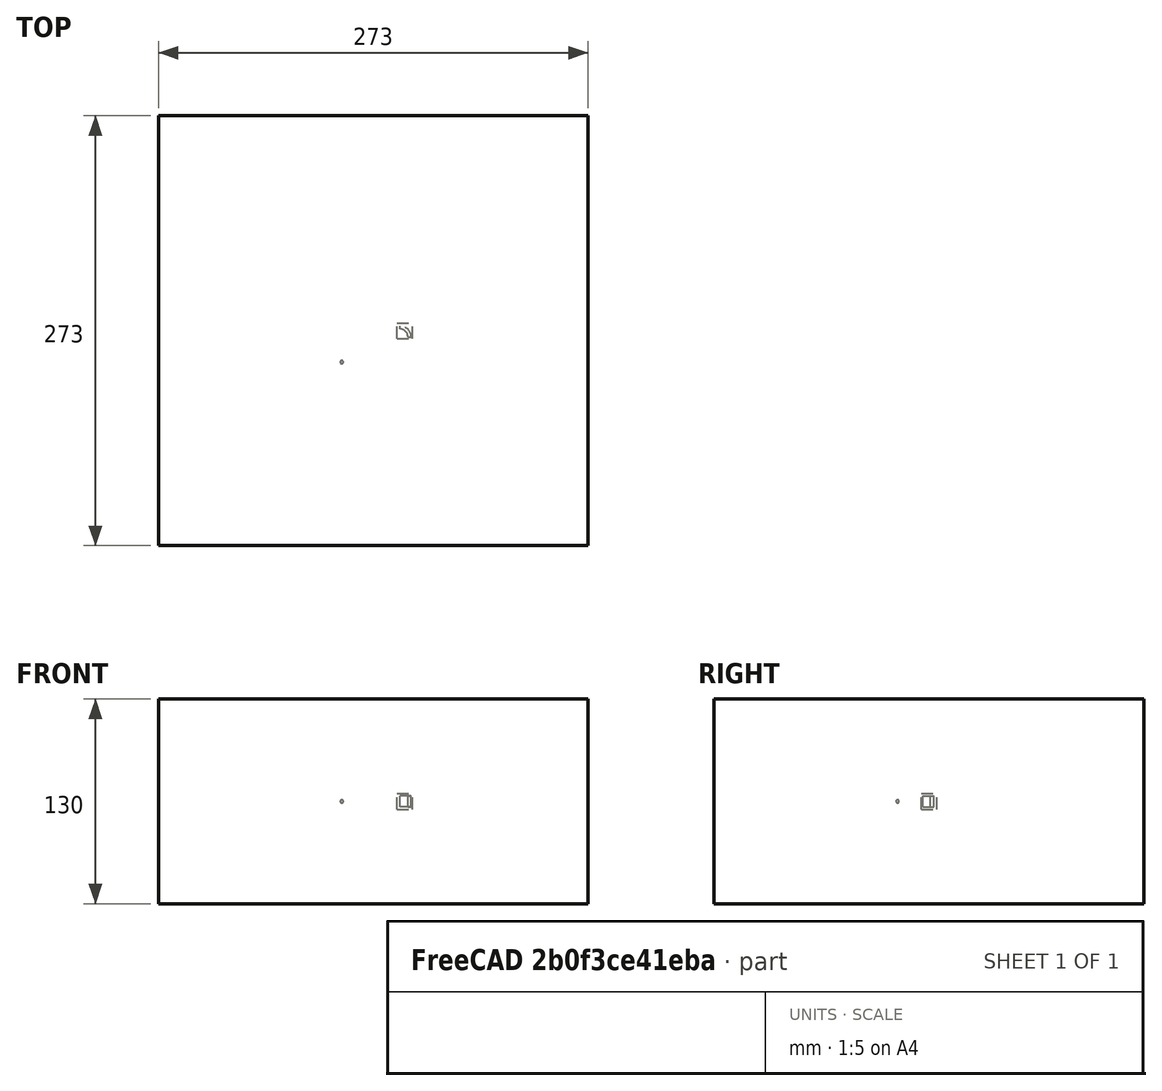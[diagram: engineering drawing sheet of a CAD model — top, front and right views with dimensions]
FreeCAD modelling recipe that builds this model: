
FCSTD DOCUMENT  (FreeCAD 0.21R33694 (Git))
Label: polarArray-of-Part-base-xformed-offcenter
License: All rights reserved
LicenseURL: http://en.wikipedia.org/wiki/All_rights_reserved
objects: App::DocumentObjectGroupPython×1251, App::Part×5, Part::FeaturePython×4, Part::Sphere×1
note: 4 computed .brp shape members not serialized (recipe doc carries the construction recipe); baked Part::Feature solids carry a one-line shape summary decoded from their .brp

FEATURE [App::DocumentObjectGroupPython] HALFPI  # scripted group (container) (typed FeaturePython)
  name = HALFPI
  value = pi/2.
FEATURE [App::DocumentObjectGroupPython] PI  # scripted group (container) (typed FeaturePython)
  name = PI
  value = 1.*pi
FEATURE [App::DocumentObjectGroupPython] TWOPI  # scripted group (container) (typed FeaturePython)
  name = TWOPI
  value = 2.*pi
FEATURE [App::DocumentObjectGroupPython] Constants  # scripted group (container) (typed FeaturePython)
  Group = -> [HALFPI,PI,TWOPI]
FEATURE [App::DocumentObjectGroupPython] Variables  # scripted group (container) (typed FeaturePython)
FEATURE [App::DocumentObjectGroupPython] Quantities  # scripted group (container) (typed FeaturePython)
FEATURE [App::DocumentObjectGroupPython] Isotopes  # scripted group (container) (typed FeaturePython)
FEATURE [App::DocumentObjectGroupPython] Elements  # scripted group (container) (typed FeaturePython)
FEATURE [App::DocumentObjectGroupPython] Matrix  # scripted group (container) (typed FeaturePython)
FEATURE [App::DocumentObjectGroupPython] Surfaces  # scripted group (container) (typed FeaturePython)
FEATURE [App::DocumentObjectGroupPython] Opticals  # scripted group (container) (typed FeaturePython)
  Group = -> [Matrix,Surfaces]
FEATURE [App::DocumentObjectGroupPython] G4Isotopes  # scripted group (container) (typed FeaturePython)
FEATURE [App::DocumentObjectGroupPython] H_element  # scripted group (container) (typed FeaturePython)
  Z = 1
  atom_value = 1.008
  formula = H
  name = H_element
FEATURE [App::DocumentObjectGroupPython] He_element  # scripted group (container) (typed FeaturePython)
  Z = 2
  atom_value = 4.0026
  formula = He
  name = He_element
FEATURE [App::DocumentObjectGroupPython] Li_element  # scripted group (container) (typed FeaturePython)
  Z = 3
  atom_value = 6.94
  formula = Li
  name = Li_element
FEATURE [App::DocumentObjectGroupPython] Be_element  # scripted group (container) (typed FeaturePython)
  Z = 4
  atom_value = 9.01218
  formula = Be
  name = Be_element
FEATURE [App::DocumentObjectGroupPython] B_element  # scripted group (container) (typed FeaturePython)
  Z = 5
  atom_value = 10.81
  formula = B
  name = B_element
FEATURE [App::DocumentObjectGroupPython] C_element  # scripted group (container) (typed FeaturePython)
  Z = 6
  atom_value = 12.011
  formula = C
  name = C_element
FEATURE [App::DocumentObjectGroupPython] N_element  # scripted group (container) (typed FeaturePython)
  Z = 7
  atom_value = 14.007
  formula = N
  name = N_element
FEATURE [App::DocumentObjectGroupPython] O_element  # scripted group (container) (typed FeaturePython)
  Z = 8
  atom_value = 15.999
  formula = O
  name = O_element
FEATURE [App::DocumentObjectGroupPython] F_element  # scripted group (container) (typed FeaturePython)
  Z = 9
  atom_value = 18.9984
  formula = F
  name = F_element
FEATURE [App::DocumentObjectGroupPython] Ne_element  # scripted group (container) (typed FeaturePython)
  Z = 10
  atom_value = 20.1797
  formula = Ne
  name = Ne_element
FEATURE [App::DocumentObjectGroupPython] Na_element  # scripted group (container) (typed FeaturePython)
  Z = 11
  atom_value = 22.9898
  formula = Na
  name = Na_element
FEATURE [App::DocumentObjectGroupPython] Mg_element  # scripted group (container) (typed FeaturePython)
  Z = 12
  atom_value = 24.305
  formula = Mg
  name = Mg_element
FEATURE [App::DocumentObjectGroupPython] Al_element  # scripted group (container) (typed FeaturePython)
  Z = 13
  atom_value = 26.9815
  formula = Al
  name = Al_element
FEATURE [App::DocumentObjectGroupPython] Si_element  # scripted group (container) (typed FeaturePython)
  Z = 14
  atom_value = 28.085
  formula = Si
  name = Si_element
FEATURE [App::DocumentObjectGroupPython] P_element  # scripted group (container) (typed FeaturePython)
  Z = 15
  atom_value = 30.9738
  formula = P
  name = P_element
FEATURE [App::DocumentObjectGroupPython] S_element  # scripted group (container) (typed FeaturePython)
  Z = 16
  atom_value = 32.06
  formula = S
  name = S_element
FEATURE [App::DocumentObjectGroupPython] Cl_element  # scripted group (container) (typed FeaturePython)
  Z = 17
  atom_value = 35.45
  formula = Cl
  name = Cl_element
FEATURE [App::DocumentObjectGroupPython] Ar_element  # scripted group (container) (typed FeaturePython)
  Z = 18
  atom_value = 39.95
  formula = Ar
  name = Ar_element
FEATURE [App::DocumentObjectGroupPython] K_element  # scripted group (container) (typed FeaturePython)
  Z = 19
  atom_value = 39.0983
  formula = K
  name = K_element
FEATURE [App::DocumentObjectGroupPython] Ca_element  # scripted group (container) (typed FeaturePython)
  Z = 20
  atom_value = 40.078
  formula = Ca
  name = Ca_element
FEATURE [App::DocumentObjectGroupPython] Sc_element  # scripted group (container) (typed FeaturePython)
  Z = 21
  atom_value = 44.9559
  formula = Sc
  name = Sc_element
FEATURE [App::DocumentObjectGroupPython] Ti_element  # scripted group (container) (typed FeaturePython)
  Z = 22
  atom_value = 47.867
  formula = Ti
  name = Ti_element
FEATURE [App::DocumentObjectGroupPython] V_element  # scripted group (container) (typed FeaturePython)
  Z = 23
  atom_value = 50.9415
  formula = V
  name = V_element
FEATURE [App::DocumentObjectGroupPython] Cr_element  # scripted group (container) (typed FeaturePython)
  Z = 24
  atom_value = 51.9961
  formula = Cr
  name = Cr_element
FEATURE [App::DocumentObjectGroupPython] Mn_element  # scripted group (container) (typed FeaturePython)
  Z = 25
  atom_value = 54.938
  formula = Mn
  name = Mn_element
FEATURE [App::DocumentObjectGroupPython] Fe_element  # scripted group (container) (typed FeaturePython)
  Z = 26
  atom_value = 55.845
  formula = Fe
  name = Fe_element
FEATURE [App::DocumentObjectGroupPython] Co_element  # scripted group (container) (typed FeaturePython)
  Z = 27
  atom_value = 58.9332
  formula = Co
  name = Co_element
FEATURE [App::DocumentObjectGroupPython] Ni_element  # scripted group (container) (typed FeaturePython)
  Z = 28
  atom_value = 58.6934
  formula = Ni
  name = Ni_element
FEATURE [App::DocumentObjectGroupPython] Cu_element  # scripted group (container) (typed FeaturePython)
  Z = 29
  atom_value = 63.546
  formula = Cu
  name = Cu_element
FEATURE [App::DocumentObjectGroupPython] Zn_element  # scripted group (container) (typed FeaturePython)
  Z = 30
  atom_value = 65.38
  formula = Zn
  name = Zn_element
FEATURE [App::DocumentObjectGroupPython] Ga_element  # scripted group (container) (typed FeaturePython)
  Z = 31
  atom_value = 69.723
  formula = Ga
  name = Ga_element
FEATURE [App::DocumentObjectGroupPython] Ge_element  # scripted group (container) (typed FeaturePython)
  Z = 32
  atom_value = 72.63
  formula = Ge
  name = Ge_element
FEATURE [App::DocumentObjectGroupPython] As_element  # scripted group (container) (typed FeaturePython)
  Z = 33
  atom_value = 74.9216
  formula = As
  name = As_element
FEATURE [App::DocumentObjectGroupPython] Se_element  # scripted group (container) (typed FeaturePython)
  Z = 34
  atom_value = 78.971
  formula = Se
  name = Se_element
FEATURE [App::DocumentObjectGroupPython] Br_element  # scripted group (container) (typed FeaturePython)
  Z = 35
  atom_value = 79.904
  formula = Br
  name = Br_element
FEATURE [App::DocumentObjectGroupPython] Kr_element  # scripted group (container) (typed FeaturePython)
  Z = 36
  atom_value = 83.798
  formula = Kr
  name = Kr_element
FEATURE [App::DocumentObjectGroupPython] Rb_element  # scripted group (container) (typed FeaturePython)
  Z = 37
  atom_value = 85.4678
  formula = Rb
  name = Rb_element
FEATURE [App::DocumentObjectGroupPython] Sr_element  # scripted group (container) (typed FeaturePython)
  Z = 38
  atom_value = 87.62
  formula = Sr
  name = Sr_element
FEATURE [App::DocumentObjectGroupPython] Y_element  # scripted group (container) (typed FeaturePython)
  Z = 39
  atom_value = 88.9058
  formula = Y
  name = Y_element
FEATURE [App::DocumentObjectGroupPython] Zr_element  # scripted group (container) (typed FeaturePython)
  Z = 40
  atom_value = 91.224
  formula = Zr
  name = Zr_element
FEATURE [App::DocumentObjectGroupPython] Nb_element  # scripted group (container) (typed FeaturePython)
  Z = 41
  atom_value = 92.9064
  formula = Nb
  name = Nb_element
FEATURE [App::DocumentObjectGroupPython] Mo_element  # scripted group (container) (typed FeaturePython)
  Z = 42
  atom_value = 95.95
  formula = Mo
  name = Mo_element
FEATURE [App::DocumentObjectGroupPython] Tc_element  # scripted group (container) (typed FeaturePython)
  Z = 43
  atom_value = 97
  formula = Tc
  name = Tc_element
FEATURE [App::DocumentObjectGroupPython] Ru_element  # scripted group (container) (typed FeaturePython)
  Z = 44
  atom_value = 101.07
  formula = Ru
  name = Ru_element
FEATURE [App::DocumentObjectGroupPython] Rh_element  # scripted group (container) (typed FeaturePython)
  Z = 45
  atom_value = 102.905
  formula = Rh
  name = Rh_element
FEATURE [App::DocumentObjectGroupPython] Pd_element  # scripted group (container) (typed FeaturePython)
  Z = 46
  atom_value = 106.42
  formula = Pd
  name = Pd_element
FEATURE [App::DocumentObjectGroupPython] Ag_element  # scripted group (container) (typed FeaturePython)
  Z = 47
  atom_value = 107.868
  formula = Ag
  name = Ag_element
FEATURE [App::DocumentObjectGroupPython] Cd_element  # scripted group (container) (typed FeaturePython)
  Z = 48
  atom_value = 112.414
  formula = Cd
  name = Cd_element
FEATURE [App::DocumentObjectGroupPython] In_element  # scripted group (container) (typed FeaturePython)
  Z = 49
  atom_value = 114.818
  formula = In
  name = In_element
FEATURE [App::DocumentObjectGroupPython] Sn_element  # scripted group (container) (typed FeaturePython)
  Z = 50
  atom_value = 118.71
  formula = Sn
  name = Sn_element
FEATURE [App::DocumentObjectGroupPython] Sb_element  # scripted group (container) (typed FeaturePython)
  Z = 51
  atom_value = 121.76
  formula = Sb
  name = Sb_element
FEATURE [App::DocumentObjectGroupPython] Te_element  # scripted group (container) (typed FeaturePython)
  Z = 52
  atom_value = 127.6
  formula = Te
  name = Te_element
FEATURE [App::DocumentObjectGroupPython] I_element  # scripted group (container) (typed FeaturePython)
  Z = 53
  atom_value = 126.904
  formula = I
  name = I_element
FEATURE [App::DocumentObjectGroupPython] Xe_element  # scripted group (container) (typed FeaturePython)
  Z = 54
  atom_value = 131.293
  formula = Xe
  name = Xe_element
FEATURE [App::DocumentObjectGroupPython] Cs_element  # scripted group (container) (typed FeaturePython)
  Z = 55
  atom_value = 132.905
  formula = Cs
  name = Cs_element
FEATURE [App::DocumentObjectGroupPython] Ba_element  # scripted group (container) (typed FeaturePython)
  Z = 56
  atom_value = 137.327
  formula = Ba
  name = Ba_element
FEATURE [App::DocumentObjectGroupPython] La_element  # scripted group (container) (typed FeaturePython)
  Z = 57
  atom_value = 138.905
  formula = La
  name = La_element
FEATURE [App::DocumentObjectGroupPython] Ce_element  # scripted group (container) (typed FeaturePython)
  Z = 58
  atom_value = 140.116
  formula = Ce
  name = Ce_element
FEATURE [App::DocumentObjectGroupPython] Pr_element  # scripted group (container) (typed FeaturePython)
  Z = 59
  atom_value = 140.908
  formula = Pr
  name = Pr_element
FEATURE [App::DocumentObjectGroupPython] Nd_element  # scripted group (container) (typed FeaturePython)
  Z = 60
  atom_value = 144.242
  formula = Nd
  name = Nd_element
FEATURE [App::DocumentObjectGroupPython] Pm_element  # scripted group (container) (typed FeaturePython)
  Z = 61
  atom_value = 145
  formula = Pm
  name = Pm_element
FEATURE [App::DocumentObjectGroupPython] Sm_element  # scripted group (container) (typed FeaturePython)
  Z = 62
  atom_value = 150.36
  formula = Sm
  name = Sm_element
FEATURE [App::DocumentObjectGroupPython] Eu_element  # scripted group (container) (typed FeaturePython)
  Z = 63
  atom_value = 151.964
  formula = Eu
  name = Eu_element
FEATURE [App::DocumentObjectGroupPython] Gd_element  # scripted group (container) (typed FeaturePython)
  Z = 64
  atom_value = 157.25
  formula = Gd
  name = Gd_element
FEATURE [App::DocumentObjectGroupPython] Tb_element  # scripted group (container) (typed FeaturePython)
  Z = 65
  atom_value = 158.925
  formula = Tb
  name = Tb_element
FEATURE [App::DocumentObjectGroupPython] Dy_element  # scripted group (container) (typed FeaturePython)
  Z = 66
  atom_value = 162.5
  formula = Dy
  name = Dy_element
FEATURE [App::DocumentObjectGroupPython] Ho_element  # scripted group (container) (typed FeaturePython)
  Z = 67
  atom_value = 164.93
  formula = Ho
  name = Ho_element
FEATURE [App::DocumentObjectGroupPython] Er_element  # scripted group (container) (typed FeaturePython)
  Z = 68
  atom_value = 167.259
  formula = Er
  name = Er_element
FEATURE [App::DocumentObjectGroupPython] Tm_element  # scripted group (container) (typed FeaturePython)
  Z = 69
  atom_value = 168.934
  formula = Tm
  name = Tm_element
FEATURE [App::DocumentObjectGroupPython] Yb_element  # scripted group (container) (typed FeaturePython)
  Z = 70
  atom_value = 173.045
  formula = Yb
  name = Yb_element
FEATURE [App::DocumentObjectGroupPython] Lu_element  # scripted group (container) (typed FeaturePython)
  Z = 71
  atom_value = 174.967
  formula = Lu
  name = Lu_element
FEATURE [App::DocumentObjectGroupPython] Hf_element  # scripted group (container) (typed FeaturePython)
  Z = 72
  atom_value = 178.49
  formula = Hf
  name = Hf_element
FEATURE [App::DocumentObjectGroupPython] Ta_element  # scripted group (container) (typed FeaturePython)
  Z = 73
  atom_value = 180.948
  formula = Ta
  name = Ta_element
FEATURE [App::DocumentObjectGroupPython] W_element  # scripted group (container) (typed FeaturePython)
  Z = 74
  atom_value = 183.84
  formula = W
  name = W_element
FEATURE [App::DocumentObjectGroupPython] Re_element  # scripted group (container) (typed FeaturePython)
  Z = 75
  atom_value = 186.207
  formula = Re
  name = Re_element
FEATURE [App::DocumentObjectGroupPython] Os_element  # scripted group (container) (typed FeaturePython)
  Z = 76
  atom_value = 190.23
  formula = Os
  name = Os_element
FEATURE [App::DocumentObjectGroupPython] Ir_element  # scripted group (container) (typed FeaturePython)
  Z = 77
  atom_value = 192.217
  formula = Ir
  name = Ir_element
FEATURE [App::DocumentObjectGroupPython] Pt_element  # scripted group (container) (typed FeaturePython)
  Z = 78
  atom_value = 195.084
  formula = Pt
  name = Pt_element
FEATURE [App::DocumentObjectGroupPython] Au_element  # scripted group (container) (typed FeaturePython)
  Z = 79
  atom_value = 196.967
  formula = Au
  name = Au_element
FEATURE [App::DocumentObjectGroupPython] Hg_element  # scripted group (container) (typed FeaturePython)
  Z = 80
  atom_value = 200.592
  formula = Hg
  name = Hg_element
FEATURE [App::DocumentObjectGroupPython] Tl_element  # scripted group (container) (typed FeaturePython)
  Z = 81
  atom_value = 204.38
  formula = Tl
  name = Tl_element
FEATURE [App::DocumentObjectGroupPython] Pb_element  # scripted group (container) (typed FeaturePython)
  Z = 82
  atom_value = 207.2
  formula = Pb
  name = Pb_element
FEATURE [App::DocumentObjectGroupPython] Bi_element  # scripted group (container) (typed FeaturePython)
  Z = 83
  atom_value = 208.98
  formula = Bi
  name = Bi_element
FEATURE [App::DocumentObjectGroupPython] Po_element  # scripted group (container) (typed FeaturePython)
  Z = 84
  atom_value = 209
  formula = Po
  name = Po_element
FEATURE [App::DocumentObjectGroupPython] At_element  # scripted group (container) (typed FeaturePython)
  Z = 85
  atom_value = 210
  formula = At
  name = At_element
FEATURE [App::DocumentObjectGroupPython] Rn_element  # scripted group (container) (typed FeaturePython)
  Z = 86
  atom_value = 222
  formula = Rn
  name = Rn_element
FEATURE [App::DocumentObjectGroupPython] Fr_element  # scripted group (container) (typed FeaturePython)
  Z = 87
  atom_value = 223
  formula = Fr
  name = Fr_element
FEATURE [App::DocumentObjectGroupPython] Ra_element  # scripted group (container) (typed FeaturePython)
  Z = 88
  atom_value = 226
  formula = Ra
  name = Ra_element
FEATURE [App::DocumentObjectGroupPython] Ac_element  # scripted group (container) (typed FeaturePython)
  Z = 89
  atom_value = 227
  formula = Ac
  name = Ac_element
FEATURE [App::DocumentObjectGroupPython] Th_element  # scripted group (container) (typed FeaturePython)
  Z = 90
  atom_value = 232.038
  formula = Th
  name = Th_element
FEATURE [App::DocumentObjectGroupPython] Pa_element  # scripted group (container) (typed FeaturePython)
  Z = 91
  atom_value = 231.036
  formula = Pa
  name = Pa_element
FEATURE [App::DocumentObjectGroupPython] U_element  # scripted group (container) (typed FeaturePython)
  Z = 92
  atom_value = 238.029
  formula = U
  name = U_element
FEATURE [App::DocumentObjectGroupPython] Np_element  # scripted group (container) (typed FeaturePython)
  Z = 93
  atom_value = 237
  formula = Np
  name = Np_element
FEATURE [App::DocumentObjectGroupPython] Pu_element  # scripted group (container) (typed FeaturePython)
  Z = 94
  atom_value = 244
  formula = Pu
  name = Pu_element
FEATURE [App::DocumentObjectGroupPython] Am_element  # scripted group (container) (typed FeaturePython)
  Z = 95
  atom_value = 243
  formula = Am
  name = Am_element
FEATURE [App::DocumentObjectGroupPython] Cm_element  # scripted group (container) (typed FeaturePython)
  Z = 96
  atom_value = 247
  formula = Cm
  name = Cm_element
FEATURE [App::DocumentObjectGroupPython] Bk_element  # scripted group (container) (typed FeaturePython)
  Z = 97
  atom_value = 247
  formula = Bk
  name = Bk_element
FEATURE [App::DocumentObjectGroupPython] Cf_element  # scripted group (container) (typed FeaturePython)
  Z = 98
  atom_value = 251
  formula = Cf
  name = Cf_element
FEATURE [App::DocumentObjectGroupPython] G4Elements  # scripted group (container) (typed FeaturePython)
  Group = -> [H_element,He_element,Li_element,Be_element,B_element,C_element,N_element,O_element,F_element,Ne_element,Na_element,Mg_element,Al_element,Si_element,P_element,S_element,Cl_element,Ar_element,K_element,Ca_element,Sc_element,Ti_element,V_element,Cr_element,Mn_element,Fe_element,Co_element,Ni_element,Cu_element,Zn_element,Ga_element,Ge_element,As_element,Se_element,Br_element,Kr_element,Rb_element,+61 more]
FEATURE [App::DocumentObjectGroupPython] H_element001  label="H_element : 0.101"  # scripted group (container) (typed FeaturePython)
  n = 0.101327
FEATURE [App::DocumentObjectGroupPython] C_element001  label="C_element : 0.775"  # scripted group (container) (typed FeaturePython)
  n = 0.7755
FEATURE [App::DocumentObjectGroupPython] N_element001  label="N_element : 0.035"  # scripted group (container) (typed FeaturePython)
  n = 0.035057
FEATURE [App::DocumentObjectGroupPython] O_element001  label="O_element : 0.052"  # scripted group (container) (typed FeaturePython)
  n = 0.0523159
FEATURE [App::DocumentObjectGroupPython] F_element001  label="F_element : 0.017"  # scripted group (container) (typed FeaturePython)
  n = 0.017422
FEATURE [App::DocumentObjectGroupPython] Ca_element001  label="Ca_element : 0.018"  # scripted group (container) (typed FeaturePython)
  n = 0.018378
FEATURE [App::DocumentObjectGroupPython] G4_A_150_TISSUE  label="G4_A-150_TISSUE"  # scripted group (container) (typed FeaturePython)
  Dunit = g/cm3
  Dvalue = 1.127
  Group = -> [H_element001,C_element001,N_element001,O_element001,F_element001,Ca_element001]
  conduct = 2
  density = 1
  expand = 3
  formula = G4_A-150_TISSUE
  name = G4_A-150_TISSUE
  specific = 4
FEATURE [App::DocumentObjectGroupPython] C_element002  label="C_element : 3"  # scripted group (container) (typed FeaturePython)
  n = 3
  ref = C_element
FEATURE [App::DocumentObjectGroupPython] H_element002  label="H_element : 6"  # scripted group (container) (typed FeaturePython)
  n = 6
  ref = H_element
FEATURE [App::DocumentObjectGroupPython] O_element002  label="O_element : 1"  # scripted group (container) (typed FeaturePython)
  n = 1
  ref = O_element
FEATURE [App::DocumentObjectGroupPython] G4_ACETONE  # scripted group (container) (typed FeaturePython)
  Dunit = g/cm3
  Dvalue = 0.7899
  Group = -> [C_element002,H_element002,O_element002]
  conduct = 2
  density = 1
  expand = 3
  formula = G4_ACETONE
  name = G4_ACETONE
  specific = 4
FEATURE [App::DocumentObjectGroupPython] C_element003  label="C_element : 2"  # scripted group (container) (typed FeaturePython)
  n = 2
  ref = C_element
FEATURE [App::DocumentObjectGroupPython] H_element003  label="H_element : 2"  # scripted group (container) (typed FeaturePython)
  n = 2
  ref = H_element
FEATURE [App::DocumentObjectGroupPython] G4_ACETYLENE  # scripted group (container) (typed FeaturePython)
  Dunit = g/cm3
  Dvalue = 0.0010967
  Group = -> [C_element003,H_element003]
  conduct = 2
  density = 1
  expand = 3
  formula = G4_ACETYLENE
  name = G4_ACETYLENE
  specific = 4
FEATURE [App::DocumentObjectGroupPython] C_element004  label="C_element : 5"  # scripted group (container) (typed FeaturePython)
  n = 5
  ref = C_element
FEATURE [App::DocumentObjectGroupPython] H_element004  label="H_element : 5"  # scripted group (container) (typed FeaturePython)
  n = 5
  ref = H_element
FEATURE [App::DocumentObjectGroupPython] N_element002  label="N_element : 5"  # scripted group (container) (typed FeaturePython)
  n = 5
  ref = N_element
FEATURE [App::DocumentObjectGroupPython] G4_ADENINE  # scripted group (container) (typed FeaturePython)
  Dunit = g/cm3
  Dvalue = 1.6
  Group = -> [C_element004,H_element004,N_element002]
  conduct = 2
  density = 1
  expand = 3
  formula = G4_ADENINE
  name = G4_ADENINE
  specific = 4
FEATURE [App::DocumentObjectGroupPython] H_element005  label="H_element : 0.114"  # scripted group (container) (typed FeaturePython)
  n = 0.114
FEATURE [App::DocumentObjectGroupPython] C_element005  label="C_element : 0.598"  # scripted group (container) (typed FeaturePython)
  n = 0.598
FEATURE [App::DocumentObjectGroupPython] N_element003  label="N_element : 0.007"  # scripted group (container) (typed FeaturePython)
  n = 0.007
FEATURE [App::DocumentObjectGroupPython] O_element003  label="O_element : 0.278"  # scripted group (container) (typed FeaturePython)
  n = 0.278
FEATURE [App::DocumentObjectGroupPython] Na_element001  label="Na_element : 0.001"  # scripted group (container) (typed FeaturePython)
  n = 0.001
FEATURE [App::DocumentObjectGroupPython] S_element001  label="S_element : 0.001"  # scripted group (container) (typed FeaturePython)
  n = 0.001
FEATURE [App::DocumentObjectGroupPython] Cl_element001  label="Cl_element : 0.001"  # scripted group (container) (typed FeaturePython)
  n = 0.001
FEATURE [App::DocumentObjectGroupPython] G4_ADIPOSE_TISSUE_ICRP  # scripted group (container) (typed FeaturePython)
  Dunit = g/cm3
  Dvalue = 0.95
  Group = -> [H_element005,C_element005,N_element003,O_element003,Na_element001,S_element001,Cl_element001]
  conduct = 2
  density = 1
  expand = 3
  formula = G4_ADIPOSE_TISSUE_ICRP
  name = G4_ADIPOSE_TISSUE_ICRP
  specific = 4
FEATURE [App::DocumentObjectGroupPython] C_element006  label="C_element : 0.000"  # scripted group (container) (typed FeaturePython)
  n = 0.000124
FEATURE [App::DocumentObjectGroupPython] N_element004  label="N_element : 0.755"  # scripted group (container) (typed FeaturePython)
  n = 0.755268
FEATURE [App::DocumentObjectGroupPython] O_element004  label="O_element : 0.232"  # scripted group (container) (typed FeaturePython)
  n = 0.231781
FEATURE [App::DocumentObjectGroupPython] Ar_element001  label="Ar_element : 0.013"  # scripted group (container) (typed FeaturePython)
  n = 0.012827
FEATURE [App::DocumentObjectGroupPython] G4_AIR  # scripted group (container) (typed FeaturePython)
  Dunit = g/cm3
  Dvalue = 0.00120479
  Group = -> [C_element006,N_element004,O_element004,Ar_element001]
  conduct = 2
  density = 1
  expand = 3
  formula = G4_AIR
  name = G4_AIR
  specific = 4
FEATURE [App::DocumentObjectGroupPython] C_element007  label="C_element : 006"  # scripted group (container) (typed FeaturePython)
  n = 3
  ref = C_element
FEATURE [App::DocumentObjectGroupPython] H_element006  label="H_element : 7"  # scripted group (container) (typed FeaturePython)
  n = 7
  ref = H_element
FEATURE [App::DocumentObjectGroupPython] N_element005  label="N_element : 1"  # scripted group (container) (typed FeaturePython)
  n = 1
  ref = N_element
FEATURE [App::DocumentObjectGroupPython] O_element005  label="O_element : 2"  # scripted group (container) (typed FeaturePython)
  n = 2
  ref = O_element
FEATURE [App::DocumentObjectGroupPython] G4_ALANINE  # scripted group (container) (typed FeaturePython)
  Dunit = g/cm3
  Dvalue = 1.42
  Group = -> [C_element007,H_element006,N_element005,O_element005]
  conduct = 2
  density = 1
  expand = 3
  formula = G4_ALANINE
  name = G4_ALANINE
  specific = 4
FEATURE [App::DocumentObjectGroupPython] Al_element001  label="Al_element : 2"  # scripted group (container) (typed FeaturePython)
  n = 2
  ref = Al_element
FEATURE [App::DocumentObjectGroupPython] O_element006  label="O_element : 3"  # scripted group (container) (typed FeaturePython)
  n = 3
  ref = O_element
FEATURE [App::DocumentObjectGroupPython] G4_ALUMINUM_OXIDE  # scripted group (container) (typed FeaturePython)
  Dunit = g/cm3
  Dvalue = 3.97
  Group = -> [Al_element001,O_element006]
  conduct = 2
  density = 1
  expand = 3
  formula = G4_ALUMINUM_OXIDE
  name = G4_ALUMINUM_OXIDE
  specific = 4
FEATURE [App::DocumentObjectGroupPython] H_element007  label="H_element : 0.106"  # scripted group (container) (typed FeaturePython)
  n = 0.10593
FEATURE [App::DocumentObjectGroupPython] C_element008  label="C_element : 0.789"  # scripted group (container) (typed FeaturePython)
  n = 0.788974
FEATURE [App::DocumentObjectGroupPython] O_element007  label="O_element : 0.105"  # scripted group (container) (typed FeaturePython)
  n = 0.105096
FEATURE [App::DocumentObjectGroupPython] G4_AMBER  # scripted group (container) (typed FeaturePython)
  Dunit = g/cm3
  Dvalue = 1.1
  Group = -> [H_element007,C_element008,O_element007]
  conduct = 2
  density = 1
  expand = 3
  formula = G4_AMBER
  name = G4_AMBER
  specific = 4
FEATURE [App::DocumentObjectGroupPython] N_element006  label="N_element : 006"  # scripted group (container) (typed FeaturePython)
  n = 1
  ref = N_element
FEATURE [App::DocumentObjectGroupPython] H_element008  label="H_element : 3"  # scripted group (container) (typed FeaturePython)
  n = 3
  ref = H_element
FEATURE [App::DocumentObjectGroupPython] G4_AMMONIA  # scripted group (container) (typed FeaturePython)
  Dunit = g/cm3
  Dvalue = 0.000826019
  Group = -> [N_element006,H_element008]
  conduct = 2
  density = 1
  expand = 3
  formula = G4_AMMONIA
  name = G4_AMMONIA
  specific = 4
FEATURE [App::DocumentObjectGroupPython] C_element009  label="C_element : 6"  # scripted group (container) (typed FeaturePython)
  n = 6
  ref = C_element
FEATURE [App::DocumentObjectGroupPython] H_element009  label="H_element : 008"  # scripted group (container) (typed FeaturePython)
  n = 7
  ref = H_element
FEATURE [App::DocumentObjectGroupPython] N_element007  label="N_element : 007"  # scripted group (container) (typed FeaturePython)
  n = 1
  ref = N_element
FEATURE [App::DocumentObjectGroupPython] G4_ANILINE  # scripted group (container) (typed FeaturePython)
  Dunit = g/cm3
  Dvalue = 1.0235
  Group = -> [C_element009,H_element009,N_element007]
  conduct = 2
  density = 1
  expand = 3
  formula = G4_ANILINE
  name = G4_ANILINE
  specific = 4
FEATURE [App::DocumentObjectGroupPython] C_element010  label="C_element : 14"  # scripted group (container) (typed FeaturePython)
  n = 14
  ref = C_element
FEATURE [App::DocumentObjectGroupPython] H_element010  label="H_element : 10"  # scripted group (container) (typed FeaturePython)
  n = 10
  ref = H_element
FEATURE [App::DocumentObjectGroupPython] G4_ANTHRACENE  # scripted group (container) (typed FeaturePython)
  Dunit = g/cm3
  Dvalue = 1.283
  Group = -> [C_element010,H_element010]
  conduct = 2
  density = 1
  expand = 3
  formula = G4_ANTHRACENE
  name = G4_ANTHRACENE
  specific = 4
FEATURE [App::DocumentObjectGroupPython] H_element011  label="H_element : 0.065"  # scripted group (container) (typed FeaturePython)
  n = 0.0654709
FEATURE [App::DocumentObjectGroupPython] C_element011  label="C_element : 0.537"  # scripted group (container) (typed FeaturePython)
  n = 0.536944
FEATURE [App::DocumentObjectGroupPython] N_element008  label="N_element : 0.021"  # scripted group (container) (typed FeaturePython)
  n = 0.0215
FEATURE [App::DocumentObjectGroupPython] O_element008  label="O_element : 0.032"  # scripted group (container) (typed FeaturePython)
  n = 0.032085
FEATURE [App::DocumentObjectGroupPython] F_element002  label="F_element : 0.167"  # scripted group (container) (typed FeaturePython)
  n = 0.167411
FEATURE [App::DocumentObjectGroupPython] Ca_element002  label="Ca_element : 0.177"  # scripted group (container) (typed FeaturePython)
  n = 0.176589
FEATURE [App::DocumentObjectGroupPython] G4_B_100_BONE  label="G4_B-100_BONE"  # scripted group (container) (typed FeaturePython)
  Dunit = g/cm3
  Dvalue = 1.45
  Group = -> [H_element011,C_element011,N_element008,O_element008,F_element002,Ca_element002]
  conduct = 2
  density = 1
  expand = 3
  formula = G4_B-100_BONE
  name = G4_B-100_BONE
  specific = 4
FEATURE [App::DocumentObjectGroupPython] H_element012  label="H_element : 0.057"  # scripted group (container) (typed FeaturePython)
  n = 0.057441
FEATURE [App::DocumentObjectGroupPython] C_element012  label="C_element : 0.790"  # scripted group (container) (typed FeaturePython)
  n = 0.774591
FEATURE [App::DocumentObjectGroupPython] O_element009  label="O_element : 0.168"  # scripted group (container) (typed FeaturePython)
  n = 0.167968
FEATURE [App::DocumentObjectGroupPython] G4_BAKELITE  # scripted group (container) (typed FeaturePython)
  Dunit = g/cm3
  Dvalue = 1.25
  Group = -> [H_element012,C_element012,O_element009]
  conduct = 2
  density = 1
  expand = 3
  formula = G4_BAKELITE
  name = G4_BAKELITE
  specific = 4
FEATURE [App::DocumentObjectGroupPython] Ba_element001  label="Ba_element : 1"  # scripted group (container) (typed FeaturePython)
  n = 1
  ref = Ba_element
FEATURE [App::DocumentObjectGroupPython] F_element003  label="F_element : 2"  # scripted group (container) (typed FeaturePython)
  n = 2
  ref = F_element
FEATURE [App::DocumentObjectGroupPython] G4_BARIUM_FLUORIDE  # scripted group (container) (typed FeaturePython)
  Dunit = g/cm3
  Dvalue = 4.89
  Group = -> [Ba_element001,F_element003]
  conduct = 2
  density = 1
  expand = 3
  formula = G4_BARIUM_FLUORIDE
  name = G4_BARIUM_FLUORIDE
  specific = 4
FEATURE [App::DocumentObjectGroupPython] Ba_element002  label="Ba_element : 002"  # scripted group (container) (typed FeaturePython)
  n = 1
  ref = Ba_element
FEATURE [App::DocumentObjectGroupPython] S_element002  label="S_element : 1"  # scripted group (container) (typed FeaturePython)
  n = 1
  ref = S_element
FEATURE [App::DocumentObjectGroupPython] O_element010  label="O_element : 4"  # scripted group (container) (typed FeaturePython)
  n = 4
  ref = O_element
FEATURE [App::DocumentObjectGroupPython] G4_BARIUM_SULFATE  # scripted group (container) (typed FeaturePython)
  Dunit = g/cm3
  Dvalue = 4.5
  Group = -> [Ba_element002,S_element002,O_element010]
  conduct = 2
  density = 1
  expand = 3
  formula = G4_BARIUM_SULFATE
  name = G4_BARIUM_SULFATE
  specific = 4
FEATURE [App::DocumentObjectGroupPython] C_element013  label="C_element : 007"  # scripted group (container) (typed FeaturePython)
  n = 6
  ref = C_element
FEATURE [App::DocumentObjectGroupPython] H_element013  label="H_element : 009"  # scripted group (container) (typed FeaturePython)
  n = 6
  ref = H_element
FEATURE [App::DocumentObjectGroupPython] G4_BENZENE  # scripted group (container) (typed FeaturePython)
  Dunit = g/cm3
  Dvalue = 0.87865
  Group = -> [C_element013,H_element013]
  conduct = 2
  density = 1
  expand = 3
  formula = G4_BENZENE
  name = G4_BENZENE
  specific = 4
FEATURE [App::DocumentObjectGroupPython] Be_element001  label="Be_element : 1"  # scripted group (container) (typed FeaturePython)
  n = 1
  ref = Be_element
FEATURE [App::DocumentObjectGroupPython] O_element011  label="O_element : 005"  # scripted group (container) (typed FeaturePython)
  n = 1
  ref = O_element
FEATURE [App::DocumentObjectGroupPython] G4_BERYLLIUM_OXIDE  # scripted group (container) (typed FeaturePython)
  Dunit = g/cm3
  Dvalue = 3.01
  Group = -> [Be_element001,O_element011]
  conduct = 2
  density = 1
  expand = 3
  formula = G4_BERYLLIUM_OXIDE
  name = G4_BERYLLIUM_OXIDE
  specific = 4
FEATURE [App::DocumentObjectGroupPython] Bi_element001  label="Bi_element : 4"  # scripted group (container) (typed FeaturePython)
  n = 4
  ref = Bi_element
FEATURE [App::DocumentObjectGroupPython] Ge_element001  label="Ge_element : 3"  # scripted group (container) (typed FeaturePython)
  n = 3
  ref = Ge_element
FEATURE [App::DocumentObjectGroupPython] O_element012  label="O_element : 12"  # scripted group (container) (typed FeaturePython)
  n = 12
  ref = O_element
FEATURE [App::DocumentObjectGroupPython] G4_BGO  # scripted group (container) (typed FeaturePython)
  Dunit = g/cm3
  Dvalue = 7.13
  Group = -> [Bi_element001,Ge_element001,O_element012]
  conduct = 2
  density = 1
  expand = 3
  formula = G4_BGO
  name = G4_BGO
  specific = 4
FEATURE [App::DocumentObjectGroupPython] H_element014  label="H_element : 0.102"  # scripted group (container) (typed FeaturePython)
  n = 0.102
FEATURE [App::DocumentObjectGroupPython] C_element014  label="C_element : 0.110"  # scripted group (container) (typed FeaturePython)
  n = 0.11
FEATURE [App::DocumentObjectGroupPython] N_element009  label="N_element : 0.033"  # scripted group (container) (typed FeaturePython)
  n = 0.033
FEATURE [App::DocumentObjectGroupPython] O_element013  label="O_element : 0.745"  # scripted group (container) (typed FeaturePython)
  n = 0.745
FEATURE [App::DocumentObjectGroupPython] Na_element002  label="Na_element : 0.002"  # scripted group (container) (typed FeaturePython)
  n = 0.001
FEATURE [App::DocumentObjectGroupPython] P_element001  label="P_element : 0.001"  # scripted group (container) (typed FeaturePython)
  n = 0.001
FEATURE [App::DocumentObjectGroupPython] S_element003  label="S_element : 0.002"  # scripted group (container) (typed FeaturePython)
  n = 0.002
FEATURE [App::DocumentObjectGroupPython] Cl_element002  label="Cl_element : 0.003"  # scripted group (container) (typed FeaturePython)
  n = 0.003
FEATURE [App::DocumentObjectGroupPython] K_element001  label="K_element : 0.002"  # scripted group (container) (typed FeaturePython)
  n = 0.002
FEATURE [App::DocumentObjectGroupPython] Fe_element001  label="Fe_element : 0.001"  # scripted group (container) (typed FeaturePython)
  n = 0.001
FEATURE [App::DocumentObjectGroupPython] G4_BLOOD_ICRP  # scripted group (container) (typed FeaturePython)
  Dunit = g/cm3
  Dvalue = 1.06
  Group = -> [H_element014,C_element014,N_element009,O_element013,Na_element002,P_element001,S_element003,Cl_element002,K_element001,Fe_element001]
  conduct = 2
  density = 1
  expand = 3
  formula = G4_BLOOD_ICRP
  name = G4_BLOOD_ICRP
  specific = 4
FEATURE [App::DocumentObjectGroupPython] H_element015  label="H_element : 0.064"  # scripted group (container) (typed FeaturePython)
  n = 0.064
FEATURE [App::DocumentObjectGroupPython] C_element015  label="C_element : 0.278"  # scripted group (container) (typed FeaturePython)
  n = 0.278
FEATURE [App::DocumentObjectGroupPython] N_element010  label="N_element : 0.027"  # scripted group (container) (typed FeaturePython)
  n = 0.027
FEATURE [App::DocumentObjectGroupPython] O_element014  label="O_element : 0.410"  # scripted group (container) (typed FeaturePython)
  n = 0.41
FEATURE [App::DocumentObjectGroupPython] Mg_element001  label="Mg_element : 0.002"  # scripted group (container) (typed FeaturePython)
  n = 0.002
FEATURE [App::DocumentObjectGroupPython] P_element002  label="P_element : 0.070"  # scripted group (container) (typed FeaturePython)
  n = 0.07
FEATURE [App::DocumentObjectGroupPython] S_element004  label="S_element : 0.003"  # scripted group (container) (typed FeaturePython)
  n = 0.002
FEATURE [App::DocumentObjectGroupPython] Ca_element003  label="Ca_element : 0.147"  # scripted group (container) (typed FeaturePython)
  n = 0.147
FEATURE [App::DocumentObjectGroupPython] G4_BONE_COMPACT_ICRU  # scripted group (container) (typed FeaturePython)
  Dunit = g/cm3
  Dvalue = 1.85
  Group = -> [H_element015,C_element015,N_element010,O_element014,Mg_element001,P_element002,S_element004,Ca_element003]
  conduct = 2
  density = 1
  expand = 3
  formula = G4_BONE_COMPACT_ICRU
  name = G4_BONE_COMPACT_ICRU
  specific = 4
FEATURE [App::DocumentObjectGroupPython] H_element016  label="H_element : 0.034"  # scripted group (container) (typed FeaturePython)
  n = 0.034
FEATURE [App::DocumentObjectGroupPython] C_element016  label="C_element : 0.155"  # scripted group (container) (typed FeaturePython)
  n = 0.155
FEATURE [App::DocumentObjectGroupPython] N_element011  label="N_element : 0.042"  # scripted group (container) (typed FeaturePython)
  n = 0.042
FEATURE [App::DocumentObjectGroupPython] O_element015  label="O_element : 0.435"  # scripted group (container) (typed FeaturePython)
  n = 0.435
FEATURE [App::DocumentObjectGroupPython] Na_element003  label="Na_element : 0.003"  # scripted group (container) (typed FeaturePython)
  n = 0.001
FEATURE [App::DocumentObjectGroupPython] Mg_element002  label="Mg_element : 0.003"  # scripted group (container) (typed FeaturePython)
  n = 0.002
FEATURE [App::DocumentObjectGroupPython] P_element003  label="P_element : 0.103"  # scripted group (container) (typed FeaturePython)
  n = 0.103
FEATURE [App::DocumentObjectGroupPython] S_element005  label="S_element : 0.004"  # scripted group (container) (typed FeaturePython)
  n = 0.003
FEATURE [App::DocumentObjectGroupPython] Ca_element004  label="Ca_element : 0.225"  # scripted group (container) (typed FeaturePython)
  n = 0.225
FEATURE [App::DocumentObjectGroupPython] G4_BONE_CORTICAL_ICRP  # scripted group (container) (typed FeaturePython)
  Dunit = g/cm3
  Dvalue = 1.92
  Group = -> [H_element016,C_element016,N_element011,O_element015,Na_element003,Mg_element002,P_element003,S_element005,Ca_element004]
  conduct = 2
  density = 1
  expand = 3
  formula = G4_BONE_CORTICAL_ICRP
  name = G4_BONE_CORTICAL_ICRP
  specific = 4
FEATURE [App::DocumentObjectGroupPython] B_element001  label="B_element : 4"  # scripted group (container) (typed FeaturePython)
  n = 4
  ref = B_element
FEATURE [App::DocumentObjectGroupPython] C_element017  label="C_element : 1"  # scripted group (container) (typed FeaturePython)
  n = 1
  ref = C_element
FEATURE [App::DocumentObjectGroupPython] G4_BORON_CARBIDE  # scripted group (container) (typed FeaturePython)
  Dunit = g/cm3
  Dvalue = 2.52
  Group = -> [B_element001,C_element017]
  conduct = 2
  density = 1
  expand = 3
  formula = G4_BORON_CARBIDE
  name = G4_BORON_CARBIDE
  specific = 4
FEATURE [App::DocumentObjectGroupPython] B_element002  label="B_element : 2"  # scripted group (container) (typed FeaturePython)
  n = 2
  ref = B_element
FEATURE [App::DocumentObjectGroupPython] O_element016  label="O_element : 006"  # scripted group (container) (typed FeaturePython)
  n = 3
  ref = O_element
FEATURE [App::DocumentObjectGroupPython] G4_BORON_OXIDE  # scripted group (container) (typed FeaturePython)
  Dunit = g/cm3
  Dvalue = 1.812
  Group = -> [B_element002,O_element016]
  conduct = 2
  density = 1
  expand = 3
  formula = G4_BORON_OXIDE
  name = G4_BORON_OXIDE
  specific = 4
FEATURE [App::DocumentObjectGroupPython] H_element017  label="H_element : 0.107"  # scripted group (container) (typed FeaturePython)
  n = 0.107
FEATURE [App::DocumentObjectGroupPython] C_element018  label="C_element : 0.145"  # scripted group (container) (typed FeaturePython)
  n = 0.145
FEATURE [App::DocumentObjectGroupPython] N_element012  label="N_element : 0.022"  # scripted group (container) (typed FeaturePython)
  n = 0.022
FEATURE [App::DocumentObjectGroupPython] O_element017  label="O_element : 0.712"  # scripted group (container) (typed FeaturePython)
  n = 0.712
FEATURE [App::DocumentObjectGroupPython] Na_element004  label="Na_element : 0.004"  # scripted group (container) (typed FeaturePython)
  n = 0.002
FEATURE [App::DocumentObjectGroupPython] P_element004  label="P_element : 0.004"  # scripted group (container) (typed FeaturePython)
  n = 0.004
FEATURE [App::DocumentObjectGroupPython] S_element006  label="S_element : 0.005"  # scripted group (container) (typed FeaturePython)
  n = 0.002
FEATURE [App::DocumentObjectGroupPython] Cl_element003  label="Cl_element : 0.004"  # scripted group (container) (typed FeaturePython)
  n = 0.003
FEATURE [App::DocumentObjectGroupPython] K_element002  label="K_element : 0.003"  # scripted group (container) (typed FeaturePython)
  n = 0.003
FEATURE [App::DocumentObjectGroupPython] G4_BRAIN_ICRP  # scripted group (container) (typed FeaturePython)
  Dunit = g/cm3
  Dvalue = 1.04
  Group = -> [H_element017,C_element018,N_element012,O_element017,Na_element004,P_element004,S_element006,Cl_element003,K_element002]
  conduct = 2
  density = 1
  expand = 3
  formula = G4_BRAIN_ICRP
  name = G4_BRAIN_ICRP
  specific = 4
FEATURE [App::DocumentObjectGroupPython] C_element019  label="C_element : 4"  # scripted group (container) (typed FeaturePython)
  n = 4
  ref = C_element
FEATURE [App::DocumentObjectGroupPython] H_element018  label="H_element : 010"  # scripted group (container) (typed FeaturePython)
  n = 10
  ref = H_element
FEATURE [App::DocumentObjectGroupPython] G4_BUTANE  # scripted group (container) (typed FeaturePython)
  Dunit = g/cm3
  Dvalue = 0.00249343
  Group = -> [C_element019,H_element018]
  conduct = 2
  density = 1
  expand = 3
  formula = G4_BUTANE
  name = G4_BUTANE
  specific = 4
FEATURE [App::DocumentObjectGroupPython] C_element020  label="C_element : 008"  # scripted group (container) (typed FeaturePython)
  n = 4
  ref = C_element
FEATURE [App::DocumentObjectGroupPython] H_element019  label="H_element : 011"  # scripted group (container) (typed FeaturePython)
  n = 10
  ref = H_element
FEATURE [App::DocumentObjectGroupPython] O_element018  label="O_element : 007"  # scripted group (container) (typed FeaturePython)
  n = 1
  ref = O_element
FEATURE [App::DocumentObjectGroupPython] G4_N_BUTYL_ALCOHOL  label="G4_N-BUTYL_ALCOHOL"  # scripted group (container) (typed FeaturePython)
  Dunit = g/cm3
  Dvalue = 0.8098
  Group = -> [C_element020,H_element019,O_element018]
  conduct = 2
  density = 1
  expand = 3
  formula = G4_N-BUTYL_ALCOHOL
  name = G4_N-BUTYL_ALCOHOL
  specific = 4
FEATURE [App::DocumentObjectGroupPython] H_element020  label="H_element : 0.025"  # scripted group (container) (typed FeaturePython)
  n = 0.02468
FEATURE [App::DocumentObjectGroupPython] C_element021  label="C_element : 0.502"  # scripted group (container) (typed FeaturePython)
  n = 0.501611
FEATURE [App::DocumentObjectGroupPython] O_element019  label="O_element : 0.005"  # scripted group (container) (typed FeaturePython)
  n = 0.004527
FEATURE [App::DocumentObjectGroupPython] F_element004  label="F_element : 0.465"  # scripted group (container) (typed FeaturePython)
  n = 0.465209
FEATURE [App::DocumentObjectGroupPython] Si_element001  label="Si_element : 0.004"  # scripted group (container) (typed FeaturePython)
  n = 0.003973
FEATURE [App::DocumentObjectGroupPython] G4_C_552  label="G4_C-552"  # scripted group (container) (typed FeaturePython)
  Dunit = g/cm3
  Dvalue = 1.76
  Group = -> [H_element020,C_element021,O_element019,F_element004,Si_element001]
  conduct = 2
  density = 1
  expand = 3
  formula = G4_C-552
  name = G4_C-552
  specific = 4
FEATURE [App::DocumentObjectGroupPython] Cd_element001  label="Cd_element : 1"  # scripted group (container) (typed FeaturePython)
  n = 1
  ref = Cd_element
FEATURE [App::DocumentObjectGroupPython] Te_element001  label="Te_element : 1"  # scripted group (container) (typed FeaturePython)
  n = 1
  ref = Te_element
FEATURE [App::DocumentObjectGroupPython] G4_CADMIUM_TELLURIDE  # scripted group (container) (typed FeaturePython)
  Dunit = g/cm3
  Dvalue = 6.2
  Group = -> [Cd_element001,Te_element001]
  conduct = 2
  density = 1
  expand = 3
  formula = G4_CADMIUM_TELLURIDE
  name = G4_CADMIUM_TELLURIDE
  specific = 4
FEATURE [App::DocumentObjectGroupPython] Cd_element002  label="Cd_element : 002"  # scripted group (container) (typed FeaturePython)
  n = 1
  ref = Cd_element
FEATURE [App::DocumentObjectGroupPython] W_element001  label="W_element : 1"  # scripted group (container) (typed FeaturePython)
  n = 1
  ref = W_element
FEATURE [App::DocumentObjectGroupPython] O_element020  label="O_element : 008"  # scripted group (container) (typed FeaturePython)
  n = 4
  ref = O_element
FEATURE [App::DocumentObjectGroupPython] G4_CADMIUM_TUNGSTATE  # scripted group (container) (typed FeaturePython)
  Dunit = g/cm3
  Dvalue = 7.9
  Group = -> [Cd_element002,W_element001,O_element020]
  conduct = 2
  density = 1
  expand = 3
  formula = G4_CADMIUM_TUNGSTATE
  name = G4_CADMIUM_TUNGSTATE
  specific = 4
FEATURE [App::DocumentObjectGroupPython] Ca_element005  label="Ca_element : 1"  # scripted group (container) (typed FeaturePython)
  n = 1
  ref = Ca_element
FEATURE [App::DocumentObjectGroupPython] C_element022  label="C_element : 009"  # scripted group (container) (typed FeaturePython)
  n = 1
  ref = C_element
FEATURE [App::DocumentObjectGroupPython] O_element021  label="O_element : 009"  # scripted group (container) (typed FeaturePython)
  n = 3
  ref = O_element
FEATURE [App::DocumentObjectGroupPython] G4_CALCIUM_CARBONATE  # scripted group (container) (typed FeaturePython)
  Dunit = g/cm3
  Dvalue = 2.8
  Group = -> [Ca_element005,C_element022,O_element021]
  conduct = 2
  density = 1
  expand = 3
  formula = G4_CALCIUM_CARBONATE
  name = G4_CALCIUM_CARBONATE
  specific = 4
FEATURE [App::DocumentObjectGroupPython] Ca_element006  label="Ca_element : 002"  # scripted group (container) (typed FeaturePython)
  n = 1
  ref = Ca_element
FEATURE [App::DocumentObjectGroupPython] F_element005  label="F_element : 003"  # scripted group (container) (typed FeaturePython)
  n = 2
  ref = F_element
FEATURE [App::DocumentObjectGroupPython] G4_CALCIUM_FLUORIDE  # scripted group (container) (typed FeaturePython)
  Dunit = g/cm3
  Dvalue = 3.18
  Group = -> [Ca_element006,F_element005]
  conduct = 2
  density = 1
  expand = 3
  formula = G4_CALCIUM_FLUORIDE
  name = G4_CALCIUM_FLUORIDE
  specific = 4
FEATURE [App::DocumentObjectGroupPython] Ca_element007  label="Ca_element : 003"  # scripted group (container) (typed FeaturePython)
  n = 1
  ref = Ca_element
FEATURE [App::DocumentObjectGroupPython] O_element022  label="O_element : 010"  # scripted group (container) (typed FeaturePython)
  n = 1
  ref = O_element
FEATURE [App::DocumentObjectGroupPython] G4_CALCIUM_OXIDE  # scripted group (container) (typed FeaturePython)
  Dunit = g/cm3
  Dvalue = 3.3
  Group = -> [Ca_element007,O_element022]
  conduct = 2
  density = 1
  expand = 3
  formula = G4_CALCIUM_OXIDE
  name = G4_CALCIUM_OXIDE
  specific = 4
FEATURE [App::DocumentObjectGroupPython] Ca_element008  label="Ca_element : 004"  # scripted group (container) (typed FeaturePython)
  n = 1
  ref = Ca_element
FEATURE [App::DocumentObjectGroupPython] S_element007  label="S_element : 002"  # scripted group (container) (typed FeaturePython)
  n = 1
  ref = S_element
FEATURE [App::DocumentObjectGroupPython] O_element023  label="O_element : 011"  # scripted group (container) (typed FeaturePython)
  n = 4
  ref = O_element
FEATURE [App::DocumentObjectGroupPython] G4_CALCIUM_SULFATE  # scripted group (container) (typed FeaturePython)
  Dunit = g/cm3
  Dvalue = 2.96
  Group = -> [Ca_element008,S_element007,O_element023]
  conduct = 2
  density = 1
  expand = 3
  formula = G4_CALCIUM_SULFATE
  name = G4_CALCIUM_SULFATE
  specific = 4
FEATURE [App::DocumentObjectGroupPython] Ca_element009  label="Ca_element : 005"  # scripted group (container) (typed FeaturePython)
  n = 1
  ref = Ca_element
FEATURE [App::DocumentObjectGroupPython] W_element002  label="W_element : 002"  # scripted group (container) (typed FeaturePython)
  n = 1
  ref = W_element
FEATURE [App::DocumentObjectGroupPython] O_element024  label="O_element : 012"  # scripted group (container) (typed FeaturePython)
  n = 4
  ref = O_element
FEATURE [App::DocumentObjectGroupPython] G4_CALCIUM_TUNGSTATE  # scripted group (container) (typed FeaturePython)
  Dunit = g/cm3
  Dvalue = 6.062
  Group = -> [Ca_element009,W_element002,O_element024]
  conduct = 2
  density = 1
  expand = 3
  formula = G4_CALCIUM_TUNGSTATE
  name = G4_CALCIUM_TUNGSTATE
  specific = 4
FEATURE [App::DocumentObjectGroupPython] C_element023  label="C_element : 010"  # scripted group (container) (typed FeaturePython)
  n = 1
  ref = C_element
FEATURE [App::DocumentObjectGroupPython] O_element025  label="O_element : 013"  # scripted group (container) (typed FeaturePython)
  n = 2
  ref = O_element
FEATURE [App::DocumentObjectGroupPython] G4_CARBON_DIOXIDE  # scripted group (container) (typed FeaturePython)
  Dunit = g/cm3
  Dvalue = 0.00184212
  Group = -> [C_element023,O_element025]
  conduct = 2
  density = 1
  expand = 3
  formula = G4_CARBON_DIOXIDE
  name = G4_CARBON_DIOXIDE
  specific = 4
FEATURE [App::DocumentObjectGroupPython] C_element024  label="C_element : 011"  # scripted group (container) (typed FeaturePython)
  n = 1
  ref = C_element
FEATURE [App::DocumentObjectGroupPython] Cl_element004  label="Cl_element : 4"  # scripted group (container) (typed FeaturePython)
  n = 4
  ref = Cl_element
FEATURE [App::DocumentObjectGroupPython] G4_CARBON_TETRACHLORIDE  # scripted group (container) (typed FeaturePython)
  Dunit = g/cm3
  Dvalue = 1.594
  Group = -> [C_element024,Cl_element004]
  conduct = 2
  density = 1
  expand = 3
  formula = G4_CARBON_TETRACHLORIDE
  name = G4_CARBON_TETRACHLORIDE
  specific = 4
FEATURE [App::DocumentObjectGroupPython] C_element025  label="C_element : 012"  # scripted group (container) (typed FeaturePython)
  n = 6
  ref = C_element
FEATURE [App::DocumentObjectGroupPython] H_element021  label="H_element : 012"  # scripted group (container) (typed FeaturePython)
  n = 10
  ref = H_element
FEATURE [App::DocumentObjectGroupPython] O_element026  label="O_element : 5"  # scripted group (container) (typed FeaturePython)
  n = 5
  ref = O_element
FEATURE [App::DocumentObjectGroupPython] G4_CELLULOSE_CELLOPHANE  # scripted group (container) (typed FeaturePython)
  Dunit = g/cm3
  Dvalue = 1.42
  Group = -> [C_element025,H_element021,O_element026]
  conduct = 2
  density = 1
  expand = 3
  formula = G4_CELLULOSE_CELLOPHANE
  name = G4_CELLULOSE_CELLOPHANE
  specific = 4
FEATURE [App::DocumentObjectGroupPython] H_element022  label="H_element : 0.067"  # scripted group (container) (typed FeaturePython)
  n = 0.067125
FEATURE [App::DocumentObjectGroupPython] C_element026  label="C_element : 0.545"  # scripted group (container) (typed FeaturePython)
  n = 0.545403
FEATURE [App::DocumentObjectGroupPython] O_element027  label="O_element : 0.387"  # scripted group (container) (typed FeaturePython)
  n = 0.387472
FEATURE [App::DocumentObjectGroupPython] G4_CELLULOSE_BUTYRATE  # scripted group (container) (typed FeaturePython)
  Dunit = g/cm3
  Dvalue = 1.2
  Group = -> [H_element022,C_element026,O_element027]
  conduct = 2
  density = 1
  expand = 3
  formula = G4_CELLULOSE_BUTYRATE
  name = G4_CELLULOSE_BUTYRATE
  specific = 4
FEATURE [App::DocumentObjectGroupPython] H_element023  label="H_element : 0.029"  # scripted group (container) (typed FeaturePython)
  n = 0.029216
FEATURE [App::DocumentObjectGroupPython] C_element027  label="C_element : 0.271"  # scripted group (container) (typed FeaturePython)
  n = 0.271296
FEATURE [App::DocumentObjectGroupPython] N_element013  label="N_element : 0.121"  # scripted group (container) (typed FeaturePython)
  n = 0.121276
FEATURE [App::DocumentObjectGroupPython] O_element028  label="O_element : 0.578"  # scripted group (container) (typed FeaturePython)
  n = 0.578212
FEATURE [App::DocumentObjectGroupPython] G4_CELLULOSE_NITRATE  # scripted group (container) (typed FeaturePython)
  Dunit = g/cm3
  Dvalue = 1.49
  Group = -> [H_element023,C_element027,N_element013,O_element028]
  conduct = 2
  density = 1
  expand = 3
  formula = G4_CELLULOSE_NITRATE
  name = G4_CELLULOSE_NITRATE
  specific = 4
FEATURE [App::DocumentObjectGroupPython] H_element024  label="H_element : 0.108"  # scripted group (container) (typed FeaturePython)
  n = 0.107596
FEATURE [App::DocumentObjectGroupPython] N_element014  label="N_element : 0.001"  # scripted group (container) (typed FeaturePython)
  n = 0.0008
FEATURE [App::DocumentObjectGroupPython] O_element029  label="O_element : 0.875"  # scripted group (container) (typed FeaturePython)
  n = 0.874976
FEATURE [App::DocumentObjectGroupPython] S_element008  label="S_element : 0.015"  # scripted group (container) (typed FeaturePython)
  n = 0.014627
FEATURE [App::DocumentObjectGroupPython] Ce_element001  label="Ce_element : 0.002"  # scripted group (container) (typed FeaturePython)
  n = 0.002001
FEATURE [App::DocumentObjectGroupPython] G4_CERIC_SULFATE  # scripted group (container) (typed FeaturePython)
  Dunit = g/cm3
  Dvalue = 1.03
  Group = -> [H_element024,N_element014,O_element029,S_element008,Ce_element001]
  conduct = 2
  density = 1
  expand = 3
  formula = G4_CERIC_SULFATE
  name = G4_CERIC_SULFATE
  specific = 4
FEATURE [App::DocumentObjectGroupPython] Cs_element001  label="Cs_element : 1"  # scripted group (container) (typed FeaturePython)
  n = 1
  ref = Cs_element
FEATURE [App::DocumentObjectGroupPython] F_element006  label="F_element : 1"  # scripted group (container) (typed FeaturePython)
  n = 1
  ref = F_element
FEATURE [App::DocumentObjectGroupPython] G4_CESIUM_FLUORIDE  # scripted group (container) (typed FeaturePython)
  Dunit = g/cm3
  Dvalue = 4.115
  Group = -> [Cs_element001,F_element006]
  conduct = 2
  density = 1
  expand = 3
  formula = G4_CESIUM_FLUORIDE
  name = G4_CESIUM_FLUORIDE
  specific = 4
FEATURE [App::DocumentObjectGroupPython] Cs_element002  label="Cs_element : 002"  # scripted group (container) (typed FeaturePython)
  n = 1
  ref = Cs_element
FEATURE [App::DocumentObjectGroupPython] I_element001  label="I_element : 1"  # scripted group (container) (typed FeaturePython)
  n = 1
  ref = I_element
FEATURE [App::DocumentObjectGroupPython] G4_CESIUM_IODIDE  # scripted group (container) (typed FeaturePython)
  Dunit = g/cm3
  Dvalue = 4.51
  Group = -> [Cs_element002,I_element001]
  conduct = 2
  density = 1
  expand = 3
  formula = G4_CESIUM_IODIDE
  name = G4_CESIUM_IODIDE
  specific = 4
FEATURE [App::DocumentObjectGroupPython] C_element028  label="C_element : 013"  # scripted group (container) (typed FeaturePython)
  n = 6
  ref = C_element
FEATURE [App::DocumentObjectGroupPython] H_element025  label="H_element : 013"  # scripted group (container) (typed FeaturePython)
  n = 5
  ref = H_element
FEATURE [App::DocumentObjectGroupPython] Cl_element005  label="Cl_element : 1"  # scripted group (container) (typed FeaturePython)
  n = 1
  ref = Cl_element
FEATURE [App::DocumentObjectGroupPython] G4_CHLOROBENZENE  # scripted group (container) (typed FeaturePython)
  Dunit = g/cm3
  Dvalue = 1.1058
  Group = -> [C_element028,H_element025,Cl_element005]
  conduct = 2
  density = 1
  expand = 3
  formula = G4_CHLOROBENZENE
  name = G4_CHLOROBENZENE
  specific = 4
FEATURE [App::DocumentObjectGroupPython] C_element029  label="C_element : 014"  # scripted group (container) (typed FeaturePython)
  n = 1
  ref = C_element
FEATURE [App::DocumentObjectGroupPython] H_element026  label="H_element : 1"  # scripted group (container) (typed FeaturePython)
  n = 1
  ref = H_element
FEATURE [App::DocumentObjectGroupPython] Cl_element006  label="Cl_element : 3"  # scripted group (container) (typed FeaturePython)
  n = 3
  ref = Cl_element
FEATURE [App::DocumentObjectGroupPython] G4_CHLOROFORM  # scripted group (container) (typed FeaturePython)
  Dunit = g/cm3
  Dvalue = 1.4832
  Group = -> [C_element029,H_element026,Cl_element006]
  conduct = 2
  density = 1
  expand = 3
  formula = G4_CHLOROFORM
  name = G4_CHLOROFORM
  specific = 4
FEATURE [App::DocumentObjectGroupPython] H_element027  label="H_element : 0.010"  # scripted group (container) (typed FeaturePython)
  n = 0.01
FEATURE [App::DocumentObjectGroupPython] C_element030  label="C_element : 0.001"  # scripted group (container) (typed FeaturePython)
  n = 0.001
FEATURE [App::DocumentObjectGroupPython] O_element030  label="O_element : 0.529"  # scripted group (container) (typed FeaturePython)
  n = 0.529107
FEATURE [App::DocumentObjectGroupPython] Na_element005  label="Na_element : 0.016"  # scripted group (container) (typed FeaturePython)
  n = 0.016
FEATURE [App::DocumentObjectGroupPython] Mg_element003  label="Mg_element : 0.004"  # scripted group (container) (typed FeaturePython)
  n = 0.002
FEATURE [App::DocumentObjectGroupPython] Al_element002  label="Al_element : 0.034"  # scripted group (container) (typed FeaturePython)
  n = 0.033872
FEATURE [App::DocumentObjectGroupPython] Si_element002  label="Si_element : 0.337"  # scripted group (container) (typed FeaturePython)
  n = 0.337021
FEATURE [App::DocumentObjectGroupPython] K_element003  label="K_element : 0.013"  # scripted group (container) (typed FeaturePython)
  n = 0.013
FEATURE [App::DocumentObjectGroupPython] Ca_element010  label="Ca_element : 0.044"  # scripted group (container) (typed FeaturePython)
  n = 0.044
FEATURE [App::DocumentObjectGroupPython] Fe_element002  label="Fe_element : 0.014"  # scripted group (container) (typed FeaturePython)
  n = 0.014
FEATURE [App::DocumentObjectGroupPython] G4_CONCRETE  # scripted group (container) (typed FeaturePython)
  Dunit = g/cm3
  Dvalue = 2.3
  Group = -> [H_element027,C_element030,O_element030,Na_element005,Mg_element003,Al_element002,Si_element002,K_element003,Ca_element010,Fe_element002]
  conduct = 2
  density = 1
  expand = 3
  formula = G4_CONCRETE
  name = G4_CONCRETE
  specific = 4
FEATURE [App::DocumentObjectGroupPython] C_element031  label="C_element : 015"  # scripted group (container) (typed FeaturePython)
  n = 6
  ref = C_element
FEATURE [App::DocumentObjectGroupPython] H_element028  label="H_element : 12"  # scripted group (container) (typed FeaturePython)
  n = 12
  ref = H_element
FEATURE [App::DocumentObjectGroupPython] G4_CYCLOHEXANE  # scripted group (container) (typed FeaturePython)
  Dunit = g/cm3
  Dvalue = 0.779
  Group = -> [C_element031,H_element028]
  conduct = 2
  density = 1
  expand = 3
  formula = G4_CYCLOHEXANE
  name = G4_CYCLOHEXANE
  specific = 4
FEATURE [App::DocumentObjectGroupPython] C_element032  label="C_element : 016"  # scripted group (container) (typed FeaturePython)
  n = 6
  ref = C_element
FEATURE [App::DocumentObjectGroupPython] H_element029  label="H_element : 4"  # scripted group (container) (typed FeaturePython)
  n = 4
  ref = H_element
FEATURE [App::DocumentObjectGroupPython] Cl_element007  label="Cl_element : 2"  # scripted group (container) (typed FeaturePython)
  n = 2
  ref = Cl_element
FEATURE [App::DocumentObjectGroupPython] G4_1_2_DICHLOROBENZENE  label="G4_1.2-DICHLOROBENZENE"  # scripted group (container) (typed FeaturePython)
  Dunit = g/cm3
  Dvalue = 1.3048
  Group = -> [C_element032,H_element029,Cl_element007]
  conduct = 2
  density = 1
  expand = 3
  formula = G4_1.2-DICHLOROBENZENE
  name = G4_1.2-DICHLOROBENZENE
  specific = 4
FEATURE [App::DocumentObjectGroupPython] C_element033  label="C_element : 017"  # scripted group (container) (typed FeaturePython)
  n = 4
  ref = C_element
FEATURE [App::DocumentObjectGroupPython] H_element030  label="H_element : 8"  # scripted group (container) (typed FeaturePython)
  n = 8
  ref = H_element
FEATURE [App::DocumentObjectGroupPython] O_element031  label="O_element : 014"  # scripted group (container) (typed FeaturePython)
  n = 1
  ref = O_element
FEATURE [App::DocumentObjectGroupPython] Cl_element008  label="Cl_element : 005"  # scripted group (container) (typed FeaturePython)
  n = 2
  ref = Cl_element
FEATURE [App::DocumentObjectGroupPython] G4_DICHLORODIETHYL_ETHER  # scripted group (container) (typed FeaturePython)
  Dunit = g/cm3
  Dvalue = 1.2199
  Group = -> [C_element033,H_element030,O_element031,Cl_element008]
  conduct = 2
  density = 1
  expand = 3
  formula = G4_DICHLORODIETHYL_ETHER
  name = G4_DICHLORODIETHYL_ETHER
  specific = 4
FEATURE [App::DocumentObjectGroupPython] C_element034  label="C_element : 018"  # scripted group (container) (typed FeaturePython)
  n = 2
  ref = C_element
FEATURE [App::DocumentObjectGroupPython] H_element031  label="H_element : 014"  # scripted group (container) (typed FeaturePython)
  n = 4
  ref = H_element
FEATURE [App::DocumentObjectGroupPython] Cl_element009  label="Cl_element : 006"  # scripted group (container) (typed FeaturePython)
  n = 2
  ref = Cl_element
FEATURE [App::DocumentObjectGroupPython] G4_1_2_DICHLOROETHANE  label="G4_1.2-DICHLOROETHANE"  # scripted group (container) (typed FeaturePython)
  Dunit = g/cm3
  Dvalue = 1.2351
  Group = -> [C_element034,H_element031,Cl_element009]
  conduct = 2
  density = 1
  expand = 3
  formula = G4_1.2-DICHLOROETHANE
  name = G4_1.2-DICHLOROETHANE
  specific = 4
FEATURE [App::DocumentObjectGroupPython] C_element035  label="C_element : 019"  # scripted group (container) (typed FeaturePython)
  n = 4
  ref = C_element
FEATURE [App::DocumentObjectGroupPython] H_element032  label="H_element : 015"  # scripted group (container) (typed FeaturePython)
  n = 10
  ref = H_element
FEATURE [App::DocumentObjectGroupPython] O_element032  label="O_element : 015"  # scripted group (container) (typed FeaturePython)
  n = 1
  ref = O_element
FEATURE [App::DocumentObjectGroupPython] G4_DIETHYL_ETHER  # scripted group (container) (typed FeaturePython)
  Dunit = g/cm3
  Dvalue = 0.71378
  Group = -> [C_element035,H_element032,O_element032]
  conduct = 2
  density = 1
  expand = 3
  formula = G4_DIETHYL_ETHER
  name = G4_DIETHYL_ETHER
  specific = 4
FEATURE [App::DocumentObjectGroupPython] C_element036  label="C_element : 020"  # scripted group (container) (typed FeaturePython)
  n = 3
  ref = C_element
FEATURE [App::DocumentObjectGroupPython] H_element033  label="H_element : 016"  # scripted group (container) (typed FeaturePython)
  n = 7
  ref = H_element
FEATURE [App::DocumentObjectGroupPython] N_element015  label="N_element : 008"  # scripted group (container) (typed FeaturePython)
  n = 1
  ref = N_element
FEATURE [App::DocumentObjectGroupPython] O_element033  label="O_element : 016"  # scripted group (container) (typed FeaturePython)
  n = 1
  ref = O_element
FEATURE [App::DocumentObjectGroupPython] G4_N_N_DIMETHYL_FORMAMIDE  label="G4_N.N-DIMETHYL_FORMAMIDE"  # scripted group (container) (typed FeaturePython)
  Dunit = g/cm3
  Dvalue = 0.9487
  Group = -> [C_element036,H_element033,N_element015,O_element033]
  conduct = 2
  density = 1
  expand = 3
  formula = G4_N.N-DIMETHYL_FORMAMIDE
  name = G4_N.N-DIMETHYL_FORMAMIDE
  specific = 4
FEATURE [App::DocumentObjectGroupPython] C_element037  label="C_element : 021"  # scripted group (container) (typed FeaturePython)
  n = 2
  ref = C_element
FEATURE [App::DocumentObjectGroupPython] H_element034  label="H_element : 017"  # scripted group (container) (typed FeaturePython)
  n = 6
  ref = H_element
FEATURE [App::DocumentObjectGroupPython] O_element034  label="O_element : 017"  # scripted group (container) (typed FeaturePython)
  n = 1
  ref = O_element
FEATURE [App::DocumentObjectGroupPython] S_element009  label="S_element : 003"  # scripted group (container) (typed FeaturePython)
  n = 1
  ref = S_element
FEATURE [App::DocumentObjectGroupPython] G4_DIMETHYL_SULFOXIDE  # scripted group (container) (typed FeaturePython)
  Dunit = g/cm3
  Dvalue = 1.1014
  Group = -> [C_element037,H_element034,O_element034,S_element009]
  conduct = 2
  density = 1
  expand = 3
  formula = G4_DIMETHYL_SULFOXIDE
  name = G4_DIMETHYL_SULFOXIDE
  specific = 4
FEATURE [App::DocumentObjectGroupPython] C_element038  label="C_element : 022"  # scripted group (container) (typed FeaturePython)
  n = 2
  ref = C_element
FEATURE [App::DocumentObjectGroupPython] H_element035  label="H_element : 018"  # scripted group (container) (typed FeaturePython)
  n = 6
  ref = H_element
FEATURE [App::DocumentObjectGroupPython] G4_ETHANE  # scripted group (container) (typed FeaturePython)
  Dunit = g/cm3
  Dvalue = 0.00125324
  Group = -> [C_element038,H_element035]
  conduct = 2
  density = 1
  expand = 3
  formula = G4_ETHANE
  name = G4_ETHANE
  specific = 4
FEATURE [App::DocumentObjectGroupPython] C_element039  label="C_element : 023"  # scripted group (container) (typed FeaturePython)
  n = 2
  ref = C_element
FEATURE [App::DocumentObjectGroupPython] H_element036  label="H_element : 019"  # scripted group (container) (typed FeaturePython)
  n = 6
  ref = H_element
FEATURE [App::DocumentObjectGroupPython] O_element035  label="O_element : 018"  # scripted group (container) (typed FeaturePython)
  n = 1
  ref = O_element
FEATURE [App::DocumentObjectGroupPython] G4_ETHYL_ALCOHOL  # scripted group (container) (typed FeaturePython)
  Dunit = g/cm3
  Dvalue = 0.7893
  Group = -> [C_element039,H_element036,O_element035]
  conduct = 2
  density = 1
  expand = 3
  formula = G4_ETHYL_ALCOHOL
  name = G4_ETHYL_ALCOHOL
  specific = 4
FEATURE [App::DocumentObjectGroupPython] H_element037  label="H_element : 0.090"  # scripted group (container) (typed FeaturePython)
  n = 0.090027
FEATURE [App::DocumentObjectGroupPython] C_element040  label="C_element : 0.585"  # scripted group (container) (typed FeaturePython)
  n = 0.585182
FEATURE [App::DocumentObjectGroupPython] O_element036  label="O_element : 0.325"  # scripted group (container) (typed FeaturePython)
  n = 0.324791
FEATURE [App::DocumentObjectGroupPython] G4_ETHYL_CELLULOSE  # scripted group (container) (typed FeaturePython)
  Dunit = g/cm3
  Dvalue = 1.13
  Group = -> [H_element037,C_element040,O_element036]
  conduct = 2
  density = 1
  expand = 3
  formula = G4_ETHYL_CELLULOSE
  name = G4_ETHYL_CELLULOSE
  specific = 4
FEATURE [App::DocumentObjectGroupPython] C_element041  label="C_element : 024"  # scripted group (container) (typed FeaturePython)
  n = 2
  ref = C_element
FEATURE [App::DocumentObjectGroupPython] H_element038  label="H_element : 020"  # scripted group (container) (typed FeaturePython)
  n = 4
  ref = H_element
FEATURE [App::DocumentObjectGroupPython] G4_ETHYLENE  # scripted group (container) (typed FeaturePython)
  Dunit = g/cm3
  Dvalue = 0.00117497
  Group = -> [C_element041,H_element038]
  conduct = 2
  density = 1
  expand = 3
  formula = G4_ETHYLENE
  name = G4_ETHYLENE
  specific = 4
FEATURE [App::DocumentObjectGroupPython] H_element039  label="H_element : 0.096"  # scripted group (container) (typed FeaturePython)
  n = 0.096
FEATURE [App::DocumentObjectGroupPython] C_element042  label="C_element : 0.195"  # scripted group (container) (typed FeaturePython)
  n = 0.195
FEATURE [App::DocumentObjectGroupPython] N_element016  label="N_element : 0.057"  # scripted group (container) (typed FeaturePython)
  n = 0.057
FEATURE [App::DocumentObjectGroupPython] O_element037  label="O_element : 0.646"  # scripted group (container) (typed FeaturePython)
  n = 0.646
FEATURE [App::DocumentObjectGroupPython] Na_element006  label="Na_element : 0.017"  # scripted group (container) (typed FeaturePython)
  n = 0.001
FEATURE [App::DocumentObjectGroupPython] P_element005  label="P_element : 0.104"  # scripted group (container) (typed FeaturePython)
  n = 0.001
FEATURE [App::DocumentObjectGroupPython] S_element010  label="S_element : 0.016"  # scripted group (container) (typed FeaturePython)
  n = 0.003
FEATURE [App::DocumentObjectGroupPython] Cl_element010  label="Cl_element : 0.005"  # scripted group (container) (typed FeaturePython)
  n = 0.001
FEATURE [App::DocumentObjectGroupPython] G4_EYE_LENS_ICRP  # scripted group (container) (typed FeaturePython)
  Dunit = g/cm3
  Dvalue = 1.07
  Group = -> [H_element039,C_element042,N_element016,O_element037,Na_element006,P_element005,S_element010,Cl_element010]
  conduct = 2
  density = 1
  expand = 3
  formula = G4_EYE_LENS_ICRP
  name = G4_EYE_LENS_ICRP
  specific = 4
FEATURE [App::DocumentObjectGroupPython] Fe_element003  label="Fe_element : 2"  # scripted group (container) (typed FeaturePython)
  n = 2
  ref = Fe_element
FEATURE [App::DocumentObjectGroupPython] O_element038  label="O_element : 019"  # scripted group (container) (typed FeaturePython)
  n = 3
  ref = O_element
FEATURE [App::DocumentObjectGroupPython] G4_FERRIC_OXIDE  # scripted group (container) (typed FeaturePython)
  Dunit = g/cm3
  Dvalue = 5.2
  Group = -> [Fe_element003,O_element038]
  conduct = 2
  density = 1
  expand = 3
  formula = G4_FERRIC_OXIDE
  name = G4_FERRIC_OXIDE
  specific = 4
FEATURE [App::DocumentObjectGroupPython] Fe_element004  label="Fe_element : 1"  # scripted group (container) (typed FeaturePython)
  n = 1
  ref = Fe_element
FEATURE [App::DocumentObjectGroupPython] B_element003  label="B_element : 1"  # scripted group (container) (typed FeaturePython)
  n = 1
  ref = B_element
FEATURE [App::DocumentObjectGroupPython] G4_FERROBORIDE  # scripted group (container) (typed FeaturePython)
  Dunit = g/cm3
  Dvalue = 7.15
  Group = -> [Fe_element004,B_element003]
  conduct = 2
  density = 1
  expand = 3
  formula = G4_FERROBORIDE
  name = G4_FERROBORIDE
  specific = 4
FEATURE [App::DocumentObjectGroupPython] Fe_element005  label="Fe_element : 003"  # scripted group (container) (typed FeaturePython)
  n = 1
  ref = Fe_element
FEATURE [App::DocumentObjectGroupPython] O_element039  label="O_element : 020"  # scripted group (container) (typed FeaturePython)
  n = 1
  ref = O_element
FEATURE [App::DocumentObjectGroupPython] G4_FERROUS_OXIDE  # scripted group (container) (typed FeaturePython)
  Dunit = g/cm3
  Dvalue = 5.7
  Group = -> [Fe_element005,O_element039]
  conduct = 2
  density = 1
  expand = 3
  formula = G4_FERROUS_OXIDE
  name = G4_FERROUS_OXIDE
  specific = 4
FEATURE [App::DocumentObjectGroupPython] H_element040  label="H_element : 0.115"  # scripted group (container) (typed FeaturePython)
  n = 0.108259
FEATURE [App::DocumentObjectGroupPython] N_element017  label="N_element : 0.000"  # scripted group (container) (typed FeaturePython)
  n = 2.7e-05
FEATURE [App::DocumentObjectGroupPython] O_element040  label="O_element : 0.879"  # scripted group (container) (typed FeaturePython)
  n = 0.878636
FEATURE [App::DocumentObjectGroupPython] Na_element007  label="Na_element : 0.000"  # scripted group (container) (typed FeaturePython)
  n = 2.2e-05
FEATURE [App::DocumentObjectGroupPython] S_element011  label="S_element : 0.013"  # scripted group (container) (typed FeaturePython)
  n = 0.012968
FEATURE [App::DocumentObjectGroupPython] Cl_element011  label="Cl_element : 0.000"  # scripted group (container) (typed FeaturePython)
  n = 3.4e-05
FEATURE [App::DocumentObjectGroupPython] Fe_element006  label="Fe_element : 0.000"  # scripted group (container) (typed FeaturePython)
  n = 5.4e-05
FEATURE [App::DocumentObjectGroupPython] G4_FERROUS_SULFATE  # scripted group (container) (typed FeaturePython)
  Dunit = g/cm3
  Dvalue = 1.024
  Group = -> [H_element040,N_element017,O_element040,Na_element007,S_element011,Cl_element011,Fe_element006]
  conduct = 2
  density = 1
  expand = 3
  formula = G4_FERROUS_SULFATE
  name = G4_FERROUS_SULFATE
  specific = 4
FEATURE [App::DocumentObjectGroupPython] C_element043  label="C_element : 0.099"  # scripted group (container) (typed FeaturePython)
  n = 0.099335
FEATURE [App::DocumentObjectGroupPython] F_element007  label="F_element : 0.314"  # scripted group (container) (typed FeaturePython)
  n = 0.314247
FEATURE [App::DocumentObjectGroupPython] Cl_element012  label="Cl_element : 0.586"  # scripted group (container) (typed FeaturePython)
  n = 0.586418
FEATURE [App::DocumentObjectGroupPython] G4_FREON_12  label="G4_FREON-12"  # scripted group (container) (typed FeaturePython)
  Dunit = g/cm3
  Dvalue = 1.12
  Group = -> [C_element043,F_element007,Cl_element012]
  conduct = 2
  density = 1
  expand = 3
  formula = G4_FREON-12
  name = G4_FREON-12
  specific = 4
FEATURE [App::DocumentObjectGroupPython] C_element044  label="C_element : 0.057"  # scripted group (container) (typed FeaturePython)
  n = 0.057245
FEATURE [App::DocumentObjectGroupPython] F_element008  label="F_element : 0.181"  # scripted group (container) (typed FeaturePython)
  n = 0.181096
FEATURE [App::DocumentObjectGroupPython] Br_element001  label="Br_element : 0.762"  # scripted group (container) (typed FeaturePython)
  n = 0.761659
FEATURE [App::DocumentObjectGroupPython] G4_FREON_12B2  label="G4_FREON-12B2"  # scripted group (container) (typed FeaturePython)
  Dunit = g/cm3
  Dvalue = 1.8
  Group = -> [C_element044,F_element008,Br_element001]
  conduct = 2
  density = 1
  expand = 3
  formula = G4_FREON-12B2
  name = G4_FREON-12B2
  specific = 4
FEATURE [App::DocumentObjectGroupPython] C_element045  label="C_element : 0.115"  # scripted group (container) (typed FeaturePython)
  n = 0.114983
FEATURE [App::DocumentObjectGroupPython] F_element009  label="F_element : 0.546"  # scripted group (container) (typed FeaturePython)
  n = 0.545621
FEATURE [App::DocumentObjectGroupPython] Cl_element013  label="Cl_element : 0.339"  # scripted group (container) (typed FeaturePython)
  n = 0.339396
FEATURE [App::DocumentObjectGroupPython] G4_FREON_13  label="G4_FREON-13"  # scripted group (container) (typed FeaturePython)
  Dunit = g/cm3
  Dvalue = 0.95
  Group = -> [C_element045,F_element009,Cl_element013]
  conduct = 2
  density = 1
  expand = 3
  formula = G4_FREON-13
  name = G4_FREON-13
  specific = 4
FEATURE [App::DocumentObjectGroupPython] C_element046  label="C_element : 025"  # scripted group (container) (typed FeaturePython)
  n = 1
  ref = C_element
FEATURE [App::DocumentObjectGroupPython] F_element010  label="F_element : 3"  # scripted group (container) (typed FeaturePython)
  n = 3
  ref = F_element
FEATURE [App::DocumentObjectGroupPython] Br_element002  label="Br_element : 1"  # scripted group (container) (typed FeaturePython)
  n = 1
  ref = Br_element
FEATURE [App::DocumentObjectGroupPython] G4_FREON_13B1  label="G4_FREON-13B1"  # scripted group (container) (typed FeaturePython)
  Dunit = g/cm3
  Dvalue = 1.5
  Group = -> [C_element046,F_element010,Br_element002]
  conduct = 2
  density = 1
  expand = 3
  formula = G4_FREON-13B1
  name = G4_FREON-13B1
  specific = 4
FEATURE [App::DocumentObjectGroupPython] C_element047  label="C_element : 0.061"  # scripted group (container) (typed FeaturePython)
  n = 0.061309
FEATURE [App::DocumentObjectGroupPython] F_element011  label="F_element : 0.291"  # scripted group (container) (typed FeaturePython)
  n = 0.290924
FEATURE [App::DocumentObjectGroupPython] I_element002  label="I_element : 0.648"  # scripted group (container) (typed FeaturePython)
  n = 0.647767
FEATURE [App::DocumentObjectGroupPython] G4_FREON_13I1  label="G4_FREON-13I1"  # scripted group (container) (typed FeaturePython)
  Dunit = g/cm3
  Dvalue = 1.8
  Group = -> [C_element047,F_element011,I_element002]
  conduct = 2
  density = 1
  expand = 3
  formula = G4_FREON-13I1
  name = G4_FREON-13I1
  specific = 4
FEATURE [App::DocumentObjectGroupPython] Gd_element001  label="Gd_element : 2"  # scripted group (container) (typed FeaturePython)
  n = 2
  ref = Gd_element
FEATURE [App::DocumentObjectGroupPython] O_element041  label="O_element : 021"  # scripted group (container) (typed FeaturePython)
  n = 2
  ref = O_element
FEATURE [App::DocumentObjectGroupPython] S_element012  label="S_element : 004"  # scripted group (container) (typed FeaturePython)
  n = 1
  ref = S_element
FEATURE [App::DocumentObjectGroupPython] G4_GADOLINIUM_OXYSULFIDE  # scripted group (container) (typed FeaturePython)
  Dunit = g/cm3
  Dvalue = 7.44
  Group = -> [Gd_element001,O_element041,S_element012]
  conduct = 2
  density = 1
  expand = 3
  formula = G4_GADOLINIUM_OXYSULFIDE
  name = G4_GADOLINIUM_OXYSULFIDE
  specific = 4
FEATURE [App::DocumentObjectGroupPython] Ga_element001  label="Ga_element : 1"  # scripted group (container) (typed FeaturePython)
  n = 1
  ref = Ga_element
FEATURE [App::DocumentObjectGroupPython] As_element001  label="As_element : 1"  # scripted group (container) (typed FeaturePython)
  n = 1
  ref = As_element
FEATURE [App::DocumentObjectGroupPython] G4_GALLIUM_ARSENIDE  # scripted group (container) (typed FeaturePython)
  Dunit = g/cm3
  Dvalue = 5.31
  Group = -> [Ga_element001,As_element001]
  conduct = 2
  density = 1
  expand = 3
  formula = G4_GALLIUM_ARSENIDE
  name = G4_GALLIUM_ARSENIDE
  specific = 4
FEATURE [App::DocumentObjectGroupPython] H_element041  label="H_element : 0.081"  # scripted group (container) (typed FeaturePython)
  n = 0.08118
FEATURE [App::DocumentObjectGroupPython] C_element048  label="C_element : 0.416"  # scripted group (container) (typed FeaturePython)
  n = 0.41606
FEATURE [App::DocumentObjectGroupPython] N_element018  label="N_element : 0.111"  # scripted group (container) (typed FeaturePython)
  n = 0.11124
FEATURE [App::DocumentObjectGroupPython] O_element042  label="O_element : 0.381"  # scripted group (container) (typed FeaturePython)
  n = 0.38064
FEATURE [App::DocumentObjectGroupPython] S_element013  label="S_element : 0.011"  # scripted group (container) (typed FeaturePython)
  n = 0.01088
FEATURE [App::DocumentObjectGroupPython] G4_GEL_PHOTO_EMULSION  # scripted group (container) (typed FeaturePython)
  Dunit = g/cm3
  Dvalue = 1.2914
  Group = -> [H_element041,C_element048,N_element018,O_element042,S_element013]
  conduct = 2
  density = 1
  expand = 3
  formula = G4_GEL_PHOTO_EMULSION
  name = G4_GEL_PHOTO_EMULSION
  specific = 4
FEATURE [App::DocumentObjectGroupPython] B_element004  label="B_element : 0.040"  # scripted group (container) (typed FeaturePython)
  n = 0.0400639
FEATURE [App::DocumentObjectGroupPython] O_element043  label="O_element : 0.540"  # scripted group (container) (typed FeaturePython)
  n = 0.539561
FEATURE [App::DocumentObjectGroupPython] Na_element008  label="Na_element : 0.028"  # scripted group (container) (typed FeaturePython)
  n = 0.0281909
FEATURE [App::DocumentObjectGroupPython] Al_element003  label="Al_element : 0.012"  # scripted group (container) (typed FeaturePython)
  n = 0.011644
FEATURE [App::DocumentObjectGroupPython] Si_element003  label="Si_element : 0.377"  # scripted group (container) (typed FeaturePython)
  n = 0.377219
FEATURE [App::DocumentObjectGroupPython] K_element004  label="K_element : 0.014"  # scripted group (container) (typed FeaturePython)
  n = 0.00332099
FEATURE [App::DocumentObjectGroupPython] G4_Pyrex_Glass  # scripted group (container) (typed FeaturePython)
  Dunit = g/cm3
  Dvalue = 2.23
  Group = -> [B_element004,O_element043,Na_element008,Al_element003,Si_element003,K_element004]
  conduct = 2
  density = 1
  expand = 3
  formula = G4_Pyrex_Glass
  name = G4_Pyrex_Glass
  specific = 4
FEATURE [App::DocumentObjectGroupPython] O_element044  label="O_element : 0.156"  # scripted group (container) (typed FeaturePython)
  n = 0.156453
FEATURE [App::DocumentObjectGroupPython] Si_element004  label="Si_element : 0.081"  # scripted group (container) (typed FeaturePython)
  n = 0.080866
FEATURE [App::DocumentObjectGroupPython] Ti_element001  label="Ti_element : 0.008"  # scripted group (container) (typed FeaturePython)
  n = 0.008092
FEATURE [App::DocumentObjectGroupPython] As_element002  label="As_element : 0.003"  # scripted group (container) (typed FeaturePython)
  n = 0.002651
FEATURE [App::DocumentObjectGroupPython] Pb_element001  label="Pb_element : 0.752"  # scripted group (container) (typed FeaturePython)
  n = 0.751938
FEATURE [App::DocumentObjectGroupPython] G4_GLASS_LEAD  # scripted group (container) (typed FeaturePython)
  Dunit = g/cm3
  Dvalue = 6.22
  Group = -> [O_element044,Si_element004,Ti_element001,As_element002,Pb_element001]
  conduct = 2
  density = 1
  expand = 3
  formula = G4_GLASS_LEAD
  name = G4_GLASS_LEAD
  specific = 4
FEATURE [App::DocumentObjectGroupPython] O_element045  label="O_element : 0.460"  # scripted group (container) (typed FeaturePython)
  n = 0.4598
FEATURE [App::DocumentObjectGroupPython] Na_element009  label="Na_element : 0.096"  # scripted group (container) (typed FeaturePython)
  n = 0.0964411
FEATURE [App::DocumentObjectGroupPython] Si_element005  label="Si_element : 0.378"  # scripted group (container) (typed FeaturePython)
  n = 0.336553
FEATURE [App::DocumentObjectGroupPython] Ca_element011  label="Ca_element : 0.107"  # scripted group (container) (typed FeaturePython)
  n = 0.107205
FEATURE [App::DocumentObjectGroupPython] G4_GLASS_PLATE  # scripted group (container) (typed FeaturePython)
  Dunit = g/cm3
  Dvalue = 2.4
  Group = -> [O_element045,Na_element009,Si_element005,Ca_element011]
  conduct = 2
  density = 1
  expand = 3
  formula = G4_GLASS_PLATE
  name = G4_GLASS_PLATE
  specific = 4
FEATURE [App::DocumentObjectGroupPython] C_element049  label="C_element : 026"  # scripted group (container) (typed FeaturePython)
  n = 5
  ref = C_element
FEATURE [App::DocumentObjectGroupPython] H_element042  label="H_element : 021"  # scripted group (container) (typed FeaturePython)
  n = 10
  ref = H_element
FEATURE [App::DocumentObjectGroupPython] N_element019  label="N_element : 2"  # scripted group (container) (typed FeaturePython)
  n = 2
  ref = N_element
FEATURE [App::DocumentObjectGroupPython] O_element046  label="O_element : 022"  # scripted group (container) (typed FeaturePython)
  n = 3
  ref = O_element
FEATURE [App::DocumentObjectGroupPython] G4_GLUTAMINE  # scripted group (container) (typed FeaturePython)
  Dunit = g/cm3
  Dvalue = 1.46
  Group = -> [C_element049,H_element042,N_element019,O_element046]
  conduct = 2
  density = 1
  expand = 3
  formula = G4_GLUTAMINE
  name = G4_GLUTAMINE
  specific = 4
FEATURE [App::DocumentObjectGroupPython] C_element050  label="C_element : 027"  # scripted group (container) (typed FeaturePython)
  n = 3
  ref = C_element
FEATURE [App::DocumentObjectGroupPython] H_element043  label="H_element : 022"  # scripted group (container) (typed FeaturePython)
  n = 8
  ref = H_element
FEATURE [App::DocumentObjectGroupPython] O_element047  label="O_element : 023"  # scripted group (container) (typed FeaturePython)
  n = 3
  ref = O_element
FEATURE [App::DocumentObjectGroupPython] G4_GLYCEROL  # scripted group (container) (typed FeaturePython)
  Dunit = g/cm3
  Dvalue = 1.2613
  Group = -> [C_element050,H_element043,O_element047]
  conduct = 2
  density = 1
  expand = 3
  formula = G4_GLYCEROL
  name = G4_GLYCEROL
  specific = 4
FEATURE [App::DocumentObjectGroupPython] C_element051  label="C_element : 028"  # scripted group (container) (typed FeaturePython)
  n = 5
  ref = C_element
FEATURE [App::DocumentObjectGroupPython] H_element044  label="H_element : 023"  # scripted group (container) (typed FeaturePython)
  n = 5
  ref = H_element
FEATURE [App::DocumentObjectGroupPython] N_element020  label="N_element : 009"  # scripted group (container) (typed FeaturePython)
  n = 5
  ref = N_element
FEATURE [App::DocumentObjectGroupPython] O_element048  label="O_element : 024"  # scripted group (container) (typed FeaturePython)
  n = 1
  ref = O_element
FEATURE [App::DocumentObjectGroupPython] G4_GUANINE  # scripted group (container) (typed FeaturePython)
  Dunit = g/cm3
  Dvalue = 2.2
  Group = -> [C_element051,H_element044,N_element020,O_element048]
  conduct = 2
  density = 1
  expand = 3
  formula = G4_GUANINE
  name = G4_GUANINE
  specific = 4
FEATURE [App::DocumentObjectGroupPython] Ca_element012  label="Ca_element : 006"  # scripted group (container) (typed FeaturePython)
  n = 1
  ref = Ca_element
FEATURE [App::DocumentObjectGroupPython] S_element014  label="S_element : 005"  # scripted group (container) (typed FeaturePython)
  n = 1
  ref = S_element
FEATURE [App::DocumentObjectGroupPython] O_element049  label="O_element : 6"  # scripted group (container) (typed FeaturePython)
  n = 6
  ref = O_element
FEATURE [App::DocumentObjectGroupPython] H_element045  label="H_element : 024"  # scripted group (container) (typed FeaturePython)
  n = 4
  ref = H_element
FEATURE [App::DocumentObjectGroupPython] G4_GYPSUM  # scripted group (container) (typed FeaturePython)
  Dunit = g/cm3
  Dvalue = 2.32
  Group = -> [Ca_element012,S_element014,O_element049,H_element045]
  conduct = 2
  density = 1
  expand = 3
  formula = G4_GYPSUM
  name = G4_GYPSUM
  specific = 4
FEATURE [App::DocumentObjectGroupPython] C_element052  label="C_element : 7"  # scripted group (container) (typed FeaturePython)
  n = 7
  ref = C_element
FEATURE [App::DocumentObjectGroupPython] H_element046  label="H_element : 16"  # scripted group (container) (typed FeaturePython)
  n = 16
  ref = H_element
FEATURE [App::DocumentObjectGroupPython] G4_N_HEPTANE  label="G4_N-HEPTANE"  # scripted group (container) (typed FeaturePython)
  Dunit = g/cm3
  Dvalue = 0.68376
  Group = -> [C_element052,H_element046]
  conduct = 2
  density = 1
  expand = 3
  formula = G4_N-HEPTANE
  name = G4_N-HEPTANE
  specific = 4
FEATURE [App::DocumentObjectGroupPython] C_element053  label="C_element : 029"  # scripted group (container) (typed FeaturePython)
  n = 6
  ref = C_element
FEATURE [App::DocumentObjectGroupPython] H_element047  label="H_element : 14"  # scripted group (container) (typed FeaturePython)
  n = 14
  ref = H_element
FEATURE [App::DocumentObjectGroupPython] G4_N_HEXANE  label="G4_N-HEXANE"  # scripted group (container) (typed FeaturePython)
  Dunit = g/cm3
  Dvalue = 0.6603
  Group = -> [C_element053,H_element047]
  conduct = 2
  density = 1
  expand = 3
  formula = G4_N-HEXANE
  name = G4_N-HEXANE
  specific = 4
FEATURE [App::DocumentObjectGroupPython] C_element054  label="C_element : 22"  # scripted group (container) (typed FeaturePython)
  n = 22
  ref = C_element
FEATURE [App::DocumentObjectGroupPython] H_element048  label="H_element : 025"  # scripted group (container) (typed FeaturePython)
  n = 10
  ref = H_element
FEATURE [App::DocumentObjectGroupPython] N_element021  label="N_element : 010"  # scripted group (container) (typed FeaturePython)
  n = 2
  ref = N_element
FEATURE [App::DocumentObjectGroupPython] O_element050  label="O_element : 025"  # scripted group (container) (typed FeaturePython)
  n = 5
  ref = O_element
FEATURE [App::DocumentObjectGroupPython] G4_KAPTON  # scripted group (container) (typed FeaturePython)
  Dunit = g/cm3
  Dvalue = 1.42
  Group = -> [C_element054,H_element048,N_element021,O_element050]
  conduct = 2
  density = 1
  expand = 3
  formula = G4_KAPTON
  name = G4_KAPTON
  specific = 4
FEATURE [App::DocumentObjectGroupPython] La_element001  label="La_element : 1"  # scripted group (container) (typed FeaturePython)
  n = 1
  ref = La_element
FEATURE [App::DocumentObjectGroupPython] Br_element003  label="Br_element : 002"  # scripted group (container) (typed FeaturePython)
  n = 1
  ref = Br_element
FEATURE [App::DocumentObjectGroupPython] O_element051  label="O_element : 026"  # scripted group (container) (typed FeaturePython)
  n = 1
  ref = O_element
FEATURE [App::DocumentObjectGroupPython] G4_LANTHANUM_OXYBROMIDE  # scripted group (container) (typed FeaturePython)
  Dunit = g/cm3
  Dvalue = 6.28
  Group = -> [La_element001,Br_element003,O_element051]
  conduct = 2
  density = 1
  expand = 3
  formula = G4_LANTHANUM_OXYBROMIDE
  name = G4_LANTHANUM_OXYBROMIDE
  specific = 4
FEATURE [App::DocumentObjectGroupPython] La_element002  label="La_element : 2"  # scripted group (container) (typed FeaturePython)
  n = 2
  ref = La_element
FEATURE [App::DocumentObjectGroupPython] O_element052  label="O_element : 027"  # scripted group (container) (typed FeaturePython)
  n = 2
  ref = O_element
FEATURE [App::DocumentObjectGroupPython] S_element015  label="S_element : 006"  # scripted group (container) (typed FeaturePython)
  n = 1
  ref = S_element
FEATURE [App::DocumentObjectGroupPython] G4_LANTHANUM_OXYSULFIDE  # scripted group (container) (typed FeaturePython)
  Dunit = g/cm3
  Dvalue = 5.86
  Group = -> [La_element002,O_element052,S_element015]
  conduct = 2
  density = 1
  expand = 3
  formula = G4_LANTHANUM_OXYSULFIDE
  name = G4_LANTHANUM_OXYSULFIDE
  specific = 4
FEATURE [App::DocumentObjectGroupPython] O_element053  label="O_element : 0.072"  # scripted group (container) (typed FeaturePython)
  n = 0.071682
FEATURE [App::DocumentObjectGroupPython] Pb_element002  label="Pb_element : 0.928"  # scripted group (container) (typed FeaturePython)
  n = 0.928318
FEATURE [App::DocumentObjectGroupPython] G4_LEAD_OXIDE  # scripted group (container) (typed FeaturePython)
  Dunit = g/cm3
  Dvalue = 9.53
  Group = -> [O_element053,Pb_element002]
  conduct = 2
  density = 1
  expand = 3
  formula = G4_LEAD_OXIDE
  name = G4_LEAD_OXIDE
  specific = 4
FEATURE [App::DocumentObjectGroupPython] Li_element001  label="Li_element : 1"  # scripted group (container) (typed FeaturePython)
  n = 1
  ref = Li_element
FEATURE [App::DocumentObjectGroupPython] N_element022  label="N_element : 011"  # scripted group (container) (typed FeaturePython)
  n = 1
  ref = N_element
FEATURE [App::DocumentObjectGroupPython] H_element049  label="H_element : 026"  # scripted group (container) (typed FeaturePython)
  n = 2
  ref = H_element
FEATURE [App::DocumentObjectGroupPython] G4_LITHIUM_AMIDE  # scripted group (container) (typed FeaturePython)
  Dunit = g/cm3
  Dvalue = 1.178
  Group = -> [Li_element001,N_element022,H_element049]
  conduct = 2
  density = 1
  expand = 3
  formula = G4_LITHIUM_AMIDE
  name = G4_LITHIUM_AMIDE
  specific = 4
FEATURE [App::DocumentObjectGroupPython] Li_element002  label="Li_element : 2"  # scripted group (container) (typed FeaturePython)
  n = 2
  ref = Li_element
FEATURE [App::DocumentObjectGroupPython] C_element055  label="C_element : 030"  # scripted group (container) (typed FeaturePython)
  n = 1
  ref = C_element
FEATURE [App::DocumentObjectGroupPython] O_element054  label="O_element : 028"  # scripted group (container) (typed FeaturePython)
  n = 3
  ref = O_element
FEATURE [App::DocumentObjectGroupPython] G4_LITHIUM_CARBONATE  # scripted group (container) (typed FeaturePython)
  Dunit = g/cm3
  Dvalue = 2.11
  Group = -> [Li_element002,C_element055,O_element054]
  conduct = 2
  density = 1
  expand = 3
  formula = G4_LITHIUM_CARBONATE
  name = G4_LITHIUM_CARBONATE
  specific = 4
FEATURE [App::DocumentObjectGroupPython] Li_element003  label="Li_element : 003"  # scripted group (container) (typed FeaturePython)
  n = 1
  ref = Li_element
FEATURE [App::DocumentObjectGroupPython] F_element012  label="F_element : 004"  # scripted group (container) (typed FeaturePython)
  n = 1
  ref = F_element
FEATURE [App::DocumentObjectGroupPython] G4_LITHIUM_FLUORIDE  # scripted group (container) (typed FeaturePython)
  Dunit = g/cm3
  Dvalue = 2.635
  Group = -> [Li_element003,F_element012]
  conduct = 2
  density = 1
  expand = 3
  formula = G4_LITHIUM_FLUORIDE
  name = G4_LITHIUM_FLUORIDE
  specific = 4
FEATURE [App::DocumentObjectGroupPython] Li_element004  label="Li_element : 004"  # scripted group (container) (typed FeaturePython)
  n = 1
  ref = Li_element
FEATURE [App::DocumentObjectGroupPython] H_element050  label="H_element : 027"  # scripted group (container) (typed FeaturePython)
  n = 1
  ref = H_element
FEATURE [App::DocumentObjectGroupPython] G4_LITHIUM_HYDRIDE  # scripted group (container) (typed FeaturePython)
  Dunit = g/cm3
  Dvalue = 0.82
  Group = -> [Li_element004,H_element050]
  conduct = 2
  density = 1
  expand = 3
  formula = G4_LITHIUM_HYDRIDE
  name = G4_LITHIUM_HYDRIDE
  specific = 4
FEATURE [App::DocumentObjectGroupPython] Li_element005  label="Li_element : 005"  # scripted group (container) (typed FeaturePython)
  n = 1
  ref = Li_element
FEATURE [App::DocumentObjectGroupPython] I_element003  label="I_element : 002"  # scripted group (container) (typed FeaturePython)
  n = 1
  ref = I_element
FEATURE [App::DocumentObjectGroupPython] G4_LITHIUM_IODIDE  # scripted group (container) (typed FeaturePython)
  Dunit = g/cm3
  Dvalue = 3.494
  Group = -> [Li_element005,I_element003]
  conduct = 2
  density = 1
  expand = 3
  formula = G4_LITHIUM_IODIDE
  name = G4_LITHIUM_IODIDE
  specific = 4
FEATURE [App::DocumentObjectGroupPython] Li_element006  label="Li_element : 006"  # scripted group (container) (typed FeaturePython)
  n = 2
  ref = Li_element
FEATURE [App::DocumentObjectGroupPython] O_element055  label="O_element : 029"  # scripted group (container) (typed FeaturePython)
  n = 1
  ref = O_element
FEATURE [App::DocumentObjectGroupPython] G4_LITHIUM_OXIDE  # scripted group (container) (typed FeaturePython)
  Dunit = g/cm3
  Dvalue = 2.013
  Group = -> [Li_element006,O_element055]
  conduct = 2
  density = 1
  expand = 3
  formula = G4_LITHIUM_OXIDE
  name = G4_LITHIUM_OXIDE
  specific = 4
FEATURE [App::DocumentObjectGroupPython] Li_element007  label="Li_element : 007"  # scripted group (container) (typed FeaturePython)
  n = 2
  ref = Li_element
FEATURE [App::DocumentObjectGroupPython] B_element005  label="B_element : 005"  # scripted group (container) (typed FeaturePython)
  n = 4
  ref = B_element
FEATURE [App::DocumentObjectGroupPython] O_element056  label="O_element : 7"  # scripted group (container) (typed FeaturePython)
  n = 7
  ref = O_element
FEATURE [App::DocumentObjectGroupPython] G4_LITHIUM_TETRABORATE  # scripted group (container) (typed FeaturePython)
  Dunit = g/cm3
  Dvalue = 2.44
  Group = -> [Li_element007,B_element005,O_element056]
  conduct = 2
  density = 1
  expand = 3
  formula = G4_LITHIUM_TETRABORATE
  name = G4_LITHIUM_TETRABORATE
  specific = 4
FEATURE [App::DocumentObjectGroupPython] H_element051  label="H_element : 0.105"  # scripted group (container) (typed FeaturePython)
  n = 0.105
FEATURE [App::DocumentObjectGroupPython] C_element056  label="C_element : 0.083"  # scripted group (container) (typed FeaturePython)
  n = 0.083
FEATURE [App::DocumentObjectGroupPython] N_element023  label="N_element : 0.023"  # scripted group (container) (typed FeaturePython)
  n = 0.023
FEATURE [App::DocumentObjectGroupPython] O_element057  label="O_element : 0.779"  # scripted group (container) (typed FeaturePython)
  n = 0.779
FEATURE [App::DocumentObjectGroupPython] Na_element010  label="Na_element : 0.097"  # scripted group (container) (typed FeaturePython)
  n = 0.002
FEATURE [App::DocumentObjectGroupPython] P_element006  label="P_element : 0.105"  # scripted group (container) (typed FeaturePython)
  n = 0.001
FEATURE [App::DocumentObjectGroupPython] S_element016  label="S_element : 0.017"  # scripted group (container) (typed FeaturePython)
  n = 0.002
FEATURE [App::DocumentObjectGroupPython] Cl_element014  label="Cl_element : 0.587"  # scripted group (container) (typed FeaturePython)
  n = 0.003
FEATURE [App::DocumentObjectGroupPython] K_element005  label="K_element : 0.015"  # scripted group (container) (typed FeaturePython)
  n = 0.002
FEATURE [App::DocumentObjectGroupPython] G4_LUNG_ICRP  # scripted group (container) (typed FeaturePython)
  Dunit = g/cm3
  Dvalue = 1.04
  Group = -> [H_element051,C_element056,N_element023,O_element057,Na_element010,P_element006,S_element016,Cl_element014,K_element005]
  conduct = 2
  density = 1
  expand = 3
  formula = G4_LUNG_ICRP
  name = G4_LUNG_ICRP
  specific = 4
FEATURE [App::DocumentObjectGroupPython] H_element052  label="H_element : 0.116"  # scripted group (container) (typed FeaturePython)
  n = 0.114318
FEATURE [App::DocumentObjectGroupPython] C_element057  label="C_element : 0.656"  # scripted group (container) (typed FeaturePython)
  n = 0.655824
FEATURE [App::DocumentObjectGroupPython] O_element058  label="O_element : 0.092"  # scripted group (container) (typed FeaturePython)
  n = 0.0921831
FEATURE [App::DocumentObjectGroupPython] Mg_element004  label="Mg_element : 0.135"  # scripted group (container) (typed FeaturePython)
  n = 0.134792
FEATURE [App::DocumentObjectGroupPython] Ca_element013  label="Ca_element : 0.003"  # scripted group (container) (typed FeaturePython)
  n = 0.002883
FEATURE [App::DocumentObjectGroupPython] G4_M3_WAX  # scripted group (container) (typed FeaturePython)
  Dunit = g/cm3
  Dvalue = 1.05
  Group = -> [H_element052,C_element057,O_element058,Mg_element004,Ca_element013]
  conduct = 2
  density = 1
  expand = 3
  formula = G4_M3_WAX
  name = G4_M3_WAX
  specific = 4
FEATURE [App::DocumentObjectGroupPython] Mg_element005  label="Mg_element : 1"  # scripted group (container) (typed FeaturePython)
  n = 1
  ref = Mg_element
FEATURE [App::DocumentObjectGroupPython] C_element058  label="C_element : 031"  # scripted group (container) (typed FeaturePython)
  n = 1
  ref = C_element
FEATURE [App::DocumentObjectGroupPython] O_element059  label="O_element : 030"  # scripted group (container) (typed FeaturePython)
  n = 3
  ref = O_element
FEATURE [App::DocumentObjectGroupPython] G4_MAGNESIUM_CARBONATE  # scripted group (container) (typed FeaturePython)
  Dunit = g/cm3
  Dvalue = 2.958
  Group = -> [Mg_element005,C_element058,O_element059]
  conduct = 2
  density = 1
  expand = 3
  formula = G4_MAGNESIUM_CARBONATE
  name = G4_MAGNESIUM_CARBONATE
  specific = 4
FEATURE [App::DocumentObjectGroupPython] Mg_element006  label="Mg_element : 002"  # scripted group (container) (typed FeaturePython)
  n = 1
  ref = Mg_element
FEATURE [App::DocumentObjectGroupPython] F_element013  label="F_element : 005"  # scripted group (container) (typed FeaturePython)
  n = 2
  ref = F_element
FEATURE [App::DocumentObjectGroupPython] G4_MAGNESIUM_FLUORIDE  # scripted group (container) (typed FeaturePython)
  Dunit = g/cm3
  Dvalue = 3
  Group = -> [Mg_element006,F_element013]
  conduct = 2
  density = 1
  expand = 3
  formula = G4_MAGNESIUM_FLUORIDE
  name = G4_MAGNESIUM_FLUORIDE
  specific = 4
FEATURE [App::DocumentObjectGroupPython] Mg_element007  label="Mg_element : 003"  # scripted group (container) (typed FeaturePython)
  n = 1
  ref = Mg_element
FEATURE [App::DocumentObjectGroupPython] O_element060  label="O_element : 031"  # scripted group (container) (typed FeaturePython)
  n = 1
  ref = O_element
FEATURE [App::DocumentObjectGroupPython] G4_MAGNESIUM_OXIDE  # scripted group (container) (typed FeaturePython)
  Dunit = g/cm3
  Dvalue = 3.58
  Group = -> [Mg_element007,O_element060]
  conduct = 2
  density = 1
  expand = 3
  formula = G4_MAGNESIUM_OXIDE
  name = G4_MAGNESIUM_OXIDE
  specific = 4
FEATURE [App::DocumentObjectGroupPython] Mg_element008  label="Mg_element : 004"  # scripted group (container) (typed FeaturePython)
  n = 1
  ref = Mg_element
FEATURE [App::DocumentObjectGroupPython] B_element006  label="B_element : 006"  # scripted group (container) (typed FeaturePython)
  n = 4
  ref = B_element
FEATURE [App::DocumentObjectGroupPython] O_element061  label="O_element : 032"  # scripted group (container) (typed FeaturePython)
  n = 7
  ref = O_element
FEATURE [App::DocumentObjectGroupPython] G4_MAGNESIUM_TETRABORATE  # scripted group (container) (typed FeaturePython)
  Dunit = g/cm3
  Dvalue = 2.53
  Group = -> [Mg_element008,B_element006,O_element061]
  conduct = 2
  density = 1
  expand = 3
  formula = G4_MAGNESIUM_TETRABORATE
  name = G4_MAGNESIUM_TETRABORATE
  specific = 4
FEATURE [App::DocumentObjectGroupPython] Hg_element001  label="Hg_element : 1"  # scripted group (container) (typed FeaturePython)
  n = 1
  ref = Hg_element
FEATURE [App::DocumentObjectGroupPython] I_element004  label="I_element : 2"  # scripted group (container) (typed FeaturePython)
  n = 2
  ref = I_element
FEATURE [App::DocumentObjectGroupPython] G4_MERCURIC_IODIDE  # scripted group (container) (typed FeaturePython)
  Dunit = g/cm3
  Dvalue = 6.36
  Group = -> [Hg_element001,I_element004]
  conduct = 2
  density = 1
  expand = 3
  formula = G4_MERCURIC_IODIDE
  name = G4_MERCURIC_IODIDE
  specific = 4
FEATURE [App::DocumentObjectGroupPython] C_element059  label="C_element : 032"  # scripted group (container) (typed FeaturePython)
  n = 1
  ref = C_element
FEATURE [App::DocumentObjectGroupPython] H_element053  label="H_element : 028"  # scripted group (container) (typed FeaturePython)
  n = 4
  ref = H_element
FEATURE [App::DocumentObjectGroupPython] G4_METHANE  # scripted group (container) (typed FeaturePython)
  Dunit = g/cm3
  Dvalue = 0.000667151
  Group = -> [C_element059,H_element053]
  conduct = 2
  density = 1
  expand = 3
  formula = G4_METHANE
  name = G4_METHANE
  specific = 4
FEATURE [App::DocumentObjectGroupPython] C_element060  label="C_element : 033"  # scripted group (container) (typed FeaturePython)
  n = 1
  ref = C_element
FEATURE [App::DocumentObjectGroupPython] H_element054  label="H_element : 029"  # scripted group (container) (typed FeaturePython)
  n = 4
  ref = H_element
FEATURE [App::DocumentObjectGroupPython] O_element062  label="O_element : 033"  # scripted group (container) (typed FeaturePython)
  n = 1
  ref = O_element
FEATURE [App::DocumentObjectGroupPython] G4_METHANOL  # scripted group (container) (typed FeaturePython)
  Dunit = g/cm3
  Dvalue = 0.7914
  Group = -> [C_element060,H_element054,O_element062]
  conduct = 2
  density = 1
  expand = 3
  formula = G4_METHANOL
  name = G4_METHANOL
  specific = 4
FEATURE [App::DocumentObjectGroupPython] H_element055  label="H_element : 0.134"  # scripted group (container) (typed FeaturePython)
  n = 0.13404
FEATURE [App::DocumentObjectGroupPython] C_element061  label="C_element : 0.778"  # scripted group (container) (typed FeaturePython)
  n = 0.77796
FEATURE [App::DocumentObjectGroupPython] O_element063  label="O_element : 0.035"  # scripted group (container) (typed FeaturePython)
  n = 0.03502
FEATURE [App::DocumentObjectGroupPython] Mg_element009  label="Mg_element : 0.039"  # scripted group (container) (typed FeaturePython)
  n = 0.038594
FEATURE [App::DocumentObjectGroupPython] Ti_element002  label="Ti_element : 0.014"  # scripted group (container) (typed FeaturePython)
  n = 0.014386
FEATURE [App::DocumentObjectGroupPython] G4_MIX_D_WAX  # scripted group (container) (typed FeaturePython)
  Dunit = g/cm3
  Dvalue = 0.99
  Group = -> [H_element055,C_element061,O_element063,Mg_element009,Ti_element002]
  conduct = 2
  density = 1
  expand = 3
  formula = G4_MIX_D_WAX
  name = G4_MIX_D_WAX
  specific = 4
FEATURE [App::DocumentObjectGroupPython] H_element056  label="H_element : 0.135"  # scripted group (container) (typed FeaturePython)
  n = 0.081192
FEATURE [App::DocumentObjectGroupPython] C_element062  label="C_element : 0.583"  # scripted group (container) (typed FeaturePython)
  n = 0.583442
FEATURE [App::DocumentObjectGroupPython] N_element024  label="N_element : 0.018"  # scripted group (container) (typed FeaturePython)
  n = 0.017798
FEATURE [App::DocumentObjectGroupPython] O_element064  label="O_element : 0.186"  # scripted group (container) (typed FeaturePython)
  n = 0.186381
FEATURE [App::DocumentObjectGroupPython] Mg_element010  label="Mg_element : 0.130"  # scripted group (container) (typed FeaturePython)
  n = 0.130287
FEATURE [App::DocumentObjectGroupPython] Cl_element015  label="Cl_element : 0.588"  # scripted group (container) (typed FeaturePython)
  n = 0.0009
FEATURE [App::DocumentObjectGroupPython] G4_MS20_TISSUE  # scripted group (container) (typed FeaturePython)
  Dunit = g/cm3
  Dvalue = 1
  Group = -> [H_element056,C_element062,N_element024,O_element064,Mg_element010,Cl_element015]
  conduct = 2
  density = 1
  expand = 3
  formula = G4_MS20_TISSUE
  name = G4_MS20_TISSUE
  specific = 4
FEATURE [App::DocumentObjectGroupPython] H_element057  label="H_element : 0.136"  # scripted group (container) (typed FeaturePython)
  n = 0.102
FEATURE [App::DocumentObjectGroupPython] C_element063  label="C_element : 0.143"  # scripted group (container) (typed FeaturePython)
  n = 0.143
FEATURE [App::DocumentObjectGroupPython] N_element025  label="N_element : 0.034"  # scripted group (container) (typed FeaturePython)
  n = 0.034
FEATURE [App::DocumentObjectGroupPython] O_element065  label="O_element : 0.710"  # scripted group (container) (typed FeaturePython)
  n = 0.71
FEATURE [App::DocumentObjectGroupPython] Na_element011  label="Na_element : 0.098"  # scripted group (container) (typed FeaturePython)
  n = 0.001
FEATURE [App::DocumentObjectGroupPython] P_element007  label="P_element : 0.002"  # scripted group (container) (typed FeaturePython)
  n = 0.002
FEATURE [App::DocumentObjectGroupPython] S_element017  label="S_element : 0.018"  # scripted group (container) (typed FeaturePython)
  n = 0.003
FEATURE [App::DocumentObjectGroupPython] Cl_element016  label="Cl_element : 0.589"  # scripted group (container) (typed FeaturePython)
  n = 0.001
FEATURE [App::DocumentObjectGroupPython] K_element006  label="K_element : 0.004"  # scripted group (container) (typed FeaturePython)
  n = 0.004
FEATURE [App::DocumentObjectGroupPython] G4_MUSCLE_SKELETAL_ICRP  # scripted group (container) (typed FeaturePython)
  Dunit = g/cm3
  Dvalue = 1.05
  Group = -> [H_element057,C_element063,N_element025,O_element065,Na_element011,P_element007,S_element017,Cl_element016,K_element006]
  conduct = 2
  density = 1
  expand = 3
  formula = G4_MUSCLE_SKELETAL_ICRP
  name = G4_MUSCLE_SKELETAL_ICRP
  specific = 4
FEATURE [App::DocumentObjectGroupPython] H_element058  label="H_element : 0.137"  # scripted group (container) (typed FeaturePython)
  n = 0.102102
FEATURE [App::DocumentObjectGroupPython] C_element064  label="C_element : 0.123"  # scripted group (container) (typed FeaturePython)
  n = 0.123123
FEATURE [App::DocumentObjectGroupPython] N_element026  label="N_element : 0.756"  # scripted group (container) (typed FeaturePython)
  n = 0.035035
FEATURE [App::DocumentObjectGroupPython] O_element066  label="O_element : 0.730"  # scripted group (container) (typed FeaturePython)
  n = 0.72973
FEATURE [App::DocumentObjectGroupPython] Na_element012  label="Na_element : 0.099"  # scripted group (container) (typed FeaturePython)
  n = 0.001001
FEATURE [App::DocumentObjectGroupPython] P_element008  label="P_element : 0.106"  # scripted group (container) (typed FeaturePython)
  n = 0.002002
FEATURE [App::DocumentObjectGroupPython] S_element018  label="S_element : 0.019"  # scripted group (container) (typed FeaturePython)
  n = 0.004004
FEATURE [App::DocumentObjectGroupPython] K_element007  label="K_element : 0.016"  # scripted group (container) (typed FeaturePython)
  n = 0.003003
FEATURE [App::DocumentObjectGroupPython] G4_MUSCLE_STRIATED_ICRU  # scripted group (container) (typed FeaturePython)
  Dunit = g/cm3
  Dvalue = 1.04
  Group = -> [H_element058,C_element064,N_element026,O_element066,Na_element012,P_element008,S_element018,K_element007]
  conduct = 2
  density = 1
  expand = 3
  formula = G4_MUSCLE_STRIATED_ICRU
  name = G4_MUSCLE_STRIATED_ICRU
  specific = 4
FEATURE [App::DocumentObjectGroupPython] H_element059  label="H_element : 0.098"  # scripted group (container) (typed FeaturePython)
  n = 0.0982341
FEATURE [App::DocumentObjectGroupPython] C_element065  label="C_element : 0.156"  # scripted group (container) (typed FeaturePython)
  n = 0.156214
FEATURE [App::DocumentObjectGroupPython] N_element027  label="N_element : 0.757"  # scripted group (container) (typed FeaturePython)
  n = 0.035451
FEATURE [App::DocumentObjectGroupPython] O_element067  label="O_element : 0.880"  # scripted group (container) (typed FeaturePython)
  n = 0.710101
FEATURE [App::DocumentObjectGroupPython] G4_MUSCLE_WITH_SUCROSE  # scripted group (container) (typed FeaturePython)
  Dunit = g/cm3
  Dvalue = 1.11
  Group = -> [H_element059,C_element065,N_element027,O_element067]
  conduct = 2
  density = 1
  expand = 3
  formula = G4_MUSCLE_WITH_SUCROSE
  name = G4_MUSCLE_WITH_SUCROSE
  specific = 4
FEATURE [App::DocumentObjectGroupPython] H_element060  label="H_element : 0.138"  # scripted group (container) (typed FeaturePython)
  n = 0.101969
FEATURE [App::DocumentObjectGroupPython] C_element066  label="C_element : 0.120"  # scripted group (container) (typed FeaturePython)
  n = 0.120058
FEATURE [App::DocumentObjectGroupPython] N_element028  label="N_element : 0.758"  # scripted group (container) (typed FeaturePython)
  n = 0.035451
FEATURE [App::DocumentObjectGroupPython] O_element068  label="O_element : 0.743"  # scripted group (container) (typed FeaturePython)
  n = 0.742522
FEATURE [App::DocumentObjectGroupPython] G4_MUSCLE_WITHOUT_SUCROSE  # scripted group (container) (typed FeaturePython)
  Dunit = g/cm3
  Dvalue = 1.07
  Group = -> [H_element060,C_element066,N_element028,O_element068]
  conduct = 2
  density = 1
  expand = 3
  formula = G4_MUSCLE_WITHOUT_SUCROSE
  name = G4_MUSCLE_WITHOUT_SUCROSE
  specific = 4
FEATURE [App::DocumentObjectGroupPython] C_element067  label="C_element : 10"  # scripted group (container) (typed FeaturePython)
  n = 10
  ref = C_element
FEATURE [App::DocumentObjectGroupPython] H_element061  label="H_element : 030"  # scripted group (container) (typed FeaturePython)
  n = 8
  ref = H_element
FEATURE [App::DocumentObjectGroupPython] G4_NAPHTHALENE  # scripted group (container) (typed FeaturePython)
  Dunit = g/cm3
  Dvalue = 1.145
  Group = -> [C_element067,H_element061]
  conduct = 2
  density = 1
  expand = 3
  formula = G4_NAPHTHALENE
  name = G4_NAPHTHALENE
  specific = 4
FEATURE [App::DocumentObjectGroupPython] C_element068  label="C_element : 034"  # scripted group (container) (typed FeaturePython)
  n = 6
  ref = C_element
FEATURE [App::DocumentObjectGroupPython] H_element062  label="H_element : 031"  # scripted group (container) (typed FeaturePython)
  n = 5
  ref = H_element
FEATURE [App::DocumentObjectGroupPython] N_element029  label="N_element : 012"  # scripted group (container) (typed FeaturePython)
  n = 1
  ref = N_element
FEATURE [App::DocumentObjectGroupPython] O_element069  label="O_element : 034"  # scripted group (container) (typed FeaturePython)
  n = 2
  ref = O_element
FEATURE [App::DocumentObjectGroupPython] G4_NITROBENZENE  # scripted group (container) (typed FeaturePython)
  Dunit = g/cm3
  Dvalue = 1.19867
  Group = -> [C_element068,H_element062,N_element029,O_element069]
  conduct = 2
  density = 1
  expand = 3
  formula = G4_NITROBENZENE
  name = G4_NITROBENZENE
  specific = 4
FEATURE [App::DocumentObjectGroupPython] N_element030  label="N_element : 013"  # scripted group (container) (typed FeaturePython)
  n = 2
  ref = N_element
FEATURE [App::DocumentObjectGroupPython] O_element070  label="O_element : 035"  # scripted group (container) (typed FeaturePython)
  n = 1
  ref = O_element
FEATURE [App::DocumentObjectGroupPython] G4_NITROUS_OXIDE  # scripted group (container) (typed FeaturePython)
  Dunit = g/cm3
  Dvalue = 0.00183094
  Group = -> [N_element030,O_element070]
  conduct = 2
  density = 1
  expand = 3
  formula = G4_NITROUS_OXIDE
  name = G4_NITROUS_OXIDE
  specific = 4
FEATURE [App::DocumentObjectGroupPython] H_element063  label="H_element : 0.104"  # scripted group (container) (typed FeaturePython)
  n = 0.103509
FEATURE [App::DocumentObjectGroupPython] C_element069  label="C_element : 0.648"  # scripted group (container) (typed FeaturePython)
  n = 0.648416
FEATURE [App::DocumentObjectGroupPython] N_element031  label="N_element : 0.100"  # scripted group (container) (typed FeaturePython)
  n = 0.0995361
FEATURE [App::DocumentObjectGroupPython] O_element071  label="O_element : 0.149"  # scripted group (container) (typed FeaturePython)
  n = 0.148539
FEATURE [App::DocumentObjectGroupPython] G4_NYLON_8062  label="G4_NYLON-8062"  # scripted group (container) (typed FeaturePython)
  Dunit = g/cm3
  Dvalue = 1.08
  Group = -> [H_element063,C_element069,N_element031,O_element071]
  conduct = 2
  density = 1
  expand = 3
  formula = G4_NYLON-8062
  name = G4_NYLON-8062
  specific = 4
FEATURE [App::DocumentObjectGroupPython] C_element070  label="C_element : 035"  # scripted group (container) (typed FeaturePython)
  n = 6
  ref = C_element
FEATURE [App::DocumentObjectGroupPython] H_element064  label="H_element : 11"  # scripted group (container) (typed FeaturePython)
  n = 11
  ref = H_element
FEATURE [App::DocumentObjectGroupPython] N_element032  label="N_element : 014"  # scripted group (container) (typed FeaturePython)
  n = 1
  ref = N_element
FEATURE [App::DocumentObjectGroupPython] O_element072  label="O_element : 036"  # scripted group (container) (typed FeaturePython)
  n = 1
  ref = O_element
FEATURE [App::DocumentObjectGroupPython] G4_NYLON_6_6  label="G4_NYLON-6-6"  # scripted group (container) (typed FeaturePython)
  Dunit = g/cm3
  Dvalue = 1.14
  Group = -> [C_element070,H_element064,N_element032,O_element072]
  conduct = 2
  density = 1
  expand = 3
  formula = G4_NYLON-6-6
  name = G4_NYLON-6-6
  specific = 4
FEATURE [App::DocumentObjectGroupPython] H_element065  label="H_element : 0.139"  # scripted group (container) (typed FeaturePython)
  n = 0.107062
FEATURE [App::DocumentObjectGroupPython] C_element071  label="C_element : 0.680"  # scripted group (container) (typed FeaturePython)
  n = 0.680449
FEATURE [App::DocumentObjectGroupPython] N_element033  label="N_element : 0.099"  # scripted group (container) (typed FeaturePython)
  n = 0.099189
FEATURE [App::DocumentObjectGroupPython] O_element073  label="O_element : 0.113"  # scripted group (container) (typed FeaturePython)
  n = 0.1133
FEATURE [App::DocumentObjectGroupPython] G4_NYLON_6_10  label="G4_NYLON-6-10"  # scripted group (container) (typed FeaturePython)
  Dunit = g/cm3
  Dvalue = 1.14
  Group = -> [H_element065,C_element071,N_element033,O_element073]
  conduct = 2
  density = 1
  expand = 3
  formula = G4_NYLON-6-10
  name = G4_NYLON-6-10
  specific = 4
FEATURE [App::DocumentObjectGroupPython] H_element066  label="H_element : 0.140"  # scripted group (container) (typed FeaturePython)
  n = 0.115476
FEATURE [App::DocumentObjectGroupPython] C_element072  label="C_element : 0.721"  # scripted group (container) (typed FeaturePython)
  n = 0.720818
FEATURE [App::DocumentObjectGroupPython] N_element034  label="N_element : 0.076"  # scripted group (container) (typed FeaturePython)
  n = 0.0764169
FEATURE [App::DocumentObjectGroupPython] O_element074  label="O_element : 0.087"  # scripted group (container) (typed FeaturePython)
  n = 0.0872889
FEATURE [App::DocumentObjectGroupPython] G4_NYLON_11_RILSAN  label="G4_NYLON-11_RILSAN"  # scripted group (container) (typed FeaturePython)
  Dunit = g/cm3
  Dvalue = 1.425
  Group = -> [H_element066,C_element072,N_element034,O_element074]
  conduct = 2
  density = 1
  expand = 3
  formula = G4_NYLON-11_RILSAN
  name = G4_NYLON-11_RILSAN
  specific = 4
FEATURE [App::DocumentObjectGroupPython] C_element073  label="C_element : 8"  # scripted group (container) (typed FeaturePython)
  n = 8
  ref = C_element
FEATURE [App::DocumentObjectGroupPython] H_element067  label="H_element : 18"  # scripted group (container) (typed FeaturePython)
  n = 18
  ref = H_element
FEATURE [App::DocumentObjectGroupPython] G4_OCTANE  # scripted group (container) (typed FeaturePython)
  Dunit = g/cm3
  Dvalue = 0.7026
  Group = -> [C_element073,H_element067]
  conduct = 2
  density = 1
  expand = 3
  formula = G4_OCTANE
  name = G4_OCTANE
  specific = 4
FEATURE [App::DocumentObjectGroupPython] C_element074  label="C_element : 25"  # scripted group (container) (typed FeaturePython)
  n = 25
  ref = C_element
FEATURE [App::DocumentObjectGroupPython] H_element068  label="H_element : 52"  # scripted group (container) (typed FeaturePython)
  n = 52
  ref = H_element
FEATURE [App::DocumentObjectGroupPython] G4_PARAFFIN  # scripted group (container) (typed FeaturePython)
  Dunit = g/cm3
  Dvalue = 0.93
  Group = -> [C_element074,H_element068]
  conduct = 2
  density = 1
  expand = 3
  formula = G4_PARAFFIN
  name = G4_PARAFFIN
  specific = 4
FEATURE [App::DocumentObjectGroupPython] C_element075  label="C_element : 036"  # scripted group (container) (typed FeaturePython)
  n = 5
  ref = C_element
FEATURE [App::DocumentObjectGroupPython] H_element069  label="H_element : 032"  # scripted group (container) (typed FeaturePython)
  n = 12
  ref = H_element
FEATURE [App::DocumentObjectGroupPython] G4_N_PENTANE  label="G4_N-PENTANE"  # scripted group (container) (typed FeaturePython)
  Dunit = g/cm3
  Dvalue = 0.6262
  Group = -> [C_element075,H_element069]
  conduct = 2
  density = 1
  expand = 3
  formula = G4_N-PENTANE
  name = G4_N-PENTANE
  specific = 4
FEATURE [App::DocumentObjectGroupPython] H_element070  label="H_element : 0.014"  # scripted group (container) (typed FeaturePython)
  n = 0.0141
FEATURE [App::DocumentObjectGroupPython] C_element076  label="C_element : 0.072"  # scripted group (container) (typed FeaturePython)
  n = 0.072261
FEATURE [App::DocumentObjectGroupPython] N_element035  label="N_element : 0.019"  # scripted group (container) (typed FeaturePython)
  n = 0.01932
FEATURE [App::DocumentObjectGroupPython] O_element075  label="O_element : 0.066"  # scripted group (container) (typed FeaturePython)
  n = 0.066101
FEATURE [App::DocumentObjectGroupPython] S_element019  label="S_element : 0.020"  # scripted group (container) (typed FeaturePython)
  n = 0.00189
FEATURE [App::DocumentObjectGroupPython] Br_element004  label="Br_element : 0.349"  # scripted group (container) (typed FeaturePython)
  n = 0.349103
FEATURE [App::DocumentObjectGroupPython] Ag_element001  label="Ag_element : 0.474"  # scripted group (container) (typed FeaturePython)
  n = 0.474105
FEATURE [App::DocumentObjectGroupPython] I_element005  label="I_element : 0.003"  # scripted group (container) (typed FeaturePython)
  n = 0.00312
FEATURE [App::DocumentObjectGroupPython] G4_PHOTO_EMULSION  # scripted group (container) (typed FeaturePython)
  Dunit = g/cm3
  Dvalue = 3.815
  Group = -> [H_element070,C_element076,N_element035,O_element075,S_element019,Br_element004,Ag_element001,I_element005]
  conduct = 2
  density = 1
  expand = 3
  formula = G4_PHOTO_EMULSION
  name = G4_PHOTO_EMULSION
  specific = 4
FEATURE [App::DocumentObjectGroupPython] C_element077  label="C_element : 9"  # scripted group (container) (typed FeaturePython)
  n = 9
  ref = C_element
FEATURE [App::DocumentObjectGroupPython] H_element071  label="H_element : 033"  # scripted group (container) (typed FeaturePython)
  n = 10
  ref = H_element
FEATURE [App::DocumentObjectGroupPython] G4_PLASTIC_SC_VINYLTOLUENE  # scripted group (container) (typed FeaturePython)
  Dunit = g/cm3
  Dvalue = 1.032
  Group = -> [C_element077,H_element071]
  conduct = 2
  density = 1
  expand = 3
  formula = G4_PLASTIC_SC_VINYLTOLUENE
  name = G4_PLASTIC_SC_VINYLTOLUENE
  specific = 4
FEATURE [App::DocumentObjectGroupPython] Pu_element001  label="Pu_element : 1"  # scripted group (container) (typed FeaturePython)
  n = 1
  ref = Pu_element
FEATURE [App::DocumentObjectGroupPython] O_element076  label="O_element : 037"  # scripted group (container) (typed FeaturePython)
  n = 2
  ref = O_element
FEATURE [App::DocumentObjectGroupPython] G4_PLUTONIUM_DIOXIDE  # scripted group (container) (typed FeaturePython)
  Dunit = g/cm3
  Dvalue = 11.46
  Group = -> [Pu_element001,O_element076]
  conduct = 2
  density = 1
  expand = 3
  formula = G4_PLUTONIUM_DIOXIDE
  name = G4_PLUTONIUM_DIOXIDE
  specific = 4
FEATURE [App::DocumentObjectGroupPython] C_element078  label="C_element : 037"  # scripted group (container) (typed FeaturePython)
  n = 3
  ref = C_element
FEATURE [App::DocumentObjectGroupPython] H_element072  label="H_element : 034"  # scripted group (container) (typed FeaturePython)
  n = 3
  ref = H_element
FEATURE [App::DocumentObjectGroupPython] N_element036  label="N_element : 015"  # scripted group (container) (typed FeaturePython)
  n = 1
  ref = N_element
FEATURE [App::DocumentObjectGroupPython] G4_POLYACRYLONITRILE  # scripted group (container) (typed FeaturePython)
  Dunit = g/cm3
  Dvalue = 1.17
  Group = -> [C_element078,H_element072,N_element036]
  conduct = 2
  density = 1
  expand = 3
  formula = G4_POLYACRYLONITRILE
  name = G4_POLYACRYLONITRILE
  specific = 4
FEATURE [App::DocumentObjectGroupPython] C_element079  label="C_element : 16"  # scripted group (container) (typed FeaturePython)
  n = 16
  ref = C_element
FEATURE [App::DocumentObjectGroupPython] H_element073  label="H_element : 035"  # scripted group (container) (typed FeaturePython)
  n = 14
  ref = H_element
FEATURE [App::DocumentObjectGroupPython] O_element077  label="O_element : 038"  # scripted group (container) (typed FeaturePython)
  n = 3
  ref = O_element
FEATURE [App::DocumentObjectGroupPython] G4_POLYCARBONATE  # scripted group (container) (typed FeaturePython)
  Dunit = g/cm3
  Dvalue = 1.2
  Group = -> [C_element079,H_element073,O_element077]
  conduct = 2
  density = 1
  expand = 3
  formula = G4_POLYCARBONATE
  name = G4_POLYCARBONATE
  specific = 4
FEATURE [App::DocumentObjectGroupPython] C_element080  label="C_element : 038"  # scripted group (container) (typed FeaturePython)
  n = 8
  ref = C_element
FEATURE [App::DocumentObjectGroupPython] H_element074  label="H_element : 036"  # scripted group (container) (typed FeaturePython)
  n = 7
  ref = H_element
FEATURE [App::DocumentObjectGroupPython] Cl_element017  label="Cl_element : 007"  # scripted group (container) (typed FeaturePython)
  n = 1
  ref = Cl_element
FEATURE [App::DocumentObjectGroupPython] G4_POLYCHLOROSTYRENE  # scripted group (container) (typed FeaturePython)
  Dunit = g/cm3
  Dvalue = 1.3
  Group = -> [C_element080,H_element074,Cl_element017]
  conduct = 2
  density = 1
  expand = 3
  formula = G4_POLYCHLOROSTYRENE
  name = G4_POLYCHLOROSTYRENE
  specific = 4
FEATURE [App::DocumentObjectGroupPython] C_element081  label="C_element : 039"  # scripted group (container) (typed FeaturePython)
  n = 1
  ref = C_element
FEATURE [App::DocumentObjectGroupPython] H_element075  label="H_element : 037"  # scripted group (container) (typed FeaturePython)
  n = 2
  ref = H_element
FEATURE [App::DocumentObjectGroupPython] G4_POLYETHYLENE  # scripted group (container) (typed FeaturePython)
  Dunit = g/cm3
  Dvalue = 0.94
  Group = -> [C_element081,H_element075]
  conduct = 2
  density = 1
  expand = 3
  formula = G4_POLYETHYLENE
  name = G4_POLYETHYLENE
  specific = 4
FEATURE [App::DocumentObjectGroupPython] C_element082  label="C_element : 040"  # scripted group (container) (typed FeaturePython)
  n = 10
  ref = C_element
FEATURE [App::DocumentObjectGroupPython] H_element076  label="H_element : 038"  # scripted group (container) (typed FeaturePython)
  n = 8
  ref = H_element
FEATURE [App::DocumentObjectGroupPython] O_element078  label="O_element : 039"  # scripted group (container) (typed FeaturePython)
  n = 4
  ref = O_element
FEATURE [App::DocumentObjectGroupPython] G4_MYLAR  # scripted group (container) (typed FeaturePython)
  Dunit = g/cm3
  Dvalue = 1.4
  Group = -> [C_element082,H_element076,O_element078]
  conduct = 2
  density = 1
  expand = 3
  formula = G4_MYLAR
  name = G4_MYLAR
  specific = 4
FEATURE [App::DocumentObjectGroupPython] C_element083  label="C_element : 041"  # scripted group (container) (typed FeaturePython)
  n = 5
  ref = C_element
FEATURE [App::DocumentObjectGroupPython] H_element077  label="H_element : 039"  # scripted group (container) (typed FeaturePython)
  n = 8
  ref = H_element
FEATURE [App::DocumentObjectGroupPython] O_element079  label="O_element : 040"  # scripted group (container) (typed FeaturePython)
  n = 2
  ref = O_element
FEATURE [App::DocumentObjectGroupPython] G4_PLEXIGLASS  # scripted group (container) (typed FeaturePython)
  Dunit = g/cm3
  Dvalue = 1.19
  Group = -> [C_element083,H_element077,O_element079]
  conduct = 2
  density = 1
  expand = 3
  formula = G4_PLEXIGLASS
  name = G4_PLEXIGLASS
  specific = 4
FEATURE [App::DocumentObjectGroupPython] C_element084  label="C_element : 042"  # scripted group (container) (typed FeaturePython)
  n = 1
  ref = C_element
FEATURE [App::DocumentObjectGroupPython] H_element078  label="H_element : 040"  # scripted group (container) (typed FeaturePython)
  n = 2
  ref = H_element
FEATURE [App::DocumentObjectGroupPython] O_element080  label="O_element : 041"  # scripted group (container) (typed FeaturePython)
  n = 1
  ref = O_element
FEATURE [App::DocumentObjectGroupPython] G4_POLYOXYMETHYLENE  # scripted group (container) (typed FeaturePython)
  Dunit = g/cm3
  Dvalue = 1.425
  Group = -> [C_element084,H_element078,O_element080]
  conduct = 2
  density = 1
  expand = 3
  formula = G4_POLYOXYMETHYLENE
  name = G4_POLYOXYMETHYLENE
  specific = 4
FEATURE [App::DocumentObjectGroupPython] C_element085  label="C_element : 043"  # scripted group (container) (typed FeaturePython)
  n = 2
  ref = C_element
FEATURE [App::DocumentObjectGroupPython] H_element079  label="H_element : 041"  # scripted group (container) (typed FeaturePython)
  n = 4
  ref = H_element
FEATURE [App::DocumentObjectGroupPython] G4_POLYPROPYLENE  # scripted group (container) (typed FeaturePython)
  Dunit = g/cm3
  Dvalue = 0.9
  Group = -> [C_element085,H_element079]
  conduct = 2
  density = 1
  expand = 3
  formula = G4_POLYPROPYLENE
  name = G4_POLYPROPYLENE
  specific = 4
FEATURE [App::DocumentObjectGroupPython] C_element086  label="C_element : 044"  # scripted group (container) (typed FeaturePython)
  n = 8
  ref = C_element
FEATURE [App::DocumentObjectGroupPython] H_element080  label="H_element : 042"  # scripted group (container) (typed FeaturePython)
  n = 8
  ref = H_element
FEATURE [App::DocumentObjectGroupPython] G4_POLYSTYRENE  # scripted group (container) (typed FeaturePython)
  Dunit = g/cm3
  Dvalue = 1.06
  Group = -> [C_element086,H_element080]
  conduct = 2
  density = 1
  expand = 3
  formula = G4_POLYSTYRENE
  name = G4_POLYSTYRENE
  specific = 4
FEATURE [App::DocumentObjectGroupPython] C_element087  label="C_element : 045"  # scripted group (container) (typed FeaturePython)
  n = 2
  ref = C_element
FEATURE [App::DocumentObjectGroupPython] F_element014  label="F_element : 4"  # scripted group (container) (typed FeaturePython)
  n = 4
  ref = F_element
FEATURE [App::DocumentObjectGroupPython] G4_TEFLON  # scripted group (container) (typed FeaturePython)
  Dunit = g/cm3
  Dvalue = 2.2
  Group = -> [C_element087,F_element014]
  conduct = 2
  density = 1
  expand = 3
  formula = G4_TEFLON
  name = G4_TEFLON
  specific = 4
FEATURE [App::DocumentObjectGroupPython] C_element088  label="C_element : 046"  # scripted group (container) (typed FeaturePython)
  n = 2
  ref = C_element
FEATURE [App::DocumentObjectGroupPython] F_element015  label="F_element : 006"  # scripted group (container) (typed FeaturePython)
  n = 3
  ref = F_element
FEATURE [App::DocumentObjectGroupPython] Cl_element018  label="Cl_element : 008"  # scripted group (container) (typed FeaturePython)
  n = 1
  ref = Cl_element
FEATURE [App::DocumentObjectGroupPython] G4_POLYTRIFLUOROCHLOROETHYLENE  # scripted group (container) (typed FeaturePython)
  Dunit = g/cm3
  Dvalue = 2.1
  Group = -> [C_element088,F_element015,Cl_element018]
  conduct = 2
  density = 1
  expand = 3
  formula = G4_POLYTRIFLUOROCHLOROETHYLENE
  name = G4_POLYTRIFLUOROCHLOROETHYLENE
  specific = 4
FEATURE [App::DocumentObjectGroupPython] C_element089  label="C_element : 047"  # scripted group (container) (typed FeaturePython)
  n = 4
  ref = C_element
FEATURE [App::DocumentObjectGroupPython] H_element081  label="H_element : 043"  # scripted group (container) (typed FeaturePython)
  n = 6
  ref = H_element
FEATURE [App::DocumentObjectGroupPython] O_element081  label="O_element : 042"  # scripted group (container) (typed FeaturePython)
  n = 2
  ref = O_element
FEATURE [App::DocumentObjectGroupPython] G4_POLYVINYL_ACETATE  # scripted group (container) (typed FeaturePython)
  Dunit = g/cm3
  Dvalue = 1.19
  Group = -> [C_element089,H_element081,O_element081]
  conduct = 2
  density = 1
  expand = 3
  formula = G4_POLYVINYL_ACETATE
  name = G4_POLYVINYL_ACETATE
  specific = 4
FEATURE [App::DocumentObjectGroupPython] C_element090  label="C_element : 048"  # scripted group (container) (typed FeaturePython)
  n = 2
  ref = C_element
FEATURE [App::DocumentObjectGroupPython] H_element082  label="H_element : 044"  # scripted group (container) (typed FeaturePython)
  n = 4
  ref = H_element
FEATURE [App::DocumentObjectGroupPython] O_element082  label="O_element : 043"  # scripted group (container) (typed FeaturePython)
  n = 1
  ref = O_element
FEATURE [App::DocumentObjectGroupPython] G4_POLYVINYL_ALCOHOL  # scripted group (container) (typed FeaturePython)
  Dunit = g/cm3
  Dvalue = 1.3
  Group = -> [C_element090,H_element082,O_element082]
  conduct = 2
  density = 1
  expand = 3
  formula = G4_POLYVINYL_ALCOHOL
  name = G4_POLYVINYL_ALCOHOL
  specific = 4
FEATURE [App::DocumentObjectGroupPython] C_element091  label="C_element : 049"  # scripted group (container) (typed FeaturePython)
  n = 8
  ref = C_element
FEATURE [App::DocumentObjectGroupPython] H_element083  label="H_element : 045"  # scripted group (container) (typed FeaturePython)
  n = 14
  ref = H_element
FEATURE [App::DocumentObjectGroupPython] O_element083  label="O_element : 044"  # scripted group (container) (typed FeaturePython)
  n = 2
  ref = O_element
FEATURE [App::DocumentObjectGroupPython] G4_POLYVINYL_BUTYRAL  # scripted group (container) (typed FeaturePython)
  Dunit = g/cm3
  Dvalue = 1.12
  Group = -> [C_element091,H_element083,O_element083]
  conduct = 2
  density = 1
  expand = 3
  formula = G4_POLYVINYL_BUTYRAL
  name = G4_POLYVINYL_BUTYRAL
  specific = 4
FEATURE [App::DocumentObjectGroupPython] C_element092  label="C_element : 050"  # scripted group (container) (typed FeaturePython)
  n = 2
  ref = C_element
FEATURE [App::DocumentObjectGroupPython] H_element084  label="H_element : 046"  # scripted group (container) (typed FeaturePython)
  n = 3
  ref = H_element
FEATURE [App::DocumentObjectGroupPython] Cl_element019  label="Cl_element : 009"  # scripted group (container) (typed FeaturePython)
  n = 1
  ref = Cl_element
FEATURE [App::DocumentObjectGroupPython] G4_POLYVINYL_CHLORIDE  # scripted group (container) (typed FeaturePython)
  Dunit = g/cm3
  Dvalue = 1.3
  Group = -> [C_element092,H_element084,Cl_element019]
  conduct = 2
  density = 1
  expand = 3
  formula = G4_POLYVINYL_CHLORIDE
  name = G4_POLYVINYL_CHLORIDE
  specific = 4
FEATURE [App::DocumentObjectGroupPython] C_element093  label="C_element : 051"  # scripted group (container) (typed FeaturePython)
  n = 2
  ref = C_element
FEATURE [App::DocumentObjectGroupPython] H_element085  label="H_element : 047"  # scripted group (container) (typed FeaturePython)
  n = 2
  ref = H_element
FEATURE [App::DocumentObjectGroupPython] Cl_element020  label="Cl_element : 010"  # scripted group (container) (typed FeaturePython)
  n = 2
  ref = Cl_element
FEATURE [App::DocumentObjectGroupPython] G4_POLYVINYLIDENE_CHLORIDE  # scripted group (container) (typed FeaturePython)
  Dunit = g/cm3
  Dvalue = 1.7
  Group = -> [C_element093,H_element085,Cl_element020]
  conduct = 2
  density = 1
  expand = 3
  formula = G4_POLYVINYLIDENE_CHLORIDE
  name = G4_POLYVINYLIDENE_CHLORIDE
  specific = 4
FEATURE [App::DocumentObjectGroupPython] C_element094  label="C_element : 052"  # scripted group (container) (typed FeaturePython)
  n = 2
  ref = C_element
FEATURE [App::DocumentObjectGroupPython] H_element086  label="H_element : 048"  # scripted group (container) (typed FeaturePython)
  n = 2
  ref = H_element
FEATURE [App::DocumentObjectGroupPython] F_element016  label="F_element : 007"  # scripted group (container) (typed FeaturePython)
  n = 2
  ref = F_element
FEATURE [App::DocumentObjectGroupPython] G4_POLYVINYLIDENE_FLUORIDE  # scripted group (container) (typed FeaturePython)
  Dunit = g/cm3
  Dvalue = 1.76
  Group = -> [C_element094,H_element086,F_element016]
  conduct = 2
  density = 1
  expand = 3
  formula = G4_POLYVINYLIDENE_FLUORIDE
  name = G4_POLYVINYLIDENE_FLUORIDE
  specific = 4
FEATURE [App::DocumentObjectGroupPython] C_element095  label="C_element : 053"  # scripted group (container) (typed FeaturePython)
  n = 6
  ref = C_element
FEATURE [App::DocumentObjectGroupPython] H_element087  label="H_element : 9"  # scripted group (container) (typed FeaturePython)
  n = 9
  ref = H_element
FEATURE [App::DocumentObjectGroupPython] N_element037  label="N_element : 016"  # scripted group (container) (typed FeaturePython)
  n = 1
  ref = N_element
FEATURE [App::DocumentObjectGroupPython] O_element084  label="O_element : 045"  # scripted group (container) (typed FeaturePython)
  n = 1
  ref = O_element
FEATURE [App::DocumentObjectGroupPython] G4_POLYVINYL_PYRROLIDONE  # scripted group (container) (typed FeaturePython)
  Dunit = g/cm3
  Dvalue = 1.25
  Group = -> [C_element095,H_element087,N_element037,O_element084]
  conduct = 2
  density = 1
  expand = 3
  formula = G4_POLYVINYL_PYRROLIDONE
  name = G4_POLYVINYL_PYRROLIDONE
  specific = 4
FEATURE [App::DocumentObjectGroupPython] K_element008  label="K_element : 1"  # scripted group (container) (typed FeaturePython)
  n = 1
  ref = K_element
FEATURE [App::DocumentObjectGroupPython] I_element006  label="I_element : 003"  # scripted group (container) (typed FeaturePython)
  n = 1
  ref = I_element
FEATURE [App::DocumentObjectGroupPython] G4_POTASSIUM_IODIDE  # scripted group (container) (typed FeaturePython)
  Dunit = g/cm3
  Dvalue = 3.13
  Group = -> [K_element008,I_element006]
  conduct = 2
  density = 1
  expand = 3
  formula = G4_POTASSIUM_IODIDE
  name = G4_POTASSIUM_IODIDE
  specific = 4
FEATURE [App::DocumentObjectGroupPython] K_element009  label="K_element : 2"  # scripted group (container) (typed FeaturePython)
  n = 2
  ref = K_element
FEATURE [App::DocumentObjectGroupPython] O_element085  label="O_element : 046"  # scripted group (container) (typed FeaturePython)
  n = 1
  ref = O_element
FEATURE [App::DocumentObjectGroupPython] G4_POTASSIUM_OXIDE  # scripted group (container) (typed FeaturePython)
  Dunit = g/cm3
  Dvalue = 2.32
  Group = -> [K_element009,O_element085]
  conduct = 2
  density = 1
  expand = 3
  formula = G4_POTASSIUM_OXIDE
  name = G4_POTASSIUM_OXIDE
  specific = 4
FEATURE [App::DocumentObjectGroupPython] C_element096  label="C_element : 054"  # scripted group (container) (typed FeaturePython)
  n = 3
  ref = C_element
FEATURE [App::DocumentObjectGroupPython] H_element088  label="H_element : 049"  # scripted group (container) (typed FeaturePython)
  n = 8
  ref = H_element
FEATURE [App::DocumentObjectGroupPython] G4_PROPANE  # scripted group (container) (typed FeaturePython)
  Dunit = g/cm3
  Dvalue = 0.00187939
  Group = -> [C_element096,H_element088]
  conduct = 2
  density = 1
  expand = 3
  formula = G4_PROPANE
  name = G4_PROPANE
  specific = 4
FEATURE [App::DocumentObjectGroupPython] C_element097  label="C_element : 055"  # scripted group (container) (typed FeaturePython)
  n = 3
  ref = C_element
FEATURE [App::DocumentObjectGroupPython] H_element089  label="H_element : 050"  # scripted group (container) (typed FeaturePython)
  n = 8
  ref = H_element
FEATURE [App::DocumentObjectGroupPython] G4_lPROPANE  # scripted group (container) (typed FeaturePython)
  Dunit = g/cm3
  Dvalue = 0.43
  Group = -> [C_element097,H_element089]
  conduct = 2
  density = 1
  expand = 3
  formula = G4_lPROPANE
  name = G4_lPROPANE
  specific = 4
FEATURE [App::DocumentObjectGroupPython] C_element098  label="C_element : 056"  # scripted group (container) (typed FeaturePython)
  n = 3
  ref = C_element
FEATURE [App::DocumentObjectGroupPython] H_element090  label="H_element : 051"  # scripted group (container) (typed FeaturePython)
  n = 8
  ref = H_element
FEATURE [App::DocumentObjectGroupPython] O_element086  label="O_element : 047"  # scripted group (container) (typed FeaturePython)
  n = 1
  ref = O_element
FEATURE [App::DocumentObjectGroupPython] G4_N_PROPYL_ALCOHOL  label="G4_N-PROPYL_ALCOHOL"  # scripted group (container) (typed FeaturePython)
  Dunit = g/cm3
  Dvalue = 0.8035
  Group = -> [C_element098,H_element090,O_element086]
  conduct = 2
  density = 1
  expand = 3
  formula = G4_N-PROPYL_ALCOHOL
  name = G4_N-PROPYL_ALCOHOL
  specific = 4
FEATURE [App::DocumentObjectGroupPython] C_element099  label="C_element : 057"  # scripted group (container) (typed FeaturePython)
  n = 5
  ref = C_element
FEATURE [App::DocumentObjectGroupPython] H_element091  label="H_element : 052"  # scripted group (container) (typed FeaturePython)
  n = 5
  ref = H_element
FEATURE [App::DocumentObjectGroupPython] N_element038  label="N_element : 017"  # scripted group (container) (typed FeaturePython)
  n = 1
  ref = N_element
FEATURE [App::DocumentObjectGroupPython] G4_PYRIDINE  # scripted group (container) (typed FeaturePython)
  Dunit = g/cm3
  Dvalue = 0.9819
  Group = -> [C_element099,H_element091,N_element038]
  conduct = 2
  density = 1
  expand = 3
  formula = G4_PYRIDINE
  name = G4_PYRIDINE
  specific = 4
FEATURE [App::DocumentObjectGroupPython] H_element092  label="H_element : 0.144"  # scripted group (container) (typed FeaturePython)
  n = 0.143711
FEATURE [App::DocumentObjectGroupPython] C_element100  label="C_element : 0.856"  # scripted group (container) (typed FeaturePython)
  n = 0.856289
FEATURE [App::DocumentObjectGroupPython] G4_RUBBER_BUTYL  # scripted group (container) (typed FeaturePython)
  Dunit = g/cm3
  Dvalue = 0.92
  Group = -> [H_element092,C_element100]
  conduct = 2
  density = 1
  expand = 3
  formula = G4_RUBBER_BUTYL
  name = G4_RUBBER_BUTYL
  specific = 4
FEATURE [App::DocumentObjectGroupPython] H_element093  label="H_element : 0.118"  # scripted group (container) (typed FeaturePython)
  n = 0.118371
FEATURE [App::DocumentObjectGroupPython] C_element101  label="C_element : 0.882"  # scripted group (container) (typed FeaturePython)
  n = 0.881629
FEATURE [App::DocumentObjectGroupPython] G4_RUBBER_NATURAL  # scripted group (container) (typed FeaturePython)
  Dunit = g/cm3
  Dvalue = 0.92
  Group = -> [H_element093,C_element101]
  conduct = 2
  density = 1
  expand = 3
  formula = G4_RUBBER_NATURAL
  name = G4_RUBBER_NATURAL
  specific = 4
FEATURE [App::DocumentObjectGroupPython] H_element094  label="H_element : 0.145"  # scripted group (container) (typed FeaturePython)
  n = 0.05692
FEATURE [App::DocumentObjectGroupPython] C_element102  label="C_element : 0.543"  # scripted group (container) (typed FeaturePython)
  n = 0.542646
FEATURE [App::DocumentObjectGroupPython] Cl_element021  label="Cl_element : 0.400"  # scripted group (container) (typed FeaturePython)
  n = 0.400434
FEATURE [App::DocumentObjectGroupPython] G4_RUBBER_NEOPRENE  # scripted group (container) (typed FeaturePython)
  Dunit = g/cm3
  Dvalue = 1.23
  Group = -> [H_element094,C_element102,Cl_element021]
  conduct = 2
  density = 1
  expand = 3
  formula = G4_RUBBER_NEOPRENE
  name = G4_RUBBER_NEOPRENE
  specific = 4
FEATURE [App::DocumentObjectGroupPython] Si_element006  label="Si_element : 1"  # scripted group (container) (typed FeaturePython)
  n = 1
  ref = Si_element
FEATURE [App::DocumentObjectGroupPython] O_element087  label="O_element : 048"  # scripted group (container) (typed FeaturePython)
  n = 2
  ref = O_element
FEATURE [App::DocumentObjectGroupPython] G4_SILICON_DIOXIDE  # scripted group (container) (typed FeaturePython)
  Dunit = g/cm3
  Dvalue = 2.32
  Group = -> [Si_element006,O_element087]
  conduct = 2
  density = 1
  expand = 3
  formula = G4_SILICON_DIOXIDE
  name = G4_SILICON_DIOXIDE
  specific = 4
FEATURE [App::DocumentObjectGroupPython] Ag_element002  label="Ag_element : 1"  # scripted group (container) (typed FeaturePython)
  n = 1
  ref = Ag_element
FEATURE [App::DocumentObjectGroupPython] Br_element005  label="Br_element : 003"  # scripted group (container) (typed FeaturePython)
  n = 1
  ref = Br_element
FEATURE [App::DocumentObjectGroupPython] G4_SILVER_BROMIDE  # scripted group (container) (typed FeaturePython)
  Dunit = g/cm3
  Dvalue = 6.473
  Group = -> [Ag_element002,Br_element005]
  conduct = 2
  density = 1
  expand = 3
  formula = G4_SILVER_BROMIDE
  name = G4_SILVER_BROMIDE
  specific = 4
FEATURE [App::DocumentObjectGroupPython] Ag_element003  label="Ag_element : 002"  # scripted group (container) (typed FeaturePython)
  n = 1
  ref = Ag_element
FEATURE [App::DocumentObjectGroupPython] Cl_element022  label="Cl_element : 011"  # scripted group (container) (typed FeaturePython)
  n = 1
  ref = Cl_element
FEATURE [App::DocumentObjectGroupPython] G4_SILVER_CHLORIDE  # scripted group (container) (typed FeaturePython)
  Dunit = g/cm3
  Dvalue = 5.56
  Group = -> [Ag_element003,Cl_element022]
  conduct = 2
  density = 1
  expand = 3
  formula = G4_SILVER_CHLORIDE
  name = G4_SILVER_CHLORIDE
  specific = 4
FEATURE [App::DocumentObjectGroupPython] Br_element006  label="Br_element : 0.423"  # scripted group (container) (typed FeaturePython)
  n = 0.422895
FEATURE [App::DocumentObjectGroupPython] Ag_element004  label="Ag_element : 0.574"  # scripted group (container) (typed FeaturePython)
  n = 0.573748
FEATURE [App::DocumentObjectGroupPython] I_element007  label="I_element : 0.649"  # scripted group (container) (typed FeaturePython)
  n = 0.003357
FEATURE [App::DocumentObjectGroupPython] G4_SILVER_HALIDES  # scripted group (container) (typed FeaturePython)
  Dunit = g/cm3
  Dvalue = 6.47
  Group = -> [Br_element006,Ag_element004,I_element007]
  conduct = 2
  density = 1
  expand = 3
  formula = G4_SILVER_HALIDES
  name = G4_SILVER_HALIDES
  specific = 4
FEATURE [App::DocumentObjectGroupPython] Ag_element005  label="Ag_element : 003"  # scripted group (container) (typed FeaturePython)
  n = 1
  ref = Ag_element
FEATURE [App::DocumentObjectGroupPython] I_element008  label="I_element : 004"  # scripted group (container) (typed FeaturePython)
  n = 1
  ref = I_element
FEATURE [App::DocumentObjectGroupPython] G4_SILVER_IODIDE  # scripted group (container) (typed FeaturePython)
  Dunit = g/cm3
  Dvalue = 6.01
  Group = -> [Ag_element005,I_element008]
  conduct = 2
  density = 1
  expand = 3
  formula = G4_SILVER_IODIDE
  name = G4_SILVER_IODIDE
  specific = 4
FEATURE [App::DocumentObjectGroupPython] H_element095  label="H_element : 0.100"  # scripted group (container) (typed FeaturePython)
  n = 0.1
FEATURE [App::DocumentObjectGroupPython] C_element103  label="C_element : 0.204"  # scripted group (container) (typed FeaturePython)
  n = 0.204
FEATURE [App::DocumentObjectGroupPython] N_element039  label="N_element : 0.759"  # scripted group (container) (typed FeaturePython)
  n = 0.042
FEATURE [App::DocumentObjectGroupPython] O_element088  label="O_element : 0.645"  # scripted group (container) (typed FeaturePython)
  n = 0.645
FEATURE [App::DocumentObjectGroupPython] Na_element013  label="Na_element : 0.100"  # scripted group (container) (typed FeaturePython)
  n = 0.002
FEATURE [App::DocumentObjectGroupPython] P_element009  label="P_element : 0.107"  # scripted group (container) (typed FeaturePython)
  n = 0.001
FEATURE [App::DocumentObjectGroupPython] S_element020  label="S_element : 0.021"  # scripted group (container) (typed FeaturePython)
  n = 0.002
FEATURE [App::DocumentObjectGroupPython] Cl_element023  label="Cl_element : 0.590"  # scripted group (container) (typed FeaturePython)
  n = 0.003
FEATURE [App::DocumentObjectGroupPython] K_element010  label="K_element : 0.001"  # scripted group (container) (typed FeaturePython)
  n = 0.001
FEATURE [App::DocumentObjectGroupPython] G4_SKIN_ICRP  # scripted group (container) (typed FeaturePython)
  Dunit = g/cm3
  Dvalue = 1.09
  Group = -> [H_element095,C_element103,N_element039,O_element088,Na_element013,P_element009,S_element020,Cl_element023,K_element010]
  conduct = 2
  density = 1
  expand = 3
  formula = G4_SKIN_ICRP
  name = G4_SKIN_ICRP
  specific = 4
FEATURE [App::DocumentObjectGroupPython] Na_element014  label="Na_element : 2"  # scripted group (container) (typed FeaturePython)
  n = 2
  ref = Na_element
FEATURE [App::DocumentObjectGroupPython] C_element104  label="C_element : 058"  # scripted group (container) (typed FeaturePython)
  n = 1
  ref = C_element
FEATURE [App::DocumentObjectGroupPython] O_element089  label="O_element : 049"  # scripted group (container) (typed FeaturePython)
  n = 3
  ref = O_element
FEATURE [App::DocumentObjectGroupPython] G4_SODIUM_CARBONATE  # scripted group (container) (typed FeaturePython)
  Dunit = g/cm3
  Dvalue = 2.532
  Group = -> [Na_element014,C_element104,O_element089]
  conduct = 2
  density = 1
  expand = 3
  formula = G4_SODIUM_CARBONATE
  name = G4_SODIUM_CARBONATE
  specific = 4
FEATURE [App::DocumentObjectGroupPython] Na_element015  label="Na_element : 1"  # scripted group (container) (typed FeaturePython)
  n = 1
  ref = Na_element
FEATURE [App::DocumentObjectGroupPython] I_element009  label="I_element : 005"  # scripted group (container) (typed FeaturePython)
  n = 1
  ref = I_element
FEATURE [App::DocumentObjectGroupPython] G4_SODIUM_IODIDE  # scripted group (container) (typed FeaturePython)
  Dunit = g/cm3
  Dvalue = 3.667
  Group = -> [Na_element015,I_element009]
  conduct = 2
  density = 1
  expand = 3
  formula = G4_SODIUM_IODIDE
  name = G4_SODIUM_IODIDE
  specific = 4
FEATURE [App::DocumentObjectGroupPython] Na_element016  label="Na_element : 003"  # scripted group (container) (typed FeaturePython)
  n = 2
  ref = Na_element
FEATURE [App::DocumentObjectGroupPython] O_element090  label="O_element : 050"  # scripted group (container) (typed FeaturePython)
  n = 1
  ref = O_element
FEATURE [App::DocumentObjectGroupPython] G4_SODIUM_MONOXIDE  # scripted group (container) (typed FeaturePython)
  Dunit = g/cm3
  Dvalue = 2.27
  Group = -> [Na_element016,O_element090]
  conduct = 2
  density = 1
  expand = 3
  formula = G4_SODIUM_MONOXIDE
  name = G4_SODIUM_MONOXIDE
  specific = 4
FEATURE [App::DocumentObjectGroupPython] Na_element017  label="Na_element : 004"  # scripted group (container) (typed FeaturePython)
  n = 1
  ref = Na_element
FEATURE [App::DocumentObjectGroupPython] N_element040  label="N_element : 018"  # scripted group (container) (typed FeaturePython)
  n = 1
  ref = N_element
FEATURE [App::DocumentObjectGroupPython] O_element091  label="O_element : 051"  # scripted group (container) (typed FeaturePython)
  n = 3
  ref = O_element
FEATURE [App::DocumentObjectGroupPython] G4_SODIUM_NITRATE  # scripted group (container) (typed FeaturePython)
  Dunit = g/cm3
  Dvalue = 2.261
  Group = -> [Na_element017,N_element040,O_element091]
  conduct = 2
  density = 1
  expand = 3
  formula = G4_SODIUM_NITRATE
  name = G4_SODIUM_NITRATE
  specific = 4
FEATURE [App::DocumentObjectGroupPython] C_element105  label="C_element : 059"  # scripted group (container) (typed FeaturePython)
  n = 14
  ref = C_element
FEATURE [App::DocumentObjectGroupPython] H_element096  label="H_element : 053"  # scripted group (container) (typed FeaturePython)
  n = 12
  ref = H_element
FEATURE [App::DocumentObjectGroupPython] G4_STILBENE  # scripted group (container) (typed FeaturePython)
  Dunit = g/cm3
  Dvalue = 0.9707
  Group = -> [C_element105,H_element096]
  conduct = 2
  density = 1
  expand = 3
  formula = G4_STILBENE
  name = G4_STILBENE
  specific = 4
FEATURE [App::DocumentObjectGroupPython] C_element106  label="C_element : 12"  # scripted group (container) (typed FeaturePython)
  n = 12
  ref = C_element
FEATURE [App::DocumentObjectGroupPython] H_element097  label="H_element : 22"  # scripted group (container) (typed FeaturePython)
  n = 22
  ref = H_element
FEATURE [App::DocumentObjectGroupPython] O_element092  label="O_element : 11"  # scripted group (container) (typed FeaturePython)
  n = 11
  ref = O_element
FEATURE [App::DocumentObjectGroupPython] G4_SUCROSE  # scripted group (container) (typed FeaturePython)
  Dunit = g/cm3
  Dvalue = 1.5805
  Group = -> [C_element106,H_element097,O_element092]
  conduct = 2
  density = 1
  expand = 3
  formula = G4_SUCROSE
  name = G4_SUCROSE
  specific = 4
FEATURE [App::DocumentObjectGroupPython] C_element107  label="C_element : 18"  # scripted group (container) (typed FeaturePython)
  n = 18
  ref = C_element
FEATURE [App::DocumentObjectGroupPython] H_element098  label="H_element : 054"  # scripted group (container) (typed FeaturePython)
  n = 14
  ref = H_element
FEATURE [App::DocumentObjectGroupPython] G4_TERPHENYL  # scripted group (container) (typed FeaturePython)
  Dunit = g/cm3
  Dvalue = 1.24
  Group = -> [C_element107,H_element098]
  conduct = 2
  density = 1
  expand = 3
  formula = G4_TERPHENYL
  name = G4_TERPHENYL
  specific = 4
FEATURE [App::DocumentObjectGroupPython] H_element099  label="H_element : 0.146"  # scripted group (container) (typed FeaturePython)
  n = 0.106
FEATURE [App::DocumentObjectGroupPython] C_element108  label="C_element : 0.883"  # scripted group (container) (typed FeaturePython)
  n = 0.099
FEATURE [App::DocumentObjectGroupPython] N_element041  label="N_element : 0.020"  # scripted group (container) (typed FeaturePython)
  n = 0.02
FEATURE [App::DocumentObjectGroupPython] O_element093  label="O_element : 0.766"  # scripted group (container) (typed FeaturePython)
  n = 0.766
FEATURE [App::DocumentObjectGroupPython] Na_element018  label="Na_element : 0.101"  # scripted group (container) (typed FeaturePython)
  n = 0.002
FEATURE [App::DocumentObjectGroupPython] P_element010  label="P_element : 0.108"  # scripted group (container) (typed FeaturePython)
  n = 0.001
FEATURE [App::DocumentObjectGroupPython] S_element021  label="S_element : 0.022"  # scripted group (container) (typed FeaturePython)
  n = 0.002
FEATURE [App::DocumentObjectGroupPython] Cl_element024  label="Cl_element : 0.002"  # scripted group (container) (typed FeaturePython)
  n = 0.002
FEATURE [App::DocumentObjectGroupPython] K_element011  label="K_element : 0.017"  # scripted group (container) (typed FeaturePython)
  n = 0.002
FEATURE [App::DocumentObjectGroupPython] G4_TESTIS_ICRP  # scripted group (container) (typed FeaturePython)
  Dunit = g/cm3
  Dvalue = 1.04
  Group = -> [H_element099,C_element108,N_element041,O_element093,Na_element018,P_element010,S_element021,Cl_element024,K_element011]
  conduct = 2
  density = 1
  expand = 3
  formula = G4_TESTIS_ICRP
  name = G4_TESTIS_ICRP
  specific = 4
FEATURE [App::DocumentObjectGroupPython] C_element109  label="C_element : 060"  # scripted group (container) (typed FeaturePython)
  n = 2
  ref = C_element
FEATURE [App::DocumentObjectGroupPython] Cl_element025  label="Cl_element : 012"  # scripted group (container) (typed FeaturePython)
  n = 4
  ref = Cl_element
FEATURE [App::DocumentObjectGroupPython] G4_TETRACHLOROETHYLENE  # scripted group (container) (typed FeaturePython)
  Dunit = g/cm3
  Dvalue = 1.625
  Group = -> [C_element109,Cl_element025]
  conduct = 2
  density = 1
  expand = 3
  formula = G4_TETRACHLOROETHYLENE
  name = G4_TETRACHLOROETHYLENE
  specific = 4
FEATURE [App::DocumentObjectGroupPython] Tl_element001  label="Tl_element : 1"  # scripted group (container) (typed FeaturePython)
  n = 1
  ref = Tl_element
FEATURE [App::DocumentObjectGroupPython] Cl_element026  label="Cl_element : 013"  # scripted group (container) (typed FeaturePython)
  n = 1
  ref = Cl_element
FEATURE [App::DocumentObjectGroupPython] G4_THALLIUM_CHLORIDE  # scripted group (container) (typed FeaturePython)
  Dunit = g/cm3
  Dvalue = 7.004
  Group = -> [Tl_element001,Cl_element026]
  conduct = 2
  density = 1
  expand = 3
  formula = G4_THALLIUM_CHLORIDE
  name = G4_THALLIUM_CHLORIDE
  specific = 4
FEATURE [App::DocumentObjectGroupPython] H_element100  label="H_element : 0.147"  # scripted group (container) (typed FeaturePython)
  n = 0.105
FEATURE [App::DocumentObjectGroupPython] C_element110  label="C_element : 0.256"  # scripted group (container) (typed FeaturePython)
  n = 0.256
FEATURE [App::DocumentObjectGroupPython] N_element042  label="N_element : 0.760"  # scripted group (container) (typed FeaturePython)
  n = 0.027
FEATURE [App::DocumentObjectGroupPython] O_element094  label="O_element : 0.602"  # scripted group (container) (typed FeaturePython)
  n = 0.602
FEATURE [App::DocumentObjectGroupPython] Na_element019  label="Na_element : 0.102"  # scripted group (container) (typed FeaturePython)
  n = 0.001
FEATURE [App::DocumentObjectGroupPython] P_element011  label="P_element : 0.109"  # scripted group (container) (typed FeaturePython)
  n = 0.002
FEATURE [App::DocumentObjectGroupPython] S_element022  label="S_element : 0.023"  # scripted group (container) (typed FeaturePython)
  n = 0.003
FEATURE [App::DocumentObjectGroupPython] Cl_element027  label="Cl_element : 0.591"  # scripted group (container) (typed FeaturePython)
  n = 0.002
FEATURE [App::DocumentObjectGroupPython] K_element012  label="K_element : 0.018"  # scripted group (container) (typed FeaturePython)
  n = 0.002
FEATURE [App::DocumentObjectGroupPython] G4_TISSUE_SOFT_ICRP  # scripted group (container) (typed FeaturePython)
  Dunit = g/cm3
  Dvalue = 1.03
  Group = -> [H_element100,C_element110,N_element042,O_element094,Na_element019,P_element011,S_element022,Cl_element027,K_element012]
  conduct = 2
  density = 1
  expand = 3
  formula = G4_TISSUE_SOFT_ICRP
  name = G4_TISSUE_SOFT_ICRP
  specific = 4
FEATURE [App::DocumentObjectGroupPython] H_element101  label="H_element : 0.148"  # scripted group (container) (typed FeaturePython)
  n = 0.101
FEATURE [App::DocumentObjectGroupPython] C_element111  label="C_element : 0.111"  # scripted group (container) (typed FeaturePython)
  n = 0.111
FEATURE [App::DocumentObjectGroupPython] N_element043  label="N_element : 0.026"  # scripted group (container) (typed FeaturePython)
  n = 0.026
FEATURE [App::DocumentObjectGroupPython] O_element095  label="O_element : 0.762"  # scripted group (container) (typed FeaturePython)
  n = 0.762
FEATURE [App::DocumentObjectGroupPython] G4_TISSUE_SOFT_ICRU_4  label="G4_TISSUE_SOFT_ICRU-4"  # scripted group (container) (typed FeaturePython)
  Dunit = g/cm3
  Dvalue = 1
  Group = -> [H_element101,C_element111,N_element043,O_element095]
  conduct = 2
  density = 1
  expand = 3
  formula = G4_TISSUE_SOFT_ICRU-4
  name = G4_TISSUE_SOFT_ICRU-4
  specific = 4
FEATURE [App::DocumentObjectGroupPython] H_element102  label="H_element : 0.149"  # scripted group (container) (typed FeaturePython)
  n = 0.101869
FEATURE [App::DocumentObjectGroupPython] C_element112  label="C_element : 0.456"  # scripted group (container) (typed FeaturePython)
  n = 0.456179
FEATURE [App::DocumentObjectGroupPython] N_element044  label="N_element : 0.761"  # scripted group (container) (typed FeaturePython)
  n = 0.035172
FEATURE [App::DocumentObjectGroupPython] O_element096  label="O_element : 0.407"  # scripted group (container) (typed FeaturePython)
  n = 0.40678
FEATURE [App::DocumentObjectGroupPython] G4_TISSUE_METHANE  label="G4_TISSUE-METHANE"  # scripted group (container) (typed FeaturePython)
  Dunit = g/cm3
  Dvalue = 0.00106409
  Group = -> [H_element102,C_element112,N_element044,O_element096]
  conduct = 2
  density = 1
  expand = 3
  formula = G4_TISSUE-METHANE
  name = G4_TISSUE-METHANE
  specific = 4
FEATURE [App::DocumentObjectGroupPython] H_element103  label="H_element : 0.103"  # scripted group (container) (typed FeaturePython)
  n = 0.102672
FEATURE [App::DocumentObjectGroupPython] C_element113  label="C_element : 0.569"  # scripted group (container) (typed FeaturePython)
  n = 0.56894
FEATURE [App::DocumentObjectGroupPython] N_element045  label="N_element : 0.762"  # scripted group (container) (typed FeaturePython)
  n = 0.035022
FEATURE [App::DocumentObjectGroupPython] O_element097  label="O_element : 0.293"  # scripted group (container) (typed FeaturePython)
  n = 0.293366
FEATURE [App::DocumentObjectGroupPython] G4_TISSUE_PROPANE  label="G4_TISSUE-PROPANE"  # scripted group (container) (typed FeaturePython)
  Dunit = g/cm3
  Dvalue = 0.00182628
  Group = -> [H_element103,C_element113,N_element045,O_element097]
  conduct = 2
  density = 1
  expand = 3
  formula = G4_TISSUE-PROPANE
  name = G4_TISSUE-PROPANE
  specific = 4
FEATURE [App::DocumentObjectGroupPython] Ti_element003  label="Ti_element : 1"  # scripted group (container) (typed FeaturePython)
  n = 1
  ref = Ti_element
FEATURE [App::DocumentObjectGroupPython] O_element098  label="O_element : 052"  # scripted group (container) (typed FeaturePython)
  n = 2
  ref = O_element
FEATURE [App::DocumentObjectGroupPython] G4_TITANIUM_DIOXIDE  # scripted group (container) (typed FeaturePython)
  Dunit = g/cm3
  Dvalue = 4.26
  Group = -> [Ti_element003,O_element098]
  conduct = 2
  density = 1
  expand = 3
  formula = G4_TITANIUM_DIOXIDE
  name = G4_TITANIUM_DIOXIDE
  specific = 4
FEATURE [App::DocumentObjectGroupPython] C_element114  label="C_element : 061"  # scripted group (container) (typed FeaturePython)
  n = 7
  ref = C_element
FEATURE [App::DocumentObjectGroupPython] H_element104  label="H_element : 055"  # scripted group (container) (typed FeaturePython)
  n = 8
  ref = H_element
FEATURE [App::DocumentObjectGroupPython] G4_TOLUENE  # scripted group (container) (typed FeaturePython)
  Dunit = g/cm3
  Dvalue = 0.8669
  Group = -> [C_element114,H_element104]
  conduct = 2
  density = 1
  expand = 3
  formula = G4_TOLUENE
  name = G4_TOLUENE
  specific = 4
FEATURE [App::DocumentObjectGroupPython] C_element115  label="C_element : 062"  # scripted group (container) (typed FeaturePython)
  n = 2
  ref = C_element
FEATURE [App::DocumentObjectGroupPython] H_element105  label="H_element : 056"  # scripted group (container) (typed FeaturePython)
  n = 1
  ref = H_element
FEATURE [App::DocumentObjectGroupPython] Cl_element028  label="Cl_element : 014"  # scripted group (container) (typed FeaturePython)
  n = 3
  ref = Cl_element
FEATURE [App::DocumentObjectGroupPython] G4_TRICHLOROETHYLENE  # scripted group (container) (typed FeaturePython)
  Dunit = g/cm3
  Dvalue = 1.46
  Group = -> [C_element115,H_element105,Cl_element028]
  conduct = 2
  density = 1
  expand = 3
  formula = G4_TRICHLOROETHYLENE
  name = G4_TRICHLOROETHYLENE
  specific = 4
FEATURE [App::DocumentObjectGroupPython] C_element116  label="C_element : 063"  # scripted group (container) (typed FeaturePython)
  n = 6
  ref = C_element
FEATURE [App::DocumentObjectGroupPython] H_element106  label="H_element : 15"  # scripted group (container) (typed FeaturePython)
  n = 15
  ref = H_element
FEATURE [App::DocumentObjectGroupPython] O_element099  label="O_element : 053"  # scripted group (container) (typed FeaturePython)
  n = 4
  ref = O_element
FEATURE [App::DocumentObjectGroupPython] P_element012  label="P_element : 1"  # scripted group (container) (typed FeaturePython)
  n = 1
  ref = P_element
FEATURE [App::DocumentObjectGroupPython] G4_TRIETHYL_PHOSPHATE  # scripted group (container) (typed FeaturePython)
  Dunit = g/cm3
  Dvalue = 1.07
  Group = -> [C_element116,H_element106,O_element099,P_element012]
  conduct = 2
  density = 1
  expand = 3
  formula = G4_TRIETHYL_PHOSPHATE
  name = G4_TRIETHYL_PHOSPHATE
  specific = 4
FEATURE [App::DocumentObjectGroupPython] W_element003  label="W_element : 003"  # scripted group (container) (typed FeaturePython)
  n = 1
  ref = W_element
FEATURE [App::DocumentObjectGroupPython] F_element017  label="F_element : 6"  # scripted group (container) (typed FeaturePython)
  n = 6
  ref = F_element
FEATURE [App::DocumentObjectGroupPython] G4_TUNGSTEN_HEXAFLUORIDE  # scripted group (container) (typed FeaturePython)
  Dunit = g/cm3
  Dvalue = 2.4
  Group = -> [W_element003,F_element017]
  conduct = 2
  density = 1
  expand = 3
  formula = G4_TUNGSTEN_HEXAFLUORIDE
  name = G4_TUNGSTEN_HEXAFLUORIDE
  specific = 4
FEATURE [App::DocumentObjectGroupPython] U_element001  label="U_element : 1"  # scripted group (container) (typed FeaturePython)
  n = 1
  ref = U_element
FEATURE [App::DocumentObjectGroupPython] C_element117  label="C_element : 064"  # scripted group (container) (typed FeaturePython)
  n = 2
  ref = C_element
FEATURE [App::DocumentObjectGroupPython] G4_URANIUM_DICARBIDE  # scripted group (container) (typed FeaturePython)
  Dunit = g/cm3
  Dvalue = 11.28
  Group = -> [U_element001,C_element117]
  conduct = 2
  density = 1
  expand = 3
  formula = G4_URANIUM_DICARBIDE
  name = G4_URANIUM_DICARBIDE
  specific = 4
FEATURE [App::DocumentObjectGroupPython] U_element002  label="U_element : 002"  # scripted group (container) (typed FeaturePython)
  n = 1
  ref = U_element
FEATURE [App::DocumentObjectGroupPython] C_element118  label="C_element : 065"  # scripted group (container) (typed FeaturePython)
  n = 1
  ref = C_element
FEATURE [App::DocumentObjectGroupPython] G4_URANIUM_MONOCARBIDE  # scripted group (container) (typed FeaturePython)
  Dunit = g/cm3
  Dvalue = 13.63
  Group = -> [U_element002,C_element118]
  conduct = 2
  density = 1
  expand = 3
  formula = G4_URANIUM_MONOCARBIDE
  name = G4_URANIUM_MONOCARBIDE
  specific = 4
FEATURE [App::DocumentObjectGroupPython] U_element003  label="U_element : 003"  # scripted group (container) (typed FeaturePython)
  n = 1
  ref = U_element
FEATURE [App::DocumentObjectGroupPython] O_element100  label="O_element : 054"  # scripted group (container) (typed FeaturePython)
  n = 2
  ref = O_element
FEATURE [App::DocumentObjectGroupPython] G4_URANIUM_OXIDE  # scripted group (container) (typed FeaturePython)
  Dunit = g/cm3
  Dvalue = 10.96
  Group = -> [U_element003,O_element100]
  conduct = 2
  density = 1
  expand = 3
  formula = G4_URANIUM_OXIDE
  name = G4_URANIUM_OXIDE
  specific = 4
FEATURE [App::DocumentObjectGroupPython] C_element119  label="C_element : 066"  # scripted group (container) (typed FeaturePython)
  n = 1
  ref = C_element
FEATURE [App::DocumentObjectGroupPython] H_element107  label="H_element : 057"  # scripted group (container) (typed FeaturePython)
  n = 4
  ref = H_element
FEATURE [App::DocumentObjectGroupPython] N_element046  label="N_element : 019"  # scripted group (container) (typed FeaturePython)
  n = 2
  ref = N_element
FEATURE [App::DocumentObjectGroupPython] O_element101  label="O_element : 055"  # scripted group (container) (typed FeaturePython)
  n = 1
  ref = O_element
FEATURE [App::DocumentObjectGroupPython] G4_UREA  # scripted group (container) (typed FeaturePython)
  Dunit = g/cm3
  Dvalue = 1.323
  Group = -> [C_element119,H_element107,N_element046,O_element101]
  conduct = 2
  density = 1
  expand = 3
  formula = G4_UREA
  name = G4_UREA
  specific = 4
FEATURE [App::DocumentObjectGroupPython] C_element120  label="C_element : 067"  # scripted group (container) (typed FeaturePython)
  n = 5
  ref = C_element
FEATURE [App::DocumentObjectGroupPython] H_element108  label="H_element : 058"  # scripted group (container) (typed FeaturePython)
  n = 11
  ref = H_element
FEATURE [App::DocumentObjectGroupPython] N_element047  label="N_element : 020"  # scripted group (container) (typed FeaturePython)
  n = 1
  ref = N_element
FEATURE [App::DocumentObjectGroupPython] O_element102  label="O_element : 056"  # scripted group (container) (typed FeaturePython)
  n = 2
  ref = O_element
FEATURE [App::DocumentObjectGroupPython] G4_VALINE  # scripted group (container) (typed FeaturePython)
  Dunit = g/cm3
  Dvalue = 1.23
  Group = -> [C_element120,H_element108,N_element047,O_element102]
  conduct = 2
  density = 1
  expand = 3
  formula = G4_VALINE
  name = G4_VALINE
  specific = 4
FEATURE [App::DocumentObjectGroupPython] H_element109  label="H_element : 0.009"  # scripted group (container) (typed FeaturePython)
  n = 0.009417
FEATURE [App::DocumentObjectGroupPython] C_element121  label="C_element : 0.281"  # scripted group (container) (typed FeaturePython)
  n = 0.280555
FEATURE [App::DocumentObjectGroupPython] F_element018  label="F_element : 0.710"  # scripted group (container) (typed FeaturePython)
  n = 0.710028
FEATURE [App::DocumentObjectGroupPython] G4_VITON  # scripted group (container) (typed FeaturePython)
  Dunit = g/cm3
  Dvalue = 1.8
  Group = -> [H_element109,C_element121,F_element018]
  conduct = 2
  density = 1
  expand = 3
  formula = G4_VITON
  name = G4_VITON
  specific = 4
FEATURE [App::DocumentObjectGroupPython] H_element110  label="H_element : 059"  # scripted group (container) (typed FeaturePython)
  n = 2
  ref = H_element
FEATURE [App::DocumentObjectGroupPython] O_element103  label="O_element : 057"  # scripted group (container) (typed FeaturePython)
  n = 1
  ref = O_element
FEATURE [App::DocumentObjectGroupPython] G4_WATER  # scripted group (container) (typed FeaturePython)
  Dunit = g/cm3
  Dvalue = 1
  Group = -> [H_element110,O_element103]
  conduct = 2
  density = 1
  expand = 3
  formula = G4_WATER
  name = G4_WATER
  specific = 4
FEATURE [App::DocumentObjectGroupPython] H_element111  label="H_element : 060"  # scripted group (container) (typed FeaturePython)
  n = 2
  ref = H_element
FEATURE [App::DocumentObjectGroupPython] O_element104  label="O_element : 058"  # scripted group (container) (typed FeaturePython)
  n = 1
  ref = O_element
FEATURE [App::DocumentObjectGroupPython] G4_WATER_VAPOR  # scripted group (container) (typed FeaturePython)
  Dunit = g/cm3
  Dvalue = 0.000756182
  Group = -> [H_element111,O_element104]
  conduct = 2
  density = 1
  expand = 3
  formula = G4_WATER_VAPOR
  name = G4_WATER_VAPOR
  specific = 4
FEATURE [App::DocumentObjectGroupPython] C_element122  label="C_element : 068"  # scripted group (container) (typed FeaturePython)
  n = 8
  ref = C_element
FEATURE [App::DocumentObjectGroupPython] H_element112  label="H_element : 061"  # scripted group (container) (typed FeaturePython)
  n = 10
  ref = H_element
FEATURE [App::DocumentObjectGroupPython] G4_XYLENE  # scripted group (container) (typed FeaturePython)
  Dunit = g/cm3
  Dvalue = 0.87
  Group = -> [C_element122,H_element112]
  conduct = 2
  density = 1
  expand = 3
  formula = G4_XYLENE
  name = G4_XYLENE
  specific = 4
FEATURE [App::DocumentObjectGroupPython] C_element123  label="C_element : 069"  # scripted group (container) (typed FeaturePython)
  n = 1
  ref = C_element
FEATURE [App::DocumentObjectGroupPython] G4_GRAPHITE  # scripted group (container) (typed FeaturePython)
  Dunit = g/cm3
  Dvalue = 2.21
  Group = -> [C_element123]
  conduct = 2
  density = 1
  expand = 3
  formula = G4_GRAPHITE
  name = G4_GRAPHITE
  specific = 4
FEATURE [App::DocumentObjectGroupPython] NIST  # scripted group (container) (typed FeaturePython)
  Group = -> [G4_A_150_TISSUE,G4_ACETONE,G4_ACETYLENE,G4_ADENINE,G4_ADIPOSE_TISSUE_ICRP,G4_AIR,G4_ALANINE,G4_ALUMINUM_OXIDE,G4_AMBER,G4_AMMONIA,G4_ANILINE,G4_ANTHRACENE,G4_B_100_BONE,G4_BAKELITE,G4_BARIUM_FLUORIDE,G4_BARIUM_SULFATE,G4_BENZENE,G4_BERYLLIUM_OXIDE,G4_BGO,G4_BLOOD_ICRP,G4_BONE_COMPACT_ICRU,G4_BONE_CORTICAL_ICRP,G4_BORON_CARBIDE,G4_BORON_OXIDE,G4_BRAIN_ICRP,G4_BUTANE,G4_N_BUTYL_ALCOHOL,G4_C_552,+152 more]
FEATURE [App::DocumentObjectGroupPython] H_element113  label="H_element : 062"  # scripted group (container) (typed FeaturePython)
  n = 1
  ref = H_element
FEATURE [App::DocumentObjectGroupPython] G4_H  # scripted group (container) (typed FeaturePython)
  Dunit = g/cm3
  Dvalue = 8.3748e-05
  Group = -> [H_element113]
  conduct = 2
  density = 1
  expand = 3
  formula = H
  name = G4_H
  specific = 4
FEATURE [App::DocumentObjectGroupPython] He_element001  label="He_element : 1"  # scripted group (container) (typed FeaturePython)
  n = 1
  ref = He_element
FEATURE [App::DocumentObjectGroupPython] G4_He  # scripted group (container) (typed FeaturePython)
  Dunit = g/cm3
  Dvalue = 0.000166322
  Group = -> [He_element001]
  conduct = 2
  density = 1
  expand = 3
  formula = He
  name = G4_He
  specific = 4
FEATURE [App::DocumentObjectGroupPython] Li_element008  label="Li_element : 008"  # scripted group (container) (typed FeaturePython)
  n = 1
  ref = Li_element
FEATURE [App::DocumentObjectGroupPython] G4_Li  # scripted group (container) (typed FeaturePython)
  Dunit = g/cm3
  Dvalue = 0.534
  Group = -> [Li_element008]
  conduct = 2
  density = 1
  expand = 3
  formula = Li
  name = G4_Li
  specific = 4
FEATURE [App::DocumentObjectGroupPython] Be_element002  label="Be_element : 002"  # scripted group (container) (typed FeaturePython)
  n = 1
  ref = Be_element
FEATURE [App::DocumentObjectGroupPython] G4_Be  # scripted group (container) (typed FeaturePython)
  Dunit = g/cm3
  Dvalue = 1.848
  Group = -> [Be_element002]
  conduct = 2
  density = 1
  expand = 3
  formula = Be
  name = G4_Be
  specific = 4
FEATURE [App::DocumentObjectGroupPython] B_element007  label="B_element : 007"  # scripted group (container) (typed FeaturePython)
  n = 1
  ref = B_element
FEATURE [App::DocumentObjectGroupPython] G4_B  # scripted group (container) (typed FeaturePython)
  Dunit = g/cm3
  Dvalue = 2.37
  Group = -> [B_element007]
  conduct = 2
  density = 1
  expand = 3
  formula = B
  name = G4_B
  specific = 4
FEATURE [App::DocumentObjectGroupPython] C_element124  label="C_element : 070"  # scripted group (container) (typed FeaturePython)
  n = 1
  ref = C_element
FEATURE [App::DocumentObjectGroupPython] G4_C  # scripted group (container) (typed FeaturePython)
  Dunit = g/cm3
  Dvalue = 2
  Group = -> [C_element124]
  conduct = 2
  density = 1
  expand = 3
  formula = C
  name = G4_C
  specific = 4
FEATURE [App::DocumentObjectGroupPython] N_element048  label="N_element : 021"  # scripted group (container) (typed FeaturePython)
  n = 1
  ref = N_element
FEATURE [App::DocumentObjectGroupPython] G4_N  # scripted group (container) (typed FeaturePython)
  Dunit = g/cm3
  Dvalue = 0.0011652
  Group = -> [N_element048]
  conduct = 2
  density = 1
  expand = 3
  formula = N
  name = G4_N
  specific = 4
FEATURE [App::DocumentObjectGroupPython] O_element105  label="O_element : 059"  # scripted group (container) (typed FeaturePython)
  n = 1
  ref = O_element
FEATURE [App::DocumentObjectGroupPython] G4_O  # scripted group (container) (typed FeaturePython)
  Dunit = g/cm3
  Dvalue = 0.00133151
  Group = -> [O_element105]
  conduct = 2
  density = 1
  expand = 3
  formula = O
  name = G4_O
  specific = 4
FEATURE [App::DocumentObjectGroupPython] F_element019  label="F_element : 008"  # scripted group (container) (typed FeaturePython)
  n = 1
  ref = F_element
FEATURE [App::DocumentObjectGroupPython] G4_F  # scripted group (container) (typed FeaturePython)
  Dunit = g/cm3
  Dvalue = 0.00158029
  Group = -> [F_element019]
  conduct = 2
  density = 1
  expand = 3
  formula = F
  name = G4_F
  specific = 4
FEATURE [App::DocumentObjectGroupPython] Ne_element001  label="Ne_element : 1"  # scripted group (container) (typed FeaturePython)
  n = 1
  ref = Ne_element
FEATURE [App::DocumentObjectGroupPython] G4_Ne  # scripted group (container) (typed FeaturePython)
  Dunit = g/cm3
  Dvalue = 0.000838505
  Group = -> [Ne_element001]
  conduct = 2
  density = 1
  expand = 3
  formula = Ne
  name = G4_Ne
  specific = 4
FEATURE [App::DocumentObjectGroupPython] Na_element020  label="Na_element : 005"  # scripted group (container) (typed FeaturePython)
  n = 1
  ref = Na_element
FEATURE [App::DocumentObjectGroupPython] G4_Na  # scripted group (container) (typed FeaturePython)
  Dunit = g/cm3
  Dvalue = 0.971
  Group = -> [Na_element020]
  conduct = 2
  density = 1
  expand = 3
  formula = Na
  name = G4_Na
  specific = 4
FEATURE [App::DocumentObjectGroupPython] Mg_element011  label="Mg_element : 005"  # scripted group (container) (typed FeaturePython)
  n = 1
  ref = Mg_element
FEATURE [App::DocumentObjectGroupPython] G4_Mg  # scripted group (container) (typed FeaturePython)
  Dunit = g/cm3
  Dvalue = 1.74
  Group = -> [Mg_element011]
  conduct = 2
  density = 1
  expand = 3
  formula = Mg
  name = G4_Mg
  specific = 4
FEATURE [App::DocumentObjectGroupPython] Al_element004  label="Al_element : 1"  # scripted group (container) (typed FeaturePython)
  n = 1
  ref = Al_element
FEATURE [App::DocumentObjectGroupPython] G4_Al  # scripted group (container) (typed FeaturePython)
  Dunit = g/cm3
  Dvalue = 2.699
  Group = -> [Al_element004]
  conduct = 2
  density = 1
  expand = 3
  formula = Al
  name = G4_Al
  specific = 4
FEATURE [App::DocumentObjectGroupPython] Si_element007  label="Si_element : 002"  # scripted group (container) (typed FeaturePython)
  n = 1
  ref = Si_element
FEATURE [App::DocumentObjectGroupPython] G4_Si  # scripted group (container) (typed FeaturePython)
  Dunit = g/cm3
  Dvalue = 2.33
  Group = -> [Si_element007]
  conduct = 2
  density = 1
  expand = 3
  formula = Si
  name = G4_Si
  specific = 4
FEATURE [App::DocumentObjectGroupPython] P_element013  label="P_element : 002"  # scripted group (container) (typed FeaturePython)
  n = 1
  ref = P_element
FEATURE [App::DocumentObjectGroupPython] G4_P  # scripted group (container) (typed FeaturePython)
  Dunit = g/cm3
  Dvalue = 2.2
  Group = -> [P_element013]
  conduct = 2
  density = 1
  expand = 3
  formula = P
  name = G4_P
  specific = 4
FEATURE [App::DocumentObjectGroupPython] S_element023  label="S_element : 007"  # scripted group (container) (typed FeaturePython)
  n = 1
  ref = S_element
FEATURE [App::DocumentObjectGroupPython] G4_S  # scripted group (container) (typed FeaturePython)
  Dunit = g/cm3
  Dvalue = 2
  Group = -> [S_element023]
  conduct = 2
  density = 1
  expand = 3
  formula = S
  name = G4_S
  specific = 4
FEATURE [App::DocumentObjectGroupPython] Cl_element029  label="Cl_element : 015"  # scripted group (container) (typed FeaturePython)
  n = 1
  ref = Cl_element
FEATURE [App::DocumentObjectGroupPython] G4_Cl  # scripted group (container) (typed FeaturePython)
  Dunit = g/cm3
  Dvalue = 0.00299473
  Group = -> [Cl_element029]
  conduct = 2
  density = 1
  expand = 3
  formula = Cl
  name = G4_Cl
  specific = 4
FEATURE [App::DocumentObjectGroupPython] Ar_element002  label="Ar_element : 1"  # scripted group (container) (typed FeaturePython)
  n = 1
  ref = Ar_element
FEATURE [App::DocumentObjectGroupPython] G4_Ar  # scripted group (container) (typed FeaturePython)
  Dunit = g/cm3
  Dvalue = 0.00166201
  Group = -> [Ar_element002]
  conduct = 2
  density = 1
  expand = 3
  formula = Ar
  name = G4_Ar
  specific = 4
FEATURE [App::DocumentObjectGroupPython] K_element013  label="K_element : 003"  # scripted group (container) (typed FeaturePython)
  n = 1
  ref = K_element
FEATURE [App::DocumentObjectGroupPython] G4_K  # scripted group (container) (typed FeaturePython)
  Dunit = g/cm3
  Dvalue = 0.862
  Group = -> [K_element013]
  conduct = 2
  density = 1
  expand = 3
  formula = K
  name = G4_K
  specific = 4
FEATURE [App::DocumentObjectGroupPython] Ca_element014  label="Ca_element : 007"  # scripted group (container) (typed FeaturePython)
  n = 1
  ref = Ca_element
FEATURE [App::DocumentObjectGroupPython] G4_Ca  # scripted group (container) (typed FeaturePython)
  Dunit = g/cm3
  Dvalue = 1.55
  Group = -> [Ca_element014]
  conduct = 2
  density = 1
  expand = 3
  formula = Ca
  name = G4_Ca
  specific = 4
FEATURE [App::DocumentObjectGroupPython] Sc_element001  label="Sc_element : 1"  # scripted group (container) (typed FeaturePython)
  n = 1
  ref = Sc_element
FEATURE [App::DocumentObjectGroupPython] G4_Sc  # scripted group (container) (typed FeaturePython)
  Dunit = g/cm3
  Dvalue = 2.989
  Group = -> [Sc_element001]
  conduct = 2
  density = 1
  expand = 3
  formula = Sc
  name = G4_Sc
  specific = 4
FEATURE [App::DocumentObjectGroupPython] Ti_element004  label="Ti_element : 002"  # scripted group (container) (typed FeaturePython)
  n = 1
  ref = Ti_element
FEATURE [App::DocumentObjectGroupPython] G4_Ti  # scripted group (container) (typed FeaturePython)
  Dunit = g/cm3
  Dvalue = 4.54
  Group = -> [Ti_element004]
  conduct = 2
  density = 1
  expand = 3
  formula = Ti
  name = G4_Ti
  specific = 4
FEATURE [App::DocumentObjectGroupPython] V_element001  label="V_element : 1"  # scripted group (container) (typed FeaturePython)
  n = 1
  ref = V_element
FEATURE [App::DocumentObjectGroupPython] G4_V  # scripted group (container) (typed FeaturePython)
  Dunit = g/cm3
  Dvalue = 6.11
  Group = -> [V_element001]
  conduct = 2
  density = 1
  expand = 3
  formula = V
  name = G4_V
  specific = 4
FEATURE [App::DocumentObjectGroupPython] Cr_element001  label="Cr_element : 1"  # scripted group (container) (typed FeaturePython)
  n = 1
  ref = Cr_element
FEATURE [App::DocumentObjectGroupPython] G4_Cr  # scripted group (container) (typed FeaturePython)
  Dunit = g/cm3
  Dvalue = 7.18
  Group = -> [Cr_element001]
  conduct = 2
  density = 1
  expand = 3
  formula = Cr
  name = G4_Cr
  specific = 4
FEATURE [App::DocumentObjectGroupPython] Mn_element001  label="Mn_element : 1"  # scripted group (container) (typed FeaturePython)
  n = 1
  ref = Mn_element
FEATURE [App::DocumentObjectGroupPython] G4_Mn  # scripted group (container) (typed FeaturePython)
  Dunit = g/cm3
  Dvalue = 7.44
  Group = -> [Mn_element001]
  conduct = 2
  density = 1
  expand = 3
  formula = Mn
  name = G4_Mn
  specific = 4
FEATURE [App::DocumentObjectGroupPython] Fe_element007  label="Fe_element : 004"  # scripted group (container) (typed FeaturePython)
  n = 1
  ref = Fe_element
FEATURE [App::DocumentObjectGroupPython] G4_Fe  # scripted group (container) (typed FeaturePython)
  Dunit = g/cm3
  Dvalue = 7.874
  Group = -> [Fe_element007]
  conduct = 2
  density = 1
  expand = 3
  formula = Fe
  name = G4_Fe
  specific = 4
FEATURE [App::DocumentObjectGroupPython] Co_element001  label="Co_element : 1"  # scripted group (container) (typed FeaturePython)
  n = 1
  ref = Co_element
FEATURE [App::DocumentObjectGroupPython] G4_Co  # scripted group (container) (typed FeaturePython)
  Dunit = g/cm3
  Dvalue = 8.9
  Group = -> [Co_element001]
  conduct = 2
  density = 1
  expand = 3
  formula = Co
  name = G4_Co
  specific = 4
FEATURE [App::DocumentObjectGroupPython] Ni_element001  label="Ni_element : 1"  # scripted group (container) (typed FeaturePython)
  n = 1
  ref = Ni_element
FEATURE [App::DocumentObjectGroupPython] G4_Ni  # scripted group (container) (typed FeaturePython)
  Dunit = g/cm3
  Dvalue = 8.902
  Group = -> [Ni_element001]
  conduct = 2
  density = 1
  expand = 3
  formula = Ni
  name = G4_Ni
  specific = 4
FEATURE [App::DocumentObjectGroupPython] Cu_element001  label="Cu_element : 1"  # scripted group (container) (typed FeaturePython)
  n = 1
  ref = Cu_element
FEATURE [App::DocumentObjectGroupPython] G4_Cu  # scripted group (container) (typed FeaturePython)
  Dunit = g/cm3
  Dvalue = 8.96
  Group = -> [Cu_element001]
  conduct = 2
  density = 1
  expand = 3
  formula = Cu
  name = G4_Cu
  specific = 4
FEATURE [App::DocumentObjectGroupPython] Zn_element001  label="Zn_element : 1"  # scripted group (container) (typed FeaturePython)
  n = 1
  ref = Zn_element
FEATURE [App::DocumentObjectGroupPython] G4_Zn  # scripted group (container) (typed FeaturePython)
  Dunit = g/cm3
  Dvalue = 7.133
  Group = -> [Zn_element001]
  conduct = 2
  density = 1
  expand = 3
  formula = Zn
  name = G4_Zn
  specific = 4
FEATURE [App::DocumentObjectGroupPython] Ga_element002  label="Ga_element : 002"  # scripted group (container) (typed FeaturePython)
  n = 1
  ref = Ga_element
FEATURE [App::DocumentObjectGroupPython] G4_Ga  # scripted group (container) (typed FeaturePython)
  Dunit = g/cm3
  Dvalue = 5.904
  Group = -> [Ga_element002]
  conduct = 2
  density = 1
  expand = 3
  formula = Ga
  name = G4_Ga
  specific = 4
FEATURE [App::DocumentObjectGroupPython] Ge_element002  label="Ge_element : 1"  # scripted group (container) (typed FeaturePython)
  n = 1
  ref = Ge_element
FEATURE [App::DocumentObjectGroupPython] G4_Ge  # scripted group (container) (typed FeaturePython)
  Dunit = g/cm3
  Dvalue = 5.323
  Group = -> [Ge_element002]
  conduct = 2
  density = 1
  expand = 3
  formula = Ge
  name = G4_Ge
  specific = 4
FEATURE [App::DocumentObjectGroupPython] As_element003  label="As_element : 002"  # scripted group (container) (typed FeaturePython)
  n = 1
  ref = As_element
FEATURE [App::DocumentObjectGroupPython] G4_As  # scripted group (container) (typed FeaturePython)
  Dunit = g/cm3
  Dvalue = 5.73
  Group = -> [As_element003]
  conduct = 2
  density = 1
  expand = 3
  formula = As
  name = G4_As
  specific = 4
FEATURE [App::DocumentObjectGroupPython] Se_element001  label="Se_element : 1"  # scripted group (container) (typed FeaturePython)
  n = 1
  ref = Se_element
FEATURE [App::DocumentObjectGroupPython] G4_Se  # scripted group (container) (typed FeaturePython)
  Dunit = g/cm3
  Dvalue = 4.5
  Group = -> [Se_element001]
  conduct = 2
  density = 1
  expand = 3
  formula = Se
  name = G4_Se
  specific = 4
FEATURE [App::DocumentObjectGroupPython] Br_element007  label="Br_element : 004"  # scripted group (container) (typed FeaturePython)
  n = 1
  ref = Br_element
FEATURE [App::DocumentObjectGroupPython] G4_Br  # scripted group (container) (typed FeaturePython)
  Dunit = g/cm3
  Dvalue = 0.0070721
  Group = -> [Br_element007]
  conduct = 2
  density = 1
  expand = 3
  formula = Br
  name = G4_Br
  specific = 4
FEATURE [App::DocumentObjectGroupPython] Kr_element001  label="Kr_element : 1"  # scripted group (container) (typed FeaturePython)
  n = 1
  ref = Kr_element
FEATURE [App::DocumentObjectGroupPython] G4_Kr  # scripted group (container) (typed FeaturePython)
  Dunit = g/cm3
  Dvalue = 0.00347832
  Group = -> [Kr_element001]
  conduct = 2
  density = 1
  expand = 3
  formula = Kr
  name = G4_Kr
  specific = 4
FEATURE [App::DocumentObjectGroupPython] Rb_element001  label="Rb_element : 1"  # scripted group (container) (typed FeaturePython)
  n = 1
  ref = Rb_element
FEATURE [App::DocumentObjectGroupPython] G4_Rb  # scripted group (container) (typed FeaturePython)
  Dunit = g/cm3
  Dvalue = 1.532
  Group = -> [Rb_element001]
  conduct = 2
  density = 1
  expand = 3
  formula = Rb
  name = G4_Rb
  specific = 4
FEATURE [App::DocumentObjectGroupPython] Sr_element001  label="Sr_element : 1"  # scripted group (container) (typed FeaturePython)
  n = 1
  ref = Sr_element
FEATURE [App::DocumentObjectGroupPython] G4_Sr  # scripted group (container) (typed FeaturePython)
  Dunit = g/cm3
  Dvalue = 2.54
  Group = -> [Sr_element001]
  conduct = 2
  density = 1
  expand = 3
  formula = Sr
  name = G4_Sr
  specific = 4
FEATURE [App::DocumentObjectGroupPython] Y_element001  label="Y_element : 1"  # scripted group (container) (typed FeaturePython)
  n = 1
  ref = Y_element
FEATURE [App::DocumentObjectGroupPython] G4_Y  # scripted group (container) (typed FeaturePython)
  Dunit = g/cm3
  Dvalue = 4.469
  Group = -> [Y_element001]
  conduct = 2
  density = 1
  expand = 3
  formula = Y
  name = G4_Y
  specific = 4
FEATURE [App::DocumentObjectGroupPython] Zr_element001  label="Zr_element : 1"  # scripted group (container) (typed FeaturePython)
  n = 1
  ref = Zr_element
FEATURE [App::DocumentObjectGroupPython] G4_Zr  # scripted group (container) (typed FeaturePython)
  Dunit = g/cm3
  Dvalue = 6.506
  Group = -> [Zr_element001]
  conduct = 2
  density = 1
  expand = 3
  formula = Zr
  name = G4_Zr
  specific = 4
FEATURE [App::DocumentObjectGroupPython] Nb_element001  label="Nb_element : 1"  # scripted group (container) (typed FeaturePython)
  n = 1
  ref = Nb_element
FEATURE [App::DocumentObjectGroupPython] G4_Nb  # scripted group (container) (typed FeaturePython)
  Dunit = g/cm3
  Dvalue = 8.57
  Group = -> [Nb_element001]
  conduct = 2
  density = 1
  expand = 3
  formula = Nb
  name = G4_Nb
  specific = 4
FEATURE [App::DocumentObjectGroupPython] Mo_element001  label="Mo_element : 1"  # scripted group (container) (typed FeaturePython)
  n = 1
  ref = Mo_element
FEATURE [App::DocumentObjectGroupPython] G4_Mo  # scripted group (container) (typed FeaturePython)
  Dunit = g/cm3
  Dvalue = 10.22
  Group = -> [Mo_element001]
  conduct = 2
  density = 1
  expand = 3
  formula = Mo
  name = G4_Mo
  specific = 4
FEATURE [App::DocumentObjectGroupPython] Tc_element001  label="Tc_element : 1"  # scripted group (container) (typed FeaturePython)
  n = 1
  ref = Tc_element
FEATURE [App::DocumentObjectGroupPython] G4_Tc  # scripted group (container) (typed FeaturePython)
  Dunit = g/cm3
  Dvalue = 11.5
  Group = -> [Tc_element001]
  conduct = 2
  density = 1
  expand = 3
  formula = Tc
  name = G4_Tc
  specific = 4
FEATURE [App::DocumentObjectGroupPython] Ru_element001  label="Ru_element : 1"  # scripted group (container) (typed FeaturePython)
  n = 1
  ref = Ru_element
FEATURE [App::DocumentObjectGroupPython] G4_Ru  # scripted group (container) (typed FeaturePython)
  Dunit = g/cm3
  Dvalue = 12.41
  Group = -> [Ru_element001]
  conduct = 2
  density = 1
  expand = 3
  formula = Ru
  name = G4_Ru
  specific = 4
FEATURE [App::DocumentObjectGroupPython] Rh_element001  label="Rh_element : 1"  # scripted group (container) (typed FeaturePython)
  n = 1
  ref = Rh_element
FEATURE [App::DocumentObjectGroupPython] G4_Rh  # scripted group (container) (typed FeaturePython)
  Dunit = g/cm3
  Dvalue = 12.41
  Group = -> [Rh_element001]
  conduct = 2
  density = 1
  expand = 3
  formula = Rh
  name = G4_Rh
  specific = 4
FEATURE [App::DocumentObjectGroupPython] Pd_element001  label="Pd_element : 1"  # scripted group (container) (typed FeaturePython)
  n = 1
  ref = Pd_element
FEATURE [App::DocumentObjectGroupPython] G4_Pd  # scripted group (container) (typed FeaturePython)
  Dunit = g/cm3
  Dvalue = 12.02
  Group = -> [Pd_element001]
  conduct = 2
  density = 1
  expand = 3
  formula = Pd
  name = G4_Pd
  specific = 4
FEATURE [App::DocumentObjectGroupPython] Ag_element006  label="Ag_element : 004"  # scripted group (container) (typed FeaturePython)
  n = 1
  ref = Ag_element
FEATURE [App::DocumentObjectGroupPython] G4_Ag  # scripted group (container) (typed FeaturePython)
  Dunit = g/cm3
  Dvalue = 10.5
  Group = -> [Ag_element006]
  conduct = 2
  density = 1
  expand = 3
  formula = Ag
  name = G4_Ag
  specific = 4
FEATURE [App::DocumentObjectGroupPython] Cd_element003  label="Cd_element : 003"  # scripted group (container) (typed FeaturePython)
  n = 1
  ref = Cd_element
FEATURE [App::DocumentObjectGroupPython] G4_Cd  # scripted group (container) (typed FeaturePython)
  Dunit = g/cm3
  Dvalue = 8.65
  Group = -> [Cd_element003]
  conduct = 2
  density = 1
  expand = 3
  formula = Cd
  name = G4_Cd
  specific = 4
FEATURE [App::DocumentObjectGroupPython] In_element001  label="In_element : 1"  # scripted group (container) (typed FeaturePython)
  n = 1
  ref = In_element
FEATURE [App::DocumentObjectGroupPython] G4_In  # scripted group (container) (typed FeaturePython)
  Dunit = g/cm3
  Dvalue = 7.31
  Group = -> [In_element001]
  conduct = 2
  density = 1
  expand = 3
  formula = In
  name = G4_In
  specific = 4
FEATURE [App::DocumentObjectGroupPython] Sn_element001  label="Sn_element : 1"  # scripted group (container) (typed FeaturePython)
  n = 1
  ref = Sn_element
FEATURE [App::DocumentObjectGroupPython] G4_Sn  # scripted group (container) (typed FeaturePython)
  Dunit = g/cm3
  Dvalue = 7.31
  Group = -> [Sn_element001]
  conduct = 2
  density = 1
  expand = 3
  formula = Sn
  name = G4_Sn
  specific = 4
FEATURE [App::DocumentObjectGroupPython] Sb_element001  label="Sb_element : 1"  # scripted group (container) (typed FeaturePython)
  n = 1
  ref = Sb_element
FEATURE [App::DocumentObjectGroupPython] G4_Sb  # scripted group (container) (typed FeaturePython)
  Dunit = g/cm3
  Dvalue = 6.691
  Group = -> [Sb_element001]
  conduct = 2
  density = 1
  expand = 3
  formula = Sb
  name = G4_Sb
  specific = 4
FEATURE [App::DocumentObjectGroupPython] Te_element002  label="Te_element : 002"  # scripted group (container) (typed FeaturePython)
  n = 1
  ref = Te_element
FEATURE [App::DocumentObjectGroupPython] G4_Te  # scripted group (container) (typed FeaturePython)
  Dunit = g/cm3
  Dvalue = 6.24
  Group = -> [Te_element002]
  conduct = 2
  density = 1
  expand = 3
  formula = Te
  name = G4_Te
  specific = 4
FEATURE [App::DocumentObjectGroupPython] I_element010  label="I_element : 006"  # scripted group (container) (typed FeaturePython)
  n = 1
  ref = I_element
FEATURE [App::DocumentObjectGroupPython] G4_I  # scripted group (container) (typed FeaturePython)
  Dunit = g/cm3
  Dvalue = 4.93
  Group = -> [I_element010]
  conduct = 2
  density = 1
  expand = 3
  formula = I
  name = G4_I
  specific = 4
FEATURE [App::DocumentObjectGroupPython] Xe_element001  label="Xe_element : 1"  # scripted group (container) (typed FeaturePython)
  n = 1
  ref = Xe_element
FEATURE [App::DocumentObjectGroupPython] G4_Xe  # scripted group (container) (typed FeaturePython)
  Dunit = g/cm3
  Dvalue = 0.00548536
  Group = -> [Xe_element001]
  conduct = 2
  density = 1
  expand = 3
  formula = Xe
  name = G4_Xe
  specific = 4
FEATURE [App::DocumentObjectGroupPython] Cs_element003  label="Cs_element : 003"  # scripted group (container) (typed FeaturePython)
  n = 1
  ref = Cs_element
FEATURE [App::DocumentObjectGroupPython] G4_Cs  # scripted group (container) (typed FeaturePython)
  Dunit = g/cm3
  Dvalue = 1.873
  Group = -> [Cs_element003]
  conduct = 2
  density = 1
  expand = 3
  formula = Cs
  name = G4_Cs
  specific = 4
FEATURE [App::DocumentObjectGroupPython] Ba_element003  label="Ba_element : 003"  # scripted group (container) (typed FeaturePython)
  n = 1
  ref = Ba_element
FEATURE [App::DocumentObjectGroupPython] G4_Ba  # scripted group (container) (typed FeaturePython)
  Dunit = g/cm3
  Dvalue = 3.5
  Group = -> [Ba_element003]
  conduct = 2
  density = 1
  expand = 3
  formula = Ba
  name = G4_Ba
  specific = 4
FEATURE [App::DocumentObjectGroupPython] La_element003  label="La_element : 003"  # scripted group (container) (typed FeaturePython)
  n = 1
  ref = La_element
FEATURE [App::DocumentObjectGroupPython] G4_La  # scripted group (container) (typed FeaturePython)
  Dunit = g/cm3
  Dvalue = 6.154
  Group = -> [La_element003]
  conduct = 2
  density = 1
  expand = 3
  formula = La
  name = G4_La
  specific = 4
FEATURE [App::DocumentObjectGroupPython] Ce_element002  label="Ce_element : 1"  # scripted group (container) (typed FeaturePython)
  n = 1
  ref = Ce_element
FEATURE [App::DocumentObjectGroupPython] G4_Ce  # scripted group (container) (typed FeaturePython)
  Dunit = g/cm3
  Dvalue = 6.657
  Group = -> [Ce_element002]
  conduct = 2
  density = 1
  expand = 3
  formula = Ce
  name = G4_Ce
  specific = 4
FEATURE [App::DocumentObjectGroupPython] Pr_element001  label="Pr_element : 1"  # scripted group (container) (typed FeaturePython)
  n = 1
  ref = Pr_element
FEATURE [App::DocumentObjectGroupPython] G4_Pr  # scripted group (container) (typed FeaturePython)
  Dunit = g/cm3
  Dvalue = 6.71
  Group = -> [Pr_element001]
  conduct = 2
  density = 1
  expand = 3
  formula = Pr
  name = G4_Pr
  specific = 4
FEATURE [App::DocumentObjectGroupPython] Nd_element001  label="Nd_element : 1"  # scripted group (container) (typed FeaturePython)
  n = 1
  ref = Nd_element
FEATURE [App::DocumentObjectGroupPython] G4_Nd  # scripted group (container) (typed FeaturePython)
  Dunit = g/cm3
  Dvalue = 6.9
  Group = -> [Nd_element001]
  conduct = 2
  density = 1
  expand = 3
  formula = Nd
  name = G4_Nd
  specific = 4
FEATURE [App::DocumentObjectGroupPython] Pm_element001  label="Pm_element : 1"  # scripted group (container) (typed FeaturePython)
  n = 1
  ref = Pm_element
FEATURE [App::DocumentObjectGroupPython] G4_Pm  # scripted group (container) (typed FeaturePython)
  Dunit = g/cm3
  Dvalue = 7.22
  Group = -> [Pm_element001]
  conduct = 2
  density = 1
  expand = 3
  formula = Pm
  name = G4_Pm
  specific = 4
FEATURE [App::DocumentObjectGroupPython] Sm_element001  label="Sm_element : 1"  # scripted group (container) (typed FeaturePython)
  n = 1
  ref = Sm_element
FEATURE [App::DocumentObjectGroupPython] G4_Sm  # scripted group (container) (typed FeaturePython)
  Dunit = g/cm3
  Dvalue = 7.46
  Group = -> [Sm_element001]
  conduct = 2
  density = 1
  expand = 3
  formula = Sm
  name = G4_Sm
  specific = 4
FEATURE [App::DocumentObjectGroupPython] Eu_element001  label="Eu_element : 1"  # scripted group (container) (typed FeaturePython)
  n = 1
  ref = Eu_element
FEATURE [App::DocumentObjectGroupPython] G4_Eu  # scripted group (container) (typed FeaturePython)
  Dunit = g/cm3
  Dvalue = 5.243
  Group = -> [Eu_element001]
  conduct = 2
  density = 1
  expand = 3
  formula = Eu
  name = G4_Eu
  specific = 4
FEATURE [App::DocumentObjectGroupPython] Gd_element002  label="Gd_element : 1"  # scripted group (container) (typed FeaturePython)
  n = 1
  ref = Gd_element
FEATURE [App::DocumentObjectGroupPython] G4_Gd  # scripted group (container) (typed FeaturePython)
  Dunit = g/cm3
  Dvalue = 7.9004
  Group = -> [Gd_element002]
  conduct = 2
  density = 1
  expand = 3
  formula = Gd
  name = G4_Gd
  specific = 4
FEATURE [App::DocumentObjectGroupPython] Tb_element001  label="Tb_element : 1"  # scripted group (container) (typed FeaturePython)
  n = 1
  ref = Tb_element
FEATURE [App::DocumentObjectGroupPython] G4_Tb  # scripted group (container) (typed FeaturePython)
  Dunit = g/cm3
  Dvalue = 8.229
  Group = -> [Tb_element001]
  conduct = 2
  density = 1
  expand = 3
  formula = Tb
  name = G4_Tb
  specific = 4
FEATURE [App::DocumentObjectGroupPython] Dy_element001  label="Dy_element : 1"  # scripted group (container) (typed FeaturePython)
  n = 1
  ref = Dy_element
FEATURE [App::DocumentObjectGroupPython] G4_Dy  # scripted group (container) (typed FeaturePython)
  Dunit = g/cm3
  Dvalue = 8.55
  Group = -> [Dy_element001]
  conduct = 2
  density = 1
  expand = 3
  formula = Dy
  name = G4_Dy
  specific = 4
FEATURE [App::DocumentObjectGroupPython] Ho_element001  label="Ho_element : 1"  # scripted group (container) (typed FeaturePython)
  n = 1
  ref = Ho_element
FEATURE [App::DocumentObjectGroupPython] G4_Ho  # scripted group (container) (typed FeaturePython)
  Dunit = g/cm3
  Dvalue = 8.795
  Group = -> [Ho_element001]
  conduct = 2
  density = 1
  expand = 3
  formula = Ho
  name = G4_Ho
  specific = 4
FEATURE [App::DocumentObjectGroupPython] Er_element001  label="Er_element : 1"  # scripted group (container) (typed FeaturePython)
  n = 1
  ref = Er_element
FEATURE [App::DocumentObjectGroupPython] G4_Er  # scripted group (container) (typed FeaturePython)
  Dunit = g/cm3
  Dvalue = 9.066
  Group = -> [Er_element001]
  conduct = 2
  density = 1
  expand = 3
  formula = Er
  name = G4_Er
  specific = 4
FEATURE [App::DocumentObjectGroupPython] Tm_element001  label="Tm_element : 1"  # scripted group (container) (typed FeaturePython)
  n = 1
  ref = Tm_element
FEATURE [App::DocumentObjectGroupPython] G4_Tm  # scripted group (container) (typed FeaturePython)
  Dunit = g/cm3
  Dvalue = 9.321
  Group = -> [Tm_element001]
  conduct = 2
  density = 1
  expand = 3
  formula = Tm
  name = G4_Tm
  specific = 4
FEATURE [App::DocumentObjectGroupPython] Yb_element001  label="Yb_element : 1"  # scripted group (container) (typed FeaturePython)
  n = 1
  ref = Yb_element
FEATURE [App::DocumentObjectGroupPython] G4_Yb  # scripted group (container) (typed FeaturePython)
  Dunit = g/cm3
  Dvalue = 6.73
  Group = -> [Yb_element001]
  conduct = 2
  density = 1
  expand = 3
  formula = Yb
  name = G4_Yb
  specific = 4
FEATURE [App::DocumentObjectGroupPython] Lu_element001  label="Lu_element : 1"  # scripted group (container) (typed FeaturePython)
  n = 1
  ref = Lu_element
FEATURE [App::DocumentObjectGroupPython] G4_Lu  # scripted group (container) (typed FeaturePython)
  Dunit = g/cm3
  Dvalue = 9.84
  Group = -> [Lu_element001]
  conduct = 2
  density = 1
  expand = 3
  formula = Lu
  name = G4_Lu
  specific = 4
FEATURE [App::DocumentObjectGroupPython] Hf_element001  label="Hf_element : 1"  # scripted group (container) (typed FeaturePython)
  n = 1
  ref = Hf_element
FEATURE [App::DocumentObjectGroupPython] G4_Hf  # scripted group (container) (typed FeaturePython)
  Dunit = g/cm3
  Dvalue = 13.31
  Group = -> [Hf_element001]
  conduct = 2
  density = 1
  expand = 3
  formula = Hf
  name = G4_Hf
  specific = 4
FEATURE [App::DocumentObjectGroupPython] Ta_element001  label="Ta_element : 1"  # scripted group (container) (typed FeaturePython)
  n = 1
  ref = Ta_element
FEATURE [App::DocumentObjectGroupPython] G4_Ta  # scripted group (container) (typed FeaturePython)
  Dunit = g/cm3
  Dvalue = 16.654
  Group = -> [Ta_element001]
  conduct = 2
  density = 1
  expand = 3
  formula = Ta
  name = G4_Ta
  specific = 4
FEATURE [App::DocumentObjectGroupPython] W_element004  label="W_element : 004"  # scripted group (container) (typed FeaturePython)
  n = 1
  ref = W_element
FEATURE [App::DocumentObjectGroupPython] G4_W  # scripted group (container) (typed FeaturePython)
  Dunit = g/cm3
  Dvalue = 19.3
  Group = -> [W_element004]
  conduct = 2
  density = 1
  expand = 3
  formula = W
  name = G4_W
  specific = 4
FEATURE [App::DocumentObjectGroupPython] Re_element001  label="Re_element : 1"  # scripted group (container) (typed FeaturePython)
  n = 1
  ref = Re_element
FEATURE [App::DocumentObjectGroupPython] G4_Re  # scripted group (container) (typed FeaturePython)
  Dunit = g/cm3
  Dvalue = 21.02
  Group = -> [Re_element001]
  conduct = 2
  density = 1
  expand = 3
  formula = Re
  name = G4_Re
  specific = 4
FEATURE [App::DocumentObjectGroupPython] Os_element001  label="Os_element : 1"  # scripted group (container) (typed FeaturePython)
  n = 1
  ref = Os_element
FEATURE [App::DocumentObjectGroupPython] G4_Os  # scripted group (container) (typed FeaturePython)
  Dunit = g/cm3
  Dvalue = 22.57
  Group = -> [Os_element001]
  conduct = 2
  density = 1
  expand = 3
  formula = Os
  name = G4_Os
  specific = 4
FEATURE [App::DocumentObjectGroupPython] Ir_element001  label="Ir_element : 1"  # scripted group (container) (typed FeaturePython)
  n = 1
  ref = Ir_element
FEATURE [App::DocumentObjectGroupPython] G4_Ir  # scripted group (container) (typed FeaturePython)
  Dunit = g/cm3
  Dvalue = 22.42
  Group = -> [Ir_element001]
  conduct = 2
  density = 1
  expand = 3
  formula = Ir
  name = G4_Ir
  specific = 4
FEATURE [App::DocumentObjectGroupPython] Pt_element001  label="Pt_element : 1"  # scripted group (container) (typed FeaturePython)
  n = 1
  ref = Pt_element
FEATURE [App::DocumentObjectGroupPython] G4_Pt  # scripted group (container) (typed FeaturePython)
  Dunit = g/cm3
  Dvalue = 21.45
  Group = -> [Pt_element001]
  conduct = 2
  density = 1
  expand = 3
  formula = Pt
  name = G4_Pt
  specific = 4
FEATURE [App::DocumentObjectGroupPython] Au_element001  label="Au_element : 1"  # scripted group (container) (typed FeaturePython)
  n = 1
  ref = Au_element
FEATURE [App::DocumentObjectGroupPython] G4_Au  # scripted group (container) (typed FeaturePython)
  Dunit = g/cm3
  Dvalue = 19.32
  Group = -> [Au_element001]
  conduct = 2
  density = 1
  expand = 3
  formula = Au
  name = G4_Au
  specific = 4
FEATURE [App::DocumentObjectGroupPython] Hg_element002  label="Hg_element : 002"  # scripted group (container) (typed FeaturePython)
  n = 1
  ref = Hg_element
FEATURE [App::DocumentObjectGroupPython] G4_Hg  # scripted group (container) (typed FeaturePython)
  Dunit = g/cm3
  Dvalue = 13.546
  Group = -> [Hg_element002]
  conduct = 2
  density = 1
  expand = 3
  formula = Hg
  name = G4_Hg
  specific = 4
FEATURE [App::DocumentObjectGroupPython] Tl_element002  label="Tl_element : 002"  # scripted group (container) (typed FeaturePython)
  n = 1
  ref = Tl_element
FEATURE [App::DocumentObjectGroupPython] G4_Tl  # scripted group (container) (typed FeaturePython)
  Dunit = g/cm3
  Dvalue = 11.72
  Group = -> [Tl_element002]
  conduct = 2
  density = 1
  expand = 3
  formula = Tl
  name = G4_Tl
  specific = 4
FEATURE [App::DocumentObjectGroupPython] Pb_element003  label="Pb_element : 1"  # scripted group (container) (typed FeaturePython)
  n = 1
  ref = Pb_element
FEATURE [App::DocumentObjectGroupPython] G4_Pb  # scripted group (container) (typed FeaturePython)
  Dunit = g/cm3
  Dvalue = 11.35
  Group = -> [Pb_element003]
  conduct = 2
  density = 1
  expand = 3
  formula = Pb
  name = G4_Pb
  specific = 4
FEATURE [App::DocumentObjectGroupPython] Bi_element002  label="Bi_element : 1"  # scripted group (container) (typed FeaturePython)
  n = 1
  ref = Bi_element
FEATURE [App::DocumentObjectGroupPython] G4_Bi  # scripted group (container) (typed FeaturePython)
  Dunit = g/cm3
  Dvalue = 9.747
  Group = -> [Bi_element002]
  conduct = 2
  density = 1
  expand = 3
  formula = Bi
  name = G4_Bi
  specific = 4
FEATURE [App::DocumentObjectGroupPython] Po_element001  label="Po_element : 1"  # scripted group (container) (typed FeaturePython)
  n = 1
  ref = Po_element
FEATURE [App::DocumentObjectGroupPython] G4_Po  # scripted group (container) (typed FeaturePython)
  Dunit = g/cm3
  Dvalue = 9.32
  Group = -> [Po_element001]
  conduct = 2
  density = 1
  expand = 3
  formula = Po
  name = G4_Po
  specific = 4
FEATURE [App::DocumentObjectGroupPython] At_element001  label="At_element : 1"  # scripted group (container) (typed FeaturePython)
  n = 1
  ref = At_element
FEATURE [App::DocumentObjectGroupPython] G4_At  # scripted group (container) (typed FeaturePython)
  Dunit = g/cm3
  Dvalue = 9.32
  Group = -> [At_element001]
  conduct = 2
  density = 1
  expand = 3
  formula = At
  name = G4_At
  specific = 4
FEATURE [App::DocumentObjectGroupPython] Rn_element001  label="Rn_element : 1"  # scripted group (container) (typed FeaturePython)
  n = 1
  ref = Rn_element
FEATURE [App::DocumentObjectGroupPython] G4_Rn  # scripted group (container) (typed FeaturePython)
  Dunit = g/cm3
  Dvalue = 0.00900662
  Group = -> [Rn_element001]
  conduct = 2
  density = 1
  expand = 3
  formula = Rn
  name = G4_Rn
  specific = 4
FEATURE [App::DocumentObjectGroupPython] Fr_element001  label="Fr_element : 1"  # scripted group (container) (typed FeaturePython)
  n = 1
  ref = Fr_element
FEATURE [App::DocumentObjectGroupPython] G4_Fr  # scripted group (container) (typed FeaturePython)
  Dunit = g/cm3
  Dvalue = 1
  Group = -> [Fr_element001]
  conduct = 2
  density = 1
  expand = 3
  formula = Fr
  name = G4_Fr
  specific = 4
FEATURE [App::DocumentObjectGroupPython] Ra_element001  label="Ra_element : 1"  # scripted group (container) (typed FeaturePython)
  n = 1
  ref = Ra_element
FEATURE [App::DocumentObjectGroupPython] G4_Ra  # scripted group (container) (typed FeaturePython)
  Dunit = g/cm3
  Dvalue = 5
  Group = -> [Ra_element001]
  conduct = 2
  density = 1
  expand = 3
  formula = Ra
  name = G4_Ra
  specific = 4
FEATURE [App::DocumentObjectGroupPython] Ac_element001  label="Ac_element : 1"  # scripted group (container) (typed FeaturePython)
  n = 1
  ref = Ac_element
FEATURE [App::DocumentObjectGroupPython] G4_Ac  # scripted group (container) (typed FeaturePython)
  Dunit = g/cm3
  Dvalue = 10.07
  Group = -> [Ac_element001]
  conduct = 2
  density = 1
  expand = 3
  formula = Ac
  name = G4_Ac
  specific = 4
FEATURE [App::DocumentObjectGroupPython] Th_element001  label="Th_element : 1"  # scripted group (container) (typed FeaturePython)
  n = 1
  ref = Th_element
FEATURE [App::DocumentObjectGroupPython] G4_Th  # scripted group (container) (typed FeaturePython)
  Dunit = g/cm3
  Dvalue = 11.72
  Group = -> [Th_element001]
  conduct = 2
  density = 1
  expand = 3
  formula = Th
  name = G4_Th
  specific = 4
FEATURE [App::DocumentObjectGroupPython] Pa_element001  label="Pa_element : 1"  # scripted group (container) (typed FeaturePython)
  n = 1
  ref = Pa_element
FEATURE [App::DocumentObjectGroupPython] G4_Pa  # scripted group (container) (typed FeaturePython)
  Dunit = g/cm3
  Dvalue = 15.37
  Group = -> [Pa_element001]
  conduct = 2
  density = 1
  expand = 3
  formula = Pa
  name = G4_Pa
  specific = 4
FEATURE [App::DocumentObjectGroupPython] U_element004  label="U_element : 004"  # scripted group (container) (typed FeaturePython)
  n = 1
  ref = U_element
FEATURE [App::DocumentObjectGroupPython] G4_U  # scripted group (container) (typed FeaturePython)
  Dunit = g/cm3
  Dvalue = 18.95
  Group = -> [U_element004]
  conduct = 2
  density = 1
  expand = 3
  formula = U
  name = G4_U
  specific = 4
FEATURE [App::DocumentObjectGroupPython] Np_element001  label="Np_element : 1"  # scripted group (container) (typed FeaturePython)
  n = 1
  ref = Np_element
FEATURE [App::DocumentObjectGroupPython] G4_Np  # scripted group (container) (typed FeaturePython)
  Dunit = g/cm3
  Dvalue = 20.25
  Group = -> [Np_element001]
  conduct = 2
  density = 1
  expand = 3
  formula = Np
  name = G4_Np
  specific = 4
FEATURE [App::DocumentObjectGroupPython] Pu_element002  label="Pu_element : 002"  # scripted group (container) (typed FeaturePython)
  n = 1
  ref = Pu_element
FEATURE [App::DocumentObjectGroupPython] G4_Pu  # scripted group (container) (typed FeaturePython)
  Dunit = g/cm3
  Dvalue = 19.84
  Group = -> [Pu_element002]
  conduct = 2
  density = 1
  expand = 3
  formula = Pu
  name = G4_Pu
  specific = 4
FEATURE [App::DocumentObjectGroupPython] Am_element001  label="Am_element : 1"  # scripted group (container) (typed FeaturePython)
  n = 1
  ref = Am_element
FEATURE [App::DocumentObjectGroupPython] G4_Am  # scripted group (container) (typed FeaturePython)
  Dunit = g/cm3
  Dvalue = 13.67
  Group = -> [Am_element001]
  conduct = 2
  density = 1
  expand = 3
  formula = Am
  name = G4_Am
  specific = 4
FEATURE [App::DocumentObjectGroupPython] Cm_element001  label="Cm_element : 1"  # scripted group (container) (typed FeaturePython)
  n = 1
  ref = Cm_element
FEATURE [App::DocumentObjectGroupPython] G4_Cm  # scripted group (container) (typed FeaturePython)
  Dunit = g/cm3
  Dvalue = 13.51
  Group = -> [Cm_element001]
  conduct = 2
  density = 1
  expand = 3
  formula = Cm
  name = G4_Cm
  specific = 4
FEATURE [App::DocumentObjectGroupPython] Bk_element001  label="Bk_element : 1"  # scripted group (container) (typed FeaturePython)
  n = 1
  ref = Bk_element
FEATURE [App::DocumentObjectGroupPython] G4_Bk  # scripted group (container) (typed FeaturePython)
  Dunit = g/cm3
  Dvalue = 14
  Group = -> [Bk_element001]
  conduct = 2
  density = 1
  expand = 3
  formula = Bk
  name = G4_Bk
  specific = 4
FEATURE [App::DocumentObjectGroupPython] Cf_element001  label="Cf_element : 1"  # scripted group (container) (typed FeaturePython)
  n = 1
  ref = Cf_element
FEATURE [App::DocumentObjectGroupPython] G4_Cf  # scripted group (container) (typed FeaturePython)
  Dunit = g/cm3
  Dvalue = 10
  Group = -> [Cf_element001]
  conduct = 2
  density = 1
  expand = 3
  formula = Cf
  name = G4_Cf
  specific = 4
FEATURE [App::DocumentObjectGroupPython] Element  # scripted group (container) (typed FeaturePython)
  Group = -> [G4_H,G4_He,G4_Li,G4_Be,G4_B,G4_C,G4_N,G4_O,G4_F,G4_Ne,G4_Na,G4_Mg,G4_Al,G4_Si,G4_P,G4_S,G4_Cl,G4_Ar,G4_K,G4_Ca,G4_Sc,G4_Ti,G4_V,G4_Cr,G4_Mn,G4_Fe,G4_Co,G4_Ni,G4_Cu,G4_Zn,G4_Ga,G4_Ge,G4_As,G4_Se,G4_Br,G4_Kr,G4_Rb,G4_Sr,G4_Y,G4_Zr,G4_Nb,G4_Mo,G4_Tc,G4_Ru,G4_Rh,G4_Pd,G4_Ag,G4_Cd,G4_In,G4_Sn,G4_Sb,G4_Te,G4_I,G4_Xe,G4_Cs,G4_Ba,G4_La,G4_Ce,G4_Pr,G4_Nd,G4_Pm,G4_Sm,G4_Eu,G4_Gd,G4_Tb,G4_Dy,G4_Ho,G4_Er,+30 more]
FEATURE [App::DocumentObjectGroupPython] H_element114  label="H_element : 063"  # scripted group (container) (typed FeaturePython)
  n = 2
  ref = H_element
FEATURE [App::DocumentObjectGroupPython] G4_lH2  # scripted group (container) (typed FeaturePython)
  Dunit = g/cm3
  Dvalue = 0.0708
  Group = -> [H_element114]
  conduct = 2
  density = 1
  expand = 3
  formula = G4_lH2
  name = G4_lH2
  specific = 4
FEATURE [App::DocumentObjectGroupPython] N_element049  label="N_element : 022"  # scripted group (container) (typed FeaturePython)
  n = 2
  ref = N_element
FEATURE [App::DocumentObjectGroupPython] G4_lN2  # scripted group (container) (typed FeaturePython)
  Dunit = g/cm3
  Dvalue = 0.807
  Group = -> [N_element049]
  conduct = 2
  density = 1
  expand = 3
  formula = G4_lN2
  name = G4_lN2
  specific = 4
FEATURE [App::DocumentObjectGroupPython] O_element106  label="O_element : 060"  # scripted group (container) (typed FeaturePython)
  n = 2
  ref = O_element
FEATURE [App::DocumentObjectGroupPython] G4_lO2  # scripted group (container) (typed FeaturePython)
  Dunit = g/cm3
  Dvalue = 1.141
  Group = -> [O_element106]
  conduct = 2
  density = 1
  expand = 3
  formula = G4_lO2
  name = G4_lO2
  specific = 4
FEATURE [App::DocumentObjectGroupPython] Ar  label="Ar : 1"  # scripted group (container) (typed FeaturePython)
  n = 1
  ref = Ar
FEATURE [App::DocumentObjectGroupPython] G4_lAr  # scripted group (container) (typed FeaturePython)
  Dunit = g/cm3
  Dvalue = 1.396
  Group = -> [Ar]
  conduct = 2
  density = 1
  expand = 3
  formula = G4_lAr
  name = G4_lAr
  specific = 4
FEATURE [App::DocumentObjectGroupPython] Br  label="Br : 1"  # scripted group (container) (typed FeaturePython)
  n = 1
  ref = Br
FEATURE [App::DocumentObjectGroupPython] G4_lBr  # scripted group (container) (typed FeaturePython)
  Dunit = g/cm3
  Dvalue = 3.1028
  Group = -> [Br]
  conduct = 2
  density = 1
  expand = 3
  formula = G4_lBr
  name = G4_lBr
  specific = 4
FEATURE [App::DocumentObjectGroupPython] Kr  label="Kr : 1"  # scripted group (container) (typed FeaturePython)
  n = 1
  ref = Kr
FEATURE [App::DocumentObjectGroupPython] G4_lKr  # scripted group (container) (typed FeaturePython)
  Dunit = g/cm3
  Dvalue = 2.418
  Group = -> [Kr]
  conduct = 2
  density = 1
  expand = 3
  formula = G4_lKr
  name = G4_lKr
  specific = 4
FEATURE [App::DocumentObjectGroupPython] Xe  label="Xe : 1"  # scripted group (container) (typed FeaturePython)
  n = 1
  ref = Xe
FEATURE [App::DocumentObjectGroupPython] G4_lXe  # scripted group (container) (typed FeaturePython)
  Dunit = g/cm3
  Dvalue = 2.953
  Group = -> [Xe]
  conduct = 2
  density = 1
  expand = 3
  formula = G4_lXe
  name = G4_lXe
  specific = 4
FEATURE [App::DocumentObjectGroupPython] O_element107  label="O_element : 061"  # scripted group (container) (typed FeaturePython)
  n = 4
  ref = O_element
FEATURE [App::DocumentObjectGroupPython] Pb_element004  label="Pb_element : 002"  # scripted group (container) (typed FeaturePython)
  n = 1
  ref = Pb_element
FEATURE [App::DocumentObjectGroupPython] W_element005  label="W_element : 005"  # scripted group (container) (typed FeaturePython)
  n = 1
  ref = W_element
FEATURE [App::DocumentObjectGroupPython] G4_PbWO4  # scripted group (container) (typed FeaturePython)
  Dunit = g/cm3
  Dvalue = 8.28
  Group = -> [O_element107,Pb_element004,W_element005]
  conduct = 2
  density = 1
  expand = 3
  formula = G4_PbWO4
  name = G4_PbWO4
  specific = 4
FEATURE [App::DocumentObjectGroupPython] alactic  label="alactic : 1"  # scripted group (container) (typed FeaturePython)
  n = 1
  ref = alactic
FEATURE [App::DocumentObjectGroupPython] G4_Galactic  # scripted group (container) (typed FeaturePython)
  Dunit = g/cm3
  Dvalue = 0
  Group = -> [alactic]
  conduct = 2
  density = 1
  expand = 3
  formula = G4_Galactic
  name = G4_Galactic
  specific = 4
FEATURE [App::DocumentObjectGroupPython] RAPHITE_POROUS  label="RAPHITE_POROUS : 1"  # scripted group (container) (typed FeaturePython)
  n = 1
  ref = RAPHITE_POROUS
FEATURE [App::DocumentObjectGroupPython] G4_GRAPHITE_POROUS  # scripted group (container) (typed FeaturePython)
  Dunit = g/cm3
  Dvalue = 1.7
  Group = -> [RAPHITE_POROUS]
  conduct = 2
  density = 1
  expand = 3
  formula = G4_GRAPHITE_POROUS
  name = G4_GRAPHITE_POROUS
  specific = 4
FEATURE [App::DocumentObjectGroupPython] H_element115  label="H_element : 0.150"  # scripted group (container) (typed FeaturePython)
  n = 0.080538
FEATURE [App::DocumentObjectGroupPython] C_element125  label="C_element : 0.600"  # scripted group (container) (typed FeaturePython)
  n = 0.599848
FEATURE [App::DocumentObjectGroupPython] O_element108  label="O_element : 0.320"  # scripted group (container) (typed FeaturePython)
  n = 0.319614
FEATURE [App::DocumentObjectGroupPython] G4_LUCITE  # scripted group (container) (typed FeaturePython)
  Dunit = g/cm3
  Dvalue = 1.19
  Group = -> [H_element115,C_element125,O_element108]
  conduct = 2
  density = 1
  expand = 3
  formula = G4_LUCITE
  name = G4_LUCITE
  specific = 4
FEATURE [App::DocumentObjectGroupPython] Cu_element002  label="Cu_element : 62"  # scripted group (container) (typed FeaturePython)
  n = 62
  ref = Cu_element
FEATURE [App::DocumentObjectGroupPython] Zn_element002  label="Zn_element : 35"  # scripted group (container) (typed FeaturePython)
  n = 35
  ref = Zn_element
FEATURE [App::DocumentObjectGroupPython] Pb_element005  label="Pb_element : 3"  # scripted group (container) (typed FeaturePython)
  n = 3
  ref = Pb_element
FEATURE [App::DocumentObjectGroupPython] G4_BRASS  # scripted group (container) (typed FeaturePython)
  Dunit = g/cm3
  Dvalue = 8.52
  Group = -> [Cu_element002,Zn_element002,Pb_element005]
  conduct = 2
  density = 1
  expand = 3
  formula = G4_BRASS
  name = G4_BRASS
  specific = 4
FEATURE [App::DocumentObjectGroupPython] Cu_element003  label="Cu_element : 89"  # scripted group (container) (typed FeaturePython)
  n = 89
  ref = Cu_element
FEATURE [App::DocumentObjectGroupPython] Zn_element003  label="Zn_element : 9"  # scripted group (container) (typed FeaturePython)
  n = 9
  ref = Zn_element
FEATURE [App::DocumentObjectGroupPython] Pb_element006  label="Pb_element : 2"  # scripted group (container) (typed FeaturePython)
  n = 2
  ref = Pb_element
FEATURE [App::DocumentObjectGroupPython] G4_BRONZE  # scripted group (container) (typed FeaturePython)
  Dunit = g/cm3
  Dvalue = 8.82
  Group = -> [Cu_element003,Zn_element003,Pb_element006]
  conduct = 2
  density = 1
  expand = 3
  formula = G4_BRONZE
  name = G4_BRONZE
  specific = 4
FEATURE [App::DocumentObjectGroupPython] Fe_element008  label="Fe_element : 74"  # scripted group (container) (typed FeaturePython)
  n = 74
  ref = Fe_element
FEATURE [App::DocumentObjectGroupPython] Cr_element002  label="Cr_element : 18"  # scripted group (container) (typed FeaturePython)
  n = 18
  ref = Cr_element
FEATURE [App::DocumentObjectGroupPython] Ni_element002  label="Ni_element : 8"  # scripted group (container) (typed FeaturePython)
  n = 8
  ref = Ni_element
FEATURE [App::DocumentObjectGroupPython] G4_STAINLESS_STEEL  label="G4_STAINLESS-STEEL"  # scripted group (container) (typed FeaturePython)
  Dunit = g/cm3
  Dvalue = 8
  Group = -> [Fe_element008,Cr_element002,Ni_element002]
  conduct = 2
  density = 1
  expand = 3
  formula = G4_STAINLESS-STEEL
  name = G4_STAINLESS-STEEL
  specific = 4
FEATURE [App::DocumentObjectGroupPython] H_element116  label="H_element : 064"  # scripted group (container) (typed FeaturePython)
  n = 18
  ref = H_element
FEATURE [App::DocumentObjectGroupPython] C_element126  label="C_element : 071"  # scripted group (container) (typed FeaturePython)
  n = 12
  ref = C_element
FEATURE [App::DocumentObjectGroupPython] O_element109  label="O_element : 062"  # scripted group (container) (typed FeaturePython)
  n = 7
  ref = O_element
FEATURE [App::DocumentObjectGroupPython] G4_CR39  # scripted group (container) (typed FeaturePython)
  Dunit = g/cm3
  Dvalue = 1.32
  Group = -> [H_element116,C_element126,O_element109]
  conduct = 2
  density = 1
  expand = 3
  formula = G4_CR39
  name = G4_CR39
  specific = 4
FEATURE [App::DocumentObjectGroupPython] H_element117  label="H_element : 38"  # scripted group (container) (typed FeaturePython)
  n = 38
  ref = H_element
FEATURE [App::DocumentObjectGroupPython] C_element127  label="C_element : 072"  # scripted group (container) (typed FeaturePython)
  n = 18
  ref = C_element
FEATURE [App::DocumentObjectGroupPython] O_element110  label="O_element : 063"  # scripted group (container) (typed FeaturePython)
  n = 1
  ref = O_element
FEATURE [App::DocumentObjectGroupPython] G4_OCTADECANOL  # scripted group (container) (typed FeaturePython)
  Dunit = g/cm3
  Dvalue = 0.812
  Group = -> [H_element117,C_element127,O_element110]
  conduct = 2
  density = 1
  expand = 3
  formula = G4_OCTADECANOL
  name = G4_OCTADECANOL
  specific = 4
FEATURE [App::DocumentObjectGroupPython] HEP  # scripted group (container) (typed FeaturePython)
  Group = -> [G4_lH2,G4_lN2,G4_lO2,G4_lAr,G4_lBr,G4_lKr,G4_lXe,G4_PbWO4,G4_Galactic,G4_GRAPHITE_POROUS,G4_LUCITE,G4_BRASS,G4_BRONZE,G4_STAINLESS_STEEL,G4_CR39,G4_OCTADECANOL]
FEATURE [App::DocumentObjectGroupPython] C_element128  label="C_element : 073"  # scripted group (container) (typed FeaturePython)
  n = 14
  ref = C_element
FEATURE [App::DocumentObjectGroupPython] H_element118  label="H_element : 065"  # scripted group (container) (typed FeaturePython)
  n = 10
  ref = H_element
FEATURE [App::DocumentObjectGroupPython] O_element111  label="O_element : 064"  # scripted group (container) (typed FeaturePython)
  n = 2
  ref = O_element
FEATURE [App::DocumentObjectGroupPython] N_element050  label="N_element : 023"  # scripted group (container) (typed FeaturePython)
  n = 2
  ref = N_element
FEATURE [App::DocumentObjectGroupPython] G4_KEVLAR  # scripted group (container) (typed FeaturePython)
  Dunit = g/cm3
  Dvalue = 1.44
  Group = -> [C_element128,H_element118,O_element111,N_element050]
  conduct = 2
  density = 1
  expand = 3
  formula = G4_KEVLAR
  name = G4_KEVLAR
  specific = 4
FEATURE [App::DocumentObjectGroupPython] C_element129  label="C_element : 074"  # scripted group (container) (typed FeaturePython)
  n = 10
  ref = C_element
FEATURE [App::DocumentObjectGroupPython] H_element119  label="H_element : 066"  # scripted group (container) (typed FeaturePython)
  n = 8
  ref = H_element
FEATURE [App::DocumentObjectGroupPython] O_element112  label="O_element : 065"  # scripted group (container) (typed FeaturePython)
  n = 4
  ref = O_element
FEATURE [App::DocumentObjectGroupPython] G4_DACRON  # scripted group (container) (typed FeaturePython)
  Dunit = g/cm3
  Dvalue = 1.4
  Group = -> [C_element129,H_element119,O_element112]
  conduct = 2
  density = 1
  expand = 3
  formula = G4_DACRON
  name = G4_DACRON
  specific = 4
FEATURE [App::DocumentObjectGroupPython] C_element130  label="C_element : 075"  # scripted group (container) (typed FeaturePython)
  n = 4
  ref = C_element
FEATURE [App::DocumentObjectGroupPython] H_element120  label="H_element : 067"  # scripted group (container) (typed FeaturePython)
  n = 5
  ref = H_element
FEATURE [App::DocumentObjectGroupPython] Cl_element030  label="Cl_element : 016"  # scripted group (container) (typed FeaturePython)
  n = 1
  ref = Cl_element
FEATURE [App::DocumentObjectGroupPython] G4_NEOPRENE  # scripted group (container) (typed FeaturePython)
  Dunit = g/cm3
  Dvalue = 1.23
  Group = -> [C_element130,H_element120,Cl_element030]
  conduct = 2
  density = 1
  expand = 3
  formula = G4_NEOPRENE
  name = G4_NEOPRENE
  specific = 4
FEATURE [App::DocumentObjectGroupPython] Space  # scripted group (container) (typed FeaturePython)
  Group = -> [G4_KEVLAR,G4_DACRON,G4_NEOPRENE]
FEATURE [App::DocumentObjectGroupPython] H_element121  label="H_element : 068"  # scripted group (container) (typed FeaturePython)
  n = 5
  ref = H_element
FEATURE [App::DocumentObjectGroupPython] C_element131  label="C_element : 076"  # scripted group (container) (typed FeaturePython)
  n = 4
  ref = C_element
FEATURE [App::DocumentObjectGroupPython] N_element051  label="N_element : 3"  # scripted group (container) (typed FeaturePython)
  n = 3
  ref = N_element
FEATURE [App::DocumentObjectGroupPython] O_element113  label="O_element : 066"  # scripted group (container) (typed FeaturePython)
  n = 1
  ref = O_element
FEATURE [App::DocumentObjectGroupPython] G4_CYTOSINE  # scripted group (container) (typed FeaturePython)
  Dunit = g/cm3
  Dvalue = 1.55
  Group = -> [H_element121,C_element131,N_element051,O_element113]
  conduct = 2
  density = 1
  expand = 3
  formula = G4_CYTOSINE
  name = G4_CYTOSINE
  specific = 4
FEATURE [App::DocumentObjectGroupPython] H_element122  label="H_element : 069"  # scripted group (container) (typed FeaturePython)
  n = 6
  ref = H_element
FEATURE [App::DocumentObjectGroupPython] C_element132  label="C_element : 077"  # scripted group (container) (typed FeaturePython)
  n = 5
  ref = C_element
FEATURE [App::DocumentObjectGroupPython] N_element052  label="N_element : 024"  # scripted group (container) (typed FeaturePython)
  n = 2
  ref = N_element
FEATURE [App::DocumentObjectGroupPython] O_element114  label="O_element : 067"  # scripted group (container) (typed FeaturePython)
  n = 2
  ref = O_element
FEATURE [App::DocumentObjectGroupPython] G4_THYMINE  # scripted group (container) (typed FeaturePython)
  Dunit = g/cm3
  Dvalue = 1.23
  Group = -> [H_element122,C_element132,N_element052,O_element114]
  conduct = 2
  density = 1
  expand = 3
  formula = G4_THYMINE
  name = G4_THYMINE
  specific = 4
FEATURE [App::DocumentObjectGroupPython] H_element123  label="H_element : 070"  # scripted group (container) (typed FeaturePython)
  n = 4
  ref = H_element
FEATURE [App::DocumentObjectGroupPython] C_element133  label="C_element : 078"  # scripted group (container) (typed FeaturePython)
  n = 4
  ref = C_element
FEATURE [App::DocumentObjectGroupPython] N_element053  label="N_element : 025"  # scripted group (container) (typed FeaturePython)
  n = 2
  ref = N_element
FEATURE [App::DocumentObjectGroupPython] O_element115  label="O_element : 068"  # scripted group (container) (typed FeaturePython)
  n = 2
  ref = O_element
FEATURE [App::DocumentObjectGroupPython] G4_URACIL  # scripted group (container) (typed FeaturePython)
  Dunit = g/cm3
  Dvalue = 1.32
  Group = -> [H_element123,C_element133,N_element053,O_element115]
  conduct = 2
  density = 1
  expand = 3
  formula = G4_URACIL
  name = G4_URACIL
  specific = 4
FEATURE [App::DocumentObjectGroupPython] H_element124  label="H_element : 071"  # scripted group (container) (typed FeaturePython)
  n = 4
  ref = H_element
FEATURE [App::DocumentObjectGroupPython] C_element134  label="C_element : 079"  # scripted group (container) (typed FeaturePython)
  n = 5
  ref = C_element
FEATURE [App::DocumentObjectGroupPython] N_element054  label="N_element : 026"  # scripted group (container) (typed FeaturePython)
  n = 5
  ref = N_element
FEATURE [App::DocumentObjectGroupPython] G4_DNA_ADENINE  # scripted group (container) (typed FeaturePython)
  Dunit = g/cm3
  Dvalue = 1
  Group = -> [H_element124,C_element134,N_element054]
  conduct = 2
  density = 1
  expand = 3
  formula = G4_DNA_ADENINE
  name = G4_DNA_ADENINE
  specific = 4
FEATURE [App::DocumentObjectGroupPython] H_element125  label="H_element : 072"  # scripted group (container) (typed FeaturePython)
  n = 4
  ref = H_element
FEATURE [App::DocumentObjectGroupPython] C_element135  label="C_element : 080"  # scripted group (container) (typed FeaturePython)
  n = 5
  ref = C_element
FEATURE [App::DocumentObjectGroupPython] N_element055  label="N_element : 027"  # scripted group (container) (typed FeaturePython)
  n = 5
  ref = N_element
FEATURE [App::DocumentObjectGroupPython] O_element116  label="O_element : 069"  # scripted group (container) (typed FeaturePython)
  n = 1
  ref = O_element
FEATURE [App::DocumentObjectGroupPython] G4_DNA_GUANINE  # scripted group (container) (typed FeaturePython)
  Dunit = g/cm3
  Dvalue = 1
  Group = -> [H_element125,C_element135,N_element055,O_element116]
  conduct = 2
  density = 1
  expand = 3
  formula = G4_DNA_GUANINE
  name = G4_DNA_GUANINE
  specific = 4
FEATURE [App::DocumentObjectGroupPython] H_element126  label="H_element : 073"  # scripted group (container) (typed FeaturePython)
  n = 4
  ref = H_element
FEATURE [App::DocumentObjectGroupPython] C_element136  label="C_element : 081"  # scripted group (container) (typed FeaturePython)
  n = 4
  ref = C_element
FEATURE [App::DocumentObjectGroupPython] N_element056  label="N_element : 028"  # scripted group (container) (typed FeaturePython)
  n = 3
  ref = N_element
FEATURE [App::DocumentObjectGroupPython] O_element117  label="O_element : 070"  # scripted group (container) (typed FeaturePython)
  n = 1
  ref = O_element
FEATURE [App::DocumentObjectGroupPython] G4_DNA_CYTOSINE  # scripted group (container) (typed FeaturePython)
  Dunit = g/cm3
  Dvalue = 1
  Group = -> [H_element126,C_element136,N_element056,O_element117]
  conduct = 2
  density = 1
  expand = 3
  formula = G4_DNA_CYTOSINE
  name = G4_DNA_CYTOSINE
  specific = 4
FEATURE [App::DocumentObjectGroupPython] H_element127  label="H_element : 074"  # scripted group (container) (typed FeaturePython)
  n = 5
  ref = H_element
FEATURE [App::DocumentObjectGroupPython] C_element137  label="C_element : 082"  # scripted group (container) (typed FeaturePython)
  n = 5
  ref = C_element
FEATURE [App::DocumentObjectGroupPython] N_element057  label="N_element : 029"  # scripted group (container) (typed FeaturePython)
  n = 2
  ref = N_element
FEATURE [App::DocumentObjectGroupPython] O_element118  label="O_element : 071"  # scripted group (container) (typed FeaturePython)
  n = 2
  ref = O_element
FEATURE [App::DocumentObjectGroupPython] G4_DNA_THYMINE  # scripted group (container) (typed FeaturePython)
  Dunit = g/cm3
  Dvalue = 1
  Group = -> [H_element127,C_element137,N_element057,O_element118]
  conduct = 2
  density = 1
  expand = 3
  formula = G4_DNA_THYMINE
  name = G4_DNA_THYMINE
  specific = 4
FEATURE [App::DocumentObjectGroupPython] H_element128  label="H_element : 075"  # scripted group (container) (typed FeaturePython)
  n = 3
  ref = H_element
FEATURE [App::DocumentObjectGroupPython] C_element138  label="C_element : 083"  # scripted group (container) (typed FeaturePython)
  n = 4
  ref = C_element
FEATURE [App::DocumentObjectGroupPython] N_element058  label="N_element : 030"  # scripted group (container) (typed FeaturePython)
  n = 2
  ref = N_element
FEATURE [App::DocumentObjectGroupPython] O_element119  label="O_element : 072"  # scripted group (container) (typed FeaturePython)
  n = 2
  ref = O_element
FEATURE [App::DocumentObjectGroupPython] G4_DNA_URACIL  # scripted group (container) (typed FeaturePython)
  Dunit = g/cm3
  Dvalue = 1
  Group = -> [H_element128,C_element138,N_element058,O_element119]
  conduct = 2
  density = 1
  expand = 3
  formula = G4_DNA_URACIL
  name = G4_DNA_URACIL
  specific = 4
FEATURE [App::DocumentObjectGroupPython] H_element129  label="H_element : 076"  # scripted group (container) (typed FeaturePython)
  n = 10
  ref = H_element
FEATURE [App::DocumentObjectGroupPython] C_element139  label="C_element : 084"  # scripted group (container) (typed FeaturePython)
  n = 10
  ref = C_element
FEATURE [App::DocumentObjectGroupPython] N_element059  label="N_element : 031"  # scripted group (container) (typed FeaturePython)
  n = 5
  ref = N_element
FEATURE [App::DocumentObjectGroupPython] O_element120  label="O_element : 073"  # scripted group (container) (typed FeaturePython)
  n = 4
  ref = O_element
FEATURE [App::DocumentObjectGroupPython] G4_DNA_ADENOSINE  # scripted group (container) (typed FeaturePython)
  Dunit = g/cm3
  Dvalue = 1
  Group = -> [H_element129,C_element139,N_element059,O_element120]
  conduct = 2
  density = 1
  expand = 3
  formula = G4_DNA_ADENOSINE
  name = G4_DNA_ADENOSINE
  specific = 4
FEATURE [App::DocumentObjectGroupPython] H_element130  label="H_element : 077"  # scripted group (container) (typed FeaturePython)
  n = 10
  ref = H_element
FEATURE [App::DocumentObjectGroupPython] C_element140  label="C_element : 085"  # scripted group (container) (typed FeaturePython)
  n = 10
  ref = C_element
FEATURE [App::DocumentObjectGroupPython] N_element060  label="N_element : 032"  # scripted group (container) (typed FeaturePython)
  n = 5
  ref = N_element
FEATURE [App::DocumentObjectGroupPython] O_element121  label="O_element : 074"  # scripted group (container) (typed FeaturePython)
  n = 5
  ref = O_element
FEATURE [App::DocumentObjectGroupPython] G4_DNA_GUANOSINE  # scripted group (container) (typed FeaturePython)
  Dunit = g/cm3
  Dvalue = 1
  Group = -> [H_element130,C_element140,N_element060,O_element121]
  conduct = 2
  density = 1
  expand = 3
  formula = G4_DNA_GUANOSINE
  name = G4_DNA_GUANOSINE
  specific = 4
FEATURE [App::DocumentObjectGroupPython] H_element131  label="H_element : 078"  # scripted group (container) (typed FeaturePython)
  n = 10
  ref = H_element
FEATURE [App::DocumentObjectGroupPython] C_element141  label="C_element : 086"  # scripted group (container) (typed FeaturePython)
  n = 9
  ref = C_element
FEATURE [App::DocumentObjectGroupPython] N_element061  label="N_element : 033"  # scripted group (container) (typed FeaturePython)
  n = 3
  ref = N_element
FEATURE [App::DocumentObjectGroupPython] O_element122  label="O_element : 075"  # scripted group (container) (typed FeaturePython)
  n = 5
  ref = O_element
FEATURE [App::DocumentObjectGroupPython] G4_DNA_CYTIDINE  # scripted group (container) (typed FeaturePython)
  Dunit = g/cm3
  Dvalue = 1
  Group = -> [H_element131,C_element141,N_element061,O_element122]
  conduct = 2
  density = 1
  expand = 3
  formula = G4_DNA_CYTIDINE
  name = G4_DNA_CYTIDINE
  specific = 4
FEATURE [App::DocumentObjectGroupPython] H_element132  label="H_element : 079"  # scripted group (container) (typed FeaturePython)
  n = 9
  ref = H_element
FEATURE [App::DocumentObjectGroupPython] C_element142  label="C_element : 087"  # scripted group (container) (typed FeaturePython)
  n = 9
  ref = C_element
FEATURE [App::DocumentObjectGroupPython] N_element062  label="N_element : 034"  # scripted group (container) (typed FeaturePython)
  n = 2
  ref = N_element
FEATURE [App::DocumentObjectGroupPython] O_element123  label="O_element : 076"  # scripted group (container) (typed FeaturePython)
  n = 6
  ref = O_element
FEATURE [App::DocumentObjectGroupPython] G4_DNA_URIDINE  # scripted group (container) (typed FeaturePython)
  Dunit = g/cm3
  Dvalue = 1
  Group = -> [H_element132,C_element142,N_element062,O_element123]
  conduct = 2
  density = 1
  expand = 3
  formula = G4_DNA_URIDINE
  name = G4_DNA_URIDINE
  specific = 4
FEATURE [App::DocumentObjectGroupPython] H_element133  label="H_element : 080"  # scripted group (container) (typed FeaturePython)
  n = 11
  ref = H_element
FEATURE [App::DocumentObjectGroupPython] C_element143  label="C_element : 088"  # scripted group (container) (typed FeaturePython)
  n = 10
  ref = C_element
FEATURE [App::DocumentObjectGroupPython] N_element063  label="N_element : 035"  # scripted group (container) (typed FeaturePython)
  n = 2
  ref = N_element
FEATURE [App::DocumentObjectGroupPython] O_element124  label="O_element : 077"  # scripted group (container) (typed FeaturePython)
  n = 6
  ref = O_element
FEATURE [App::DocumentObjectGroupPython] G4_DNA_METHYLURIDINE  # scripted group (container) (typed FeaturePython)
  Dunit = g/cm3
  Dvalue = 1
  Group = -> [H_element133,C_element143,N_element063,O_element124]
  conduct = 2
  density = 1
  expand = 3
  formula = G4_DNA_METHYLURIDINE
  name = G4_DNA_METHYLURIDINE
  specific = 4
FEATURE [App::DocumentObjectGroupPython] P_element014  label="P_element : 003"  # scripted group (container) (typed FeaturePython)
  n = 1
  ref = P_element
FEATURE [App::DocumentObjectGroupPython] O_element125  label="O_element : 078"  # scripted group (container) (typed FeaturePython)
  n = 3
  ref = O_element
FEATURE [App::DocumentObjectGroupPython] G4_DNA_MONOPHOSPHATE  # scripted group (container) (typed FeaturePython)
  Dunit = g/cm3
  Dvalue = 1
  Group = -> [P_element014,O_element125]
  conduct = 2
  density = 1
  expand = 3
  formula = G4_DNA_MONOPHOSPHATE
  name = G4_DNA_MONOPHOSPHATE
  specific = 4
FEATURE [App::DocumentObjectGroupPython] H_element134  label="H_element : 081"  # scripted group (container) (typed FeaturePython)
  n = 10
  ref = H_element
FEATURE [App::DocumentObjectGroupPython] C_element144  label="C_element : 089"  # scripted group (container) (typed FeaturePython)
  n = 10
  ref = C_element
FEATURE [App::DocumentObjectGroupPython] N_element064  label="N_element : 036"  # scripted group (container) (typed FeaturePython)
  n = 5
  ref = N_element
FEATURE [App::DocumentObjectGroupPython] O_element126  label="O_element : 079"  # scripted group (container) (typed FeaturePython)
  n = 7
  ref = O_element
FEATURE [App::DocumentObjectGroupPython] P_element015  label="P_element : 004"  # scripted group (container) (typed FeaturePython)
  n = 1
  ref = P_element
FEATURE [App::DocumentObjectGroupPython] G4_DNA_A  # scripted group (container) (typed FeaturePython)
  Dunit = g/cm3
  Dvalue = 1
  Group = -> [H_element134,C_element144,N_element064,O_element126,P_element015]
  conduct = 2
  density = 1
  expand = 3
  formula = G4_DNA_A
  name = G4_DNA_A
  specific = 4
FEATURE [App::DocumentObjectGroupPython] H_element135  label="H_element : 082"  # scripted group (container) (typed FeaturePython)
  n = 10
  ref = H_element
FEATURE [App::DocumentObjectGroupPython] C_element145  label="C_element : 090"  # scripted group (container) (typed FeaturePython)
  n = 10
  ref = C_element
FEATURE [App::DocumentObjectGroupPython] N_element065  label="N_element : 037"  # scripted group (container) (typed FeaturePython)
  n = 5
  ref = N_element
FEATURE [App::DocumentObjectGroupPython] O_element127  label="O_element : 8"  # scripted group (container) (typed FeaturePython)
  n = 8
  ref = O_element
FEATURE [App::DocumentObjectGroupPython] P_element016  label="P_element : 005"  # scripted group (container) (typed FeaturePython)
  n = 1
  ref = P_element
FEATURE [App::DocumentObjectGroupPython] G4_DNA_G  # scripted group (container) (typed FeaturePython)
  Dunit = g/cm3
  Dvalue = 1
  Group = -> [H_element135,C_element145,N_element065,O_element127,P_element016]
  conduct = 2
  density = 1
  expand = 3
  formula = G4_DNA_G
  name = G4_DNA_G
  specific = 4
FEATURE [App::DocumentObjectGroupPython] H_element136  label="H_element : 083"  # scripted group (container) (typed FeaturePython)
  n = 10
  ref = H_element
FEATURE [App::DocumentObjectGroupPython] C_element146  label="C_element : 091"  # scripted group (container) (typed FeaturePython)
  n = 9
  ref = C_element
FEATURE [App::DocumentObjectGroupPython] N_element066  label="N_element : 038"  # scripted group (container) (typed FeaturePython)
  n = 3
  ref = N_element
FEATURE [App::DocumentObjectGroupPython] O_element128  label="O_element : 080"  # scripted group (container) (typed FeaturePython)
  n = 8
  ref = O_element
FEATURE [App::DocumentObjectGroupPython] P_element017  label="P_element : 006"  # scripted group (container) (typed FeaturePython)
  n = 1
  ref = P_element
FEATURE [App::DocumentObjectGroupPython] G4_DNA_C  # scripted group (container) (typed FeaturePython)
  Dunit = g/cm3
  Dvalue = 1
  Group = -> [H_element136,C_element146,N_element066,O_element128,P_element017]
  conduct = 2
  density = 1
  expand = 3
  formula = G4_DNA_C
  name = G4_DNA_C
  specific = 4
FEATURE [App::DocumentObjectGroupPython] H_element137  label="H_element : 084"  # scripted group (container) (typed FeaturePython)
  n = 9
  ref = H_element
FEATURE [App::DocumentObjectGroupPython] C_element147  label="C_element : 092"  # scripted group (container) (typed FeaturePython)
  n = 9
  ref = C_element
FEATURE [App::DocumentObjectGroupPython] N_element067  label="N_element : 039"  # scripted group (container) (typed FeaturePython)
  n = 2
  ref = N_element
FEATURE [App::DocumentObjectGroupPython] O_element129  label="O_element : 9"  # scripted group (container) (typed FeaturePython)
  n = 9
  ref = O_element
FEATURE [App::DocumentObjectGroupPython] P_element018  label="P_element : 007"  # scripted group (container) (typed FeaturePython)
  n = 1
  ref = P_element
FEATURE [App::DocumentObjectGroupPython] G4_DNA_U  # scripted group (container) (typed FeaturePython)
  Dunit = g/cm3
  Dvalue = 1
  Group = -> [H_element137,C_element147,N_element067,O_element129,P_element018]
  conduct = 2
  density = 1
  expand = 3
  formula = G4_DNA_U
  name = G4_DNA_U
  specific = 4
FEATURE [App::DocumentObjectGroupPython] H_element138  label="H_element : 085"  # scripted group (container) (typed FeaturePython)
  n = 11
  ref = H_element
FEATURE [App::DocumentObjectGroupPython] C_element148  label="C_element : 093"  # scripted group (container) (typed FeaturePython)
  n = 10
  ref = C_element
FEATURE [App::DocumentObjectGroupPython] N_element068  label="N_element : 040"  # scripted group (container) (typed FeaturePython)
  n = 2
  ref = N_element
FEATURE [App::DocumentObjectGroupPython] O_element130  label="O_element : 081"  # scripted group (container) (typed FeaturePython)
  n = 9
  ref = O_element
FEATURE [App::DocumentObjectGroupPython] P_element019  label="P_element : 008"  # scripted group (container) (typed FeaturePython)
  n = 1
  ref = P_element
FEATURE [App::DocumentObjectGroupPython] G4_DNA_MU  # scripted group (container) (typed FeaturePython)
  Dunit = g/cm3
  Dvalue = 1
  Group = -> [H_element138,C_element148,N_element068,O_element130,P_element019]
  conduct = 2
  density = 1
  expand = 3
  formula = G4_DNA_MU
  name = G4_DNA_MU
  specific = 4
FEATURE [App::DocumentObjectGroupPython] BioChemical  # scripted group (container) (typed FeaturePython)
  Group = -> [G4_CYTOSINE,G4_THYMINE,G4_URACIL,G4_DNA_ADENINE,G4_DNA_GUANINE,G4_DNA_CYTOSINE,G4_DNA_THYMINE,G4_DNA_URACIL,G4_DNA_ADENOSINE,G4_DNA_GUANOSINE,G4_DNA_CYTIDINE,G4_DNA_URIDINE,G4_DNA_METHYLURIDINE,G4_DNA_MONOPHOSPHATE,G4_DNA_A,G4_DNA_G,G4_DNA_C,G4_DNA_U,G4_DNA_MU]
FEATURE [App::DocumentObjectGroupPython] G4Materials  # scripted group (container) (typed FeaturePython)
  Group = -> [NIST,Element,HEP,Space,BioChemical]
  version = 1
FEATURE [App::DocumentObjectGroupPython] Geant4  # scripted group (container) (typed FeaturePython)
  Group = -> [G4Isotopes,G4Elements,G4Materials]
FEATURE [App::DocumentObjectGroupPython] Materials  # scripted group (container) (typed FeaturePython)
  Group = -> [Geant4]
FEATURE [Part::FeaturePython] GDMLBox_WorldBox  # WARN: FeaturePython — macro-defined, semantics opaque (R4)
  lunit = 2
  material = 5
  x = 273
  y = 273
  z = 130
FEATURE [Part::FeaturePython] GDMLBox_Box  # WARN: FeaturePython — macro-defined, semantics opaque (R4)
  Placement = pos=(20,0,0) rot=(0,0,1;0rad)
  lunit = 2
  material = 0
  x = 10
  y = 10
  z = 10
FEATURE [Part::FeaturePython] GDMLTube  # WARN: FeaturePython — macro-defined, semantics opaque (R4)
  Placement = pos=(17,-4,0) rot=(0,0,1;0rad)
  aunit = 1
  deltaphi = 90
  lunit = 2
  material = 0
  rmax = 7
  rmin = 5
  startphi = 0
  z = 7
FEATURE [App::Part] LV_Tube
  Group = -> [GDMLTube]
  Origin = -> Origin003
  SkinSurface = 0
FEATURE [App::Part] LV_Box
  Group = -> [GDMLBox_Box,LV_Tube]
  Origin = -> Origin002
  Placement = pos=(0,0,0) rot=(0,0,1;-0.523599rad)
FEATURE [Part::FeaturePython] Array  # Draft array (typed FeaturePython)
  AlwaysSyncPlacement = false
  Angle = 180
  ArrayType = 1
  Axis = (0,0,1)
  Base = -> LV_Box
  Center = (-20,-20,0)
  Count = 5
  ExpandArray = false
  Fuse = false
  IntervalAxis = (0,0,0)
  IntervalX = (100,0,0)
  IntervalY = (0,100,0)
  IntervalZ = (0,0,100)
  NumberCircles = 3
  NumberPolar = 5
  NumberX = 2
  NumberY = 2
  NumberZ = 1
  PlacementList = 5 placements: [(0,0,0),(-20,8.28427,0),(-40,3.55271e-15,0),(-48.2843,-20,0),(-40,-40,0)]
  RadialDistance = 50
  ScaleList = (5) [(1,1,1),(1,1,1),(1,1,1),(1,1,1),(1,1,1)]
  Symmetry = 1
  TangentialDistance = 25
FEATURE [App::Part] Part  label="experiment"
  Group = -> [LV_Box,Array]
  Origin = -> Origin001
FEATURE [Part::Sphere] Sphere
  Angle1 = -90
  Angle2 = 90
  Angle3 = 360
  AttacherType = Attacher::AttachEngine3D
  Placement = pos=(-20,-20,0) rot=(0,0,1;0rad)
  Radius = 1
FEATURE [App::Part] Part001
  Group = -> [Sphere]
  Origin = -> Origin004
FEATURE [App::Part] worldVOL
  Group = -> [GDMLBox_WorldBox,Part,Part001]
  Origin = -> Origin
